FCSTD DOCUMENT  (FreeCAD 0.20R)
Label: frame_05
License: CC-BY 3.0
LicenseURL: http://creativecommons.org/licenses/by/3.0/
objects: Part::Cylinder×309, Part::MultiFuse×214, Part::Box×195, Part::Cut×178, Part::Feature×95, Part::Fillet×92, Part::Chamfer×30, Part::Mirroring×14, App::DocumentObjectGroup×14, Part::Loft×6, Part::Part2DObjectPython×2, Part::Extrusion×1
note: 1136 computed .brp shape members not serialized (recipe doc carries the construction recipe); baked Part::Feature solids carry a one-line shape summary decoded from their .brp

FEATURE [Part::Box] Box
  AttacherType = Attacher::AttachEngine3D
  Height = 20
  Length = 120
  Placement = pos=(30,0,0) rot=(0,0,1;0rad)
  Width = 10
FEATURE [Part::Box] Box001
  AttacherType = Attacher::AttachEngine3D
  Height = 17
  Length = 30
  Placement = pos=(0,0,1.5) rot=(0,0,1;0rad)
  Width = 8.5
FEATURE [Part::Cylinder] Cylinder
  Angle = 360
  AttacherType = Attacher::AttachEngine3D
  FirstAngle = 0
  Height = 0.1
  Placement = pos=(0,5,10) rot=(0,1,0;1.5708rad)
  Radius = 2.6
  SecondAngle = 0
FEATURE [Part::Box] Box007  label="Cube"
  AttacherType = Attacher::AttachEngine3D
  Height = 20
  Length = 330
  Width = 10
FEATURE [Part::Box] Box008  label="Cube001"
  AttacherType = Attacher::AttachEngine3D
  Height = 17
  Length = 430
  Placement = pos=(0,1.5,1.5) rot=(0,0,1;0rad)
  Width = 10
FEATURE [Part::Fillet] Fillet
  Base = -> Box007
  Edges = 2 edges r=3: [Edge9,Edge10]
FEATURE [Part::Fillet] Fillet001
  Base = -> Box008
  Edges = 2 edges r=2: [Edge9,Edge10]
FEATURE [Part::Cut] Cut003
  Base = -> Fillet
  Refine = true
  Tool = -> Fillet001
FEATURE [Part::Fillet] Fillet002
  Base = -> Box007
  Edges = 2 edges r=3: [Edge9,Edge10]
FEATURE [Part::Fillet] Fillet003
  Base = -> Box008
  Edges = 2 edges r=2: [Edge9,Edge10]
FEATURE [Part::Cut] Cut004
  Base = -> Fillet002
  Placement = pos=(0,-1.5,0) rot=(0,0,1;0rad)
  Refine = true
  Tool = -> Fillet003
FEATURE [Part::Mirroring] Part__Mirroring  label="Cut (Mirror #1)"
  Base = (0,0,0)
  Normal = (0,1,0)
  Placement = pos=(0,81.5,0) rot=(0,0,1;0rad)
  Source = -> Cut003
FEATURE [Part::Fillet] Fillet004  label="lower-plate_00"
  Edges = 2 edges r=0.25: [Edge74,Edge75]
  Placement = pos=(-3,100,59) rot=(0.57735,-0.57735,-0.57735;2.0944rad)
FEATURE [Part::Cylinder] Cylinder009
  Angle = 360
  AttacherType = Attacher::AttachEngine3D
  FirstAngle = 0
  Height = 11
  Placement = pos=(-2,66.5,-1) rot=(0,1,0;1.5708rad)
  Radius = 1.25
  SecondAngle = 0
FEATURE [Part::Cylinder] Cylinder010
  Angle = 360
  AttacherType = Attacher::AttachEngine3D
  FirstAngle = 0
  Height = 11
  Placement = pos=(-2,13.5,-1) rot=(0,1,0;1.5708rad)
  Radius = 1.25
  SecondAngle = 0
FEATURE [Part::Cylinder] Cylinder011
  Angle = 360
  AttacherType = Attacher::AttachEngine3D
  FirstAngle = 0
  Height = 15
  Placement = pos=(-2,23,15) rot=(0,1,0;1.5708rad)
  Radius = 1.25
  SecondAngle = 0
FEATURE [Part::Cylinder] Cylinder012
  Angle = 360
  AttacherType = Attacher::AttachEngine3D
  FirstAngle = 0
  Height = 15
  Placement = pos=(-2,57,15) rot=(0,1,0;1.5708rad)
  Radius = 1.25
  SecondAngle = 0
FEATURE [Part::MultiFuse] Fusion010
  Placement = pos=(0,0,1) rot=(0,0,1;0rad)
  Refine = true
  Shapes = -> [Cylinder009,Cylinder011,Cylinder010,Cylinder012]
FEATURE [Part::Cut] Cut005
  Refine = true
  Tool = -> Fusion010
FEATURE [Part::Cylinder] Cylinder013
  Angle = 360
  AttacherType = Attacher::AttachEngine3D
  FirstAngle = 0
  Height = 2.5
  Placement = pos=(-4.5,12.5,-1) rot=(0,1,0;1.5708rad)
  Radius = 2
  SecondAngle = 0
FEATURE [Part::Cylinder] Cylinder014
  Angle = 360
  AttacherType = Attacher::AttachEngine3D
  FirstAngle = 0
  Height = 2.5
  Placement = pos=(-4.5,67.5,-1) rot=(0,1,0;1.5708rad)
  Radius = 2
  SecondAngle = 0
FEATURE [Part::Cylinder] Cylinder015
  Angle = 360
  AttacherType = Attacher::AttachEngine3D
  FirstAngle = 0
  Height = 11
  Placement = pos=(-7,66.5,-1) rot=(0,1,0;1.5708rad)
  Radius = 1.6
  SecondAngle = 0
FEATURE [Part::Cylinder] Cylinder016
  Angle = 360
  AttacherType = Attacher::AttachEngine3D
  FirstAngle = 0
  Height = 11
  Placement = pos=(-7,13.5,-1) rot=(0,1,0;1.5708rad)
  Radius = 1.6
  SecondAngle = 0
FEATURE [Part::MultiFuse] Fusion011
  Refine = true
  Shapes = -> [Cylinder016,Cylinder015]
FEATURE [Part::MultiFuse] Fusion012
  Refine = true
  Shapes = -> [Cylinder014,Cylinder013]
FEATURE [Part::MultiFuse] Fusion013
  Refine = true
  Shapes = -> [Fillet004,Fusion012]
FEATURE [Part::Cut] Cut006  label="cab_tilt_lower001"
  Base = -> Fusion013
  Placement = pos=(0,0,1) rot=(0,0,1;0rad)
  Refine = true
  Tool = -> Fusion011
FEATURE [Part::Fillet] Fillet009
  Base = -> Cut005
  Edges = 2 edges r=3: [Edge4,Edge16]
FEATURE [Part::MultiFuse] Fusion015  label="frame-bars001"
  Refine = true
  Shapes = -> [Cut004,Part__Mirroring]
FEATURE [Part::Cut] Cut007  label="cab_tilt_upper001"
  Placement = pos=(-2,100,54) rot=(0.57735,-0.57735,-0.57735;2.0944rad)
  Refine = true
FEATURE [Part::Cylinder] Cylinder021
  Angle = 360
  AttacherType = Attacher::AttachEngine3D
  FirstAngle = 0
  Height = 10
  Placement = pos=(-8,33.5,0) rot=(0,0,1;0rad)
  Radius = 1.2
  SecondAngle = 0
FEATURE [Part::Cylinder] Cylinder022
  Angle = 360
  AttacherType = Attacher::AttachEngine3D
  FirstAngle = 0
  Height = 10
  Placement = pos=(-8,25.5,0) rot=(0,0,1;0rad)
  Radius = 1.2
  SecondAngle = 0
FEATURE [Part::MultiFuse] Fusion016
  Placement = pos=(334,78.5,-19.5) rot=(1,0,0;1.5708rad)
  Refine = true
  Shapes = -> [Cylinder021,Cylinder022]
FEATURE [Part::Cylinder] Cylinder023
  Angle = 360
  AttacherType = Attacher::AttachEngine3D
  FirstAngle = 0
  Height = 10
  Placement = pos=(-8,25.5,0) rot=(0,0,1;0rad)
  Radius = 1.2
  SecondAngle = 0
FEATURE [Part::Cylinder] Cylinder024
  Angle = 360
  AttacherType = Attacher::AttachEngine3D
  FirstAngle = 0
  Height = 10
  Placement = pos=(-8,33.5,0) rot=(0,0,1;0rad)
  Radius = 1.2
  SecondAngle = 0
FEATURE [Part::MultiFuse] Fusion017
  Placement = pos=(312,78.5,-19.5) rot=(1,0,0;1.5708rad)
  Refine = true
  Shapes = -> [Cylinder024,Cylinder023]
FEATURE [Part::MultiFuse] Fusion018
  Placement = pos=(-20,0,0) rot=(0,0,1;0rad)
  Refine = true
  Shapes = -> [Fusion016,Fusion017]
FEATURE [Part::Cylinder] Cylinder025
  Angle = 360
  AttacherType = Attacher::AttachEngine3D
  FirstAngle = 0
  Height = 10
  Placement = pos=(416,80,5) rot=(1,0,0;1.5708rad)
  Radius = 1.8
  SecondAngle = 0
FEATURE [Part::Box] Box011  label="Cube004"
  AttacherType = Attacher::AttachEngine3D
  Height = 10
  Length = 10
  Placement = pos=(400,7,3) rot=(0,0,1;0rad)
  Width = 66
FEATURE [Part::Box] Box012  label="Cube005"
  AttacherType = Attacher::AttachEngine3D
  Height = 10
  Length = 10
  Placement = pos=(400,10,-2) rot=(0,0,1;0rad)
  Width = 60
FEATURE [Part::Box] Box013  label="Cube006"
  AttacherType = Attacher::AttachEngine3D
  Height = 10
  Length = 10
  Placement = pos=(400,15,8) rot=(0,0,1;0rad)
  Width = 50
FEATURE [Part::Box] Box014  label="Cube007"
  AttacherType = Attacher::AttachEngine3D
  Height = 10.2
  Length = 10.2
  Placement = pos=(399.9,8,2.9) rot=(0,0,1;0rad)
  Width = 64
FEATURE [Part::Cylinder] Cylinder026
  Angle = 360
  AttacherType = Attacher::AttachEngine3D
  FirstAngle = 0
  Height = 10
  Placement = pos=(405,80,6) rot=(1,0,0;1.5708rad)
  Radius = 1.1
  SecondAngle = 0
FEATURE [Part::Cylinder] Cylinder027
  Angle = 360
  AttacherType = Attacher::AttachEngine3D
  FirstAngle = 0
  Height = 2.5
  Placement = pos=(405,80,6) rot=(1,0,0;1.5708rad)
  Radius = 2.5
  SecondAngle = 0
FEATURE [Part::Chamfer] Chamfer002
  Base = -> Box013
  Edges = 2 edges r=5: [Edge9,Edge11]
FEATURE [Part::Chamfer] Chamfer003
  Base = -> Box012
  Edges = 2 edges r=5: [Edge9,Edge11]
FEATURE [Part::MultiFuse] Fusion019
  Refine = true
  Shapes = -> [Box011,Chamfer003]
FEATURE [Part::Cut] Cut013
  Base = -> Fusion019
  Refine = true
  Tool = -> Chamfer002
FEATURE [Part::Cylinder] Cylinder029
  Angle = 360
  AttacherType = Attacher::AttachEngine3D
  FirstAngle = 0
  Height = 10
  Placement = pos=(405,17,6) rot=(1,0,0;1.5708rad)
  Radius = 0.8
  SecondAngle = 0
FEATURE [Part::Cylinder] Cylinder030
  Angle = 360
  AttacherType = Attacher::AttachEngine3D
  FirstAngle = 0
  Height = 10
  Placement = pos=(405,73,6) rot=(1,0,0;1.5708rad)
  Radius = 0.8
  SecondAngle = 0
FEATURE [Part::MultiFuse] Fusion020
  Placement = pos=(2,0,0) rot=(0,0,1;0rad)
  Refine = true
  Shapes = -> [Cylinder029,Cylinder030]
FEATURE [Part::Cylinder] Cylinder031
  Angle = 360
  AttacherType = Attacher::AttachEngine3D
  FirstAngle = 0
  Height = 10
  Placement = pos=(400,35,3) rot=(0,1,0;1.5708rad)
  Radius = 0.8
  SecondAngle = 0
FEATURE [Part::Cylinder] Cylinder032
  Angle = 360
  AttacherType = Attacher::AttachEngine3D
  FirstAngle = 0
  Height = 10
  Placement = pos=(400,45,3) rot=(0,1,0;1.5708rad)
  Radius = 0.8
  SecondAngle = 0
FEATURE [Part::MultiFuse] Fusion021
  Refine = true
  Shapes = -> [Cylinder032,Cylinder031]
FEATURE [Part::Cylinder] Cylinder033
  Angle = 360
  AttacherType = Attacher::AttachEngine3D
  FirstAngle = 0
  Height = 10
  Placement = pos=(-8,25.5,0) rot=(0,0,1;0rad)
  Radius = 1.2
  SecondAngle = 0
FEATURE [Part::Cylinder] Cylinder034
  Angle = 360
  AttacherType = Attacher::AttachEngine3D
  FirstAngle = 0
  Height = 10
  Placement = pos=(-8,33.5,0) rot=(0,0,1;0rad)
  Radius = 1.2
  SecondAngle = 0
FEATURE [Part::MultiFuse] Fusion022
  Placement = pos=(12,80,-19.5) rot=(1,0,0;1.5708rad)
  Refine = true
  Shapes = -> [Cylinder034,Cylinder033]
FEATURE [Part::Cylinder] Cylinder035
  Angle = 360
  AttacherType = Attacher::AttachEngine3D
  FirstAngle = 0
  Height = 10
  Placement = pos=(-8,33.5,0) rot=(0,0,1;0rad)
  Radius = 1.2
  SecondAngle = 0
FEATURE [Part::Cylinder] Cylinder036
  Angle = 360
  AttacherType = Attacher::AttachEngine3D
  FirstAngle = 0
  Height = 10
  Placement = pos=(-8,25.5,0) rot=(0,0,1;0rad)
  Radius = 1.2
  SecondAngle = 0
FEATURE [Part::MultiFuse] Fusion023
  Placement = pos=(12,10,-19.5) rot=(1,0,0;1.5708rad)
  Refine = true
  Shapes = -> [Cylinder035,Cylinder036]
FEATURE [Part::MultiFuse] Fusion024
  Refine = true
  Shapes = -> [Fusion022,Fusion023]
FEATURE [Part::Cut] Cut016  label="front-cross-member__"
  Base = -> Fillet009
  Refine = true
  Tool = -> Fusion024
FEATURE [Part::Cut] Cut017
  Base = -> Box
  Refine = true
FEATURE [Part::MultiFuse] Fusion027
  Refine = true
  Shapes = -> [Cut017,Box001]
FEATURE [Part::Cut] Cut018
  Base = -> Fusion027
  Placement = pos=(280,70,0) rot=(0,0,1;0rad)
  Refine = true
  Tool = -> Cylinder
FEATURE [Part::Cut] Cut019
  Base = -> Cut018
  Refine = true
  Tool = -> Fusion018
FEATURE [Part::Cut] Cut020
  Base = -> Cut019
  Refine = true
  Tool = -> Cylinder025
FEATURE [Part::Cut] Cut021
  Base = -> Cut020
  Refine = true
  Tool = -> Box014
FEATURE [Part::MultiFuse] Fusion028
  Placement = pos=(2,0,0) rot=(0,0,1;0rad)
  Refine = true
  Shapes = -> [Cylinder027,Cylinder026]
FEATURE [Part::Cut] Cut022
  Base = -> Cut021
  Refine = true
  Tool = -> Fusion028
FEATURE [Part::Fillet] Fillet016
  Base = -> Cut022
  Edges = 8 edges r=2.7: [Edge26,Edge28,Edge40,Edge42,Edge44,Edge46,Edge50,Edge52]
FEATURE [Part::Cut] Cut023
  Base = -> Cut021
  Refine = true
  Tool = -> Fusion028
FEATURE [Part::Fillet] Fillet017  label="rear-right-cross-member_"
  Base = -> Cut023
  Edges = 8 edges r=2.7: [Edge26,Edge28,Edge40,Edge42,Edge44,Edge46,Edge50,Edge52]
  Placement = pos=(20,1.5,0) rot=(0,0,1;0rad)
FEATURE [Part::Mirroring] Part__Mirroring001  label="rear-left-cross-member_"
  Base = (0,0,0)
  Normal = (0,1,0)
  Placement = pos=(20,78.5,0) rot=(0,0,1;0rad)
  Source = -> Fillet016
FEATURE [Part::Fillet] Fillet018
  Base = -> Cut013
  Edges = 8 edges r=5: [Edge2,Edge16,Edge29,Edge30,Edge33,Edge34,Edge35,Edge36]
FEATURE [Part::Cut] Cut024
  Base = -> Fillet018
  Refine = true
  Tool = -> Fusion021
FEATURE [Part::Cut] Cut025  label="rear-cross-member_"
  Base = -> Cut024
  Placement = pos=(20,0,0) rot=(0,0,1;0rad)
  Refine = true
  Tool = -> Fusion020
FEATURE [Part::Box] Box015  label="Cube008"
  AttacherType = Attacher::AttachEngine3D
  Height = 17
  Length = 12
  Placement = pos=(300,8,1.5) rot=(0,0,1;0rad)
  Width = 63
FEATURE [Part::Box] Box016  label="Cube009"
  AttacherType = Attacher::AttachEngine3D
  Height = 14
  Length = 1
  Placement = pos=(311,8,3) rot=(0,0,1;0rad)
  Width = 63
FEATURE [Part::Cut] Cut026
  Base = -> Box015
  Refine = true
  Tool = -> Box016
FEATURE [Part::Cylinder] Cylinder037
  Angle = 360
  AttacherType = Attacher::AttachEngine3D
  FirstAngle = 0
  Height = 10
  Placement = pos=(-8,33.5,0) rot=(0,0,1;0rad)
  Radius = 1.2
  SecondAngle = 0
FEATURE [Part::Cylinder] Cylinder038
  Angle = 360
  AttacherType = Attacher::AttachEngine3D
  FirstAngle = 0
  Height = 10
  Placement = pos=(-8,25.5,0) rot=(0,0,1;0rad)
  Radius = 1.2
  SecondAngle = 0
FEATURE [Part::MultiFuse] Fusion029
  Placement = pos=(312,18,-19.5) rot=(1,0,0;1.5708rad)
  Refine = true
  Shapes = -> [Cylinder037,Cylinder038]
FEATURE [Part::Cylinder] Cylinder039
  Angle = 360
  AttacherType = Attacher::AttachEngine3D
  FirstAngle = 0
  Height = 10
  Placement = pos=(-8,33.5,0) rot=(0,0,1;0rad)
  Radius = 1.2
  SecondAngle = 0
FEATURE [Part::Cylinder] Cylinder040
  Angle = 360
  AttacherType = Attacher::AttachEngine3D
  FirstAngle = 0
  Height = 10
  Placement = pos=(-8,25.5,0) rot=(0,0,1;0rad)
  Radius = 1.2
  SecondAngle = 0
FEATURE [Part::MultiFuse] Fusion030
  Placement = pos=(312,71,-19.5) rot=(1,0,0;1.5708rad)
  Refine = true
  Shapes = -> [Cylinder039,Cylinder040]
FEATURE [Part::MultiFuse] Fusion031
  Refine = true
  Shapes = -> [Fusion029,Fusion030]
FEATURE [Part::Cut] Cut027  label="middle-cross-member_"
  Base = -> Cut026
  Placement = pos=(20,0.5,0) rot=(0,0,1;0rad)
  Refine = true
  Tool = -> Fusion031
FEATURE [Part::Box] Box017  label="Cube010"
  AttacherType = Attacher::AttachEngine3D
  Height = 15
  Length = 30
  Placement = pos=(0,-0.25,0) rot=(0,0,1;0rad)
  Width = 11.5
FEATURE [Part::Box] Box018  label="Cube011"
  AttacherType = Attacher::AttachEngine3D
  Height = 8
  Length = 15
  Placement = pos=(16,1.75,0) rot=(0,0,1;0rad)
  Width = 7.5
FEATURE [Part::Box] Box019  label="Cube012"
  AttacherType = Attacher::AttachEngine3D
  Height = 15
  Length = 15
  Placement = pos=(0,-0.25,0) rot=(0,0,1;0rad)
  Width = 2.25
FEATURE [Part::Box] Box020  label="Cube013"
  AttacherType = Attacher::AttachEngine3D
  Height = 15
  Length = 15
  Placement = pos=(0,9,0) rot=(0,0,1;0rad)
  Width = 2.25
FEATURE [Part::MultiFuse] Fusion032
  Refine = true
  Shapes = -> [Box019,Box020]
FEATURE [Part::Cylinder] Cylinder041
  Angle = 360
  AttacherType = Attacher::AttachEngine3D
  FirstAngle = 0
  Height = 14.5
  Placement = pos=(20,12.25,4) rot=(1,0,0;1.5708rad)
  Radius = 2.1
  SecondAngle = 0
FEATURE [Part::Cylinder] Cylinder042
  Angle = 360
  AttacherType = Attacher::AttachEngine3D
  FirstAngle = 0
  Height = 15
  Placement = pos=(12,5.5,0) rot=(0,0,1;0rad)
  Radius = 1.6
  SecondAngle = 0
FEATURE [Part::Cylinder] Cylinder043
  Angle = 360
  AttacherType = Attacher::AttachEngine3D
  FirstAngle = 0
  Height = 15
  Placement = pos=(20,5.5,0) rot=(0,0,1;0rad)
  Radius = 1.6
  SecondAngle = 0
FEATURE [Part::Cylinder] Cylinder044
  Angle = 360
  AttacherType = Attacher::AttachEngine3D
  FirstAngle = 0
  Height = 11
  Placement = pos=(7,12,10.5) rot=(1,0,0;1.5708rad)
  Radius = 2.1
  SecondAngle = 0
FEATURE [Part::MultiFuse] Fusion033
  Refine = true
  Shapes = -> [Cylinder041,Cylinder044]
FEATURE [Part::Box] Box021  label="Cube014"
  AttacherType = Attacher::AttachEngine3D
  Height = 10
  Length = 10
  Placement = pos=(-7,0,6) rot=(0,0,1;0rad)
  Width = 10
FEATURE [Part::Box] Box022  label="Cube015"
  AttacherType = Attacher::AttachEngine3D
  Height = 9
  Length = 16
  Placement = pos=(2,2,8) rot=(0,0,1;0rad)
  Width = 7
FEATURE [Part::Cylinder] Cylinder045
  Angle = 360
  AttacherType = Attacher::AttachEngine3D
  FirstAngle = 0
  Height = 11
  Placement = pos=(10,11,11.5) rot=(1,0,0;1.5708rad)
  Radius = 2.1
  SecondAngle = 0
FEATURE [Part::Cylinder] Cylinder046
  Angle = 360
  AttacherType = Attacher::AttachEngine3D
  FirstAngle = 0
  Height = 17
  Placement = pos=(14,5.5,0) rot=(0,0,1;0rad)
  Radius = 1.6
  SecondAngle = 0
FEATURE [Part::Cylinder] Cylinder047
  Angle = 360
  AttacherType = Attacher::AttachEngine3D
  FirstAngle = 0
  Height = 17
  Placement = pos=(6,5.5,0) rot=(0,0,1;0rad)
  Radius = 1.6
  SecondAngle = 0
FEATURE [Part::Box] Box023  label="Cube016"
  AttacherType = Attacher::AttachEngine3D
  Height = 15
  Length = 16
  Placement = pos=(0,-0.25,0) rot=(0,0,1;0rad)
  Width = 11.5
FEATURE [Part::Box] Box024  label="Cube017"
  AttacherType = Attacher::AttachEngine3D
  Height = 8
  Length = 16
  Placement = pos=(0,1.75,0) rot=(0,0,1;0rad)
  Width = 7.5
FEATURE [Part::Cut] Cut028
  Base = -> Box023
  Placement = pos=(2,0,0) rot=(0,0,1;0rad)
  Refine = true
  Tool = -> Box024
FEATURE [Part::Cylinder] Cylinder048
  Angle = 360
  AttacherType = Attacher::AttachEngine3D
  FirstAngle = 0
  Height = 11.5
  Placement = pos=(10,11.25,4) rot=(1,0,0;1.5708rad)
  Radius = 2.1
  SecondAngle = 0
FEATURE [Part::Cylinder] Cylinder049
  Angle = 360
  AttacherType = Attacher::AttachEngine3D
  FirstAngle = 0
  Height = 15
  Placement = pos=(6,5.5,0) rot=(0,0,1;0rad)
  Radius = 1.6
  SecondAngle = 0
FEATURE [Part::Cylinder] Cylinder050
  Angle = 360
  AttacherType = Attacher::AttachEngine3D
  FirstAngle = 0
  Height = 15
  Placement = pos=(14,5.5,0) rot=(0,0,1;0rad)
  Radius = 1.6
  SecondAngle = 0
FEATURE [Part::MultiFuse] Fusion034
  Refine = true
  Shapes = -> [Cylinder048,Cylinder050,Cylinder049]
FEATURE [Part::Cut] Cut029
  Base = -> Cut028
  Refine = true
  Tool = -> Fusion034
FEATURE [Part::Box] Box025  label="Cube018"
  AttacherType = Attacher::AttachEngine3D
  Height = 9
  Length = 24
  Width = 14
FEATURE [Part::Box] Box026  label="Cube019"
  AttacherType = Attacher::AttachEngine3D
  Height = 7.5
  Length = 8
  Placement = pos=(16,2,0) rot=(0,0,1;0rad)
  Width = 7.5
FEATURE [Part::Cylinder] Cylinder051
  Angle = 360
  AttacherType = Attacher::AttachEngine3D
  FirstAngle = 0
  Height = 14
  Placement = pos=(20,13,4) rot=(1,0,0;1.5708rad)
  Radius = 2.1
  SecondAngle = 0
FEATURE [Part::Cylinder] Cylinder052
  Angle = 360
  AttacherType = Attacher::AttachEngine3D
  FirstAngle = 0
  Height = 15
  Placement = pos=(12,7.5,0) rot=(0,0,1;0rad)
  Radius = 1.6
  SecondAngle = 0
FEATURE [Part::Cylinder] Cylinder053
  Angle = 360
  AttacherType = Attacher::AttachEngine3D
  FirstAngle = 0
  Height = 15
  Placement = pos=(4,7.5,0) rot=(0,0,1;0rad)
  Radius = 1.6
  SecondAngle = 0
FEATURE [Part::Cylinder] Cylinder054
  Angle = 360
  AttacherType = Attacher::AttachEngine3D
  FirstAngle = 0
  Height = 4
  Placement = pos=(12,7.5,0) rot=(0,0,1;0rad)
  Radius = 3.2
  SecondAngle = 0
FEATURE [Part::Cylinder] Cylinder055
  Angle = 360
  AttacherType = Attacher::AttachEngine3D
  FirstAngle = 0
  Height = 4
  Placement = pos=(4,7.5,0) rot=(0,0,1;0rad)
  Radius = 3.2
  SecondAngle = 0
FEATURE [Part::MultiFuse] Fusion035
  Placement = pos=(0,1,0) rot=(0,0,1;0rad)
  Refine = true
  Shapes = -> [Cylinder051,Cylinder052,Cylinder053,Cylinder054,Cylinder055]
FEATURE [Part::Chamfer] Chamfer004
  Base = -> Box025
  Edges = 1 edges r=5: [Edge4]
FEATURE [Part::Cut] Cut030
  Base = -> Chamfer004
  Refine = true
  Tool = -> Box026
FEATURE [Part::Cylinder] Cylinder056
  Angle = 360
  AttacherType = Attacher::AttachEngine3D
  FirstAngle = 0
  Height = 11
  Placement = pos=(20,5.5,0) rot=(0,0,1;0rad)
  Radius = 3.1
  SecondAngle = 0
FEATURE [Part::Cylinder] Cylinder057
  Angle = 360
  AttacherType = Attacher::AttachEngine3D
  FirstAngle = 0
  Height = 11
  Placement = pos=(12,5.5,0) rot=(0,0,1;0rad)
  Radius = 3.1
  SecondAngle = 0
FEATURE [Part::MultiFuse] Fusion036
  Refine = true
  Shapes = -> [Cylinder056,Cylinder042,Cylinder043,Cylinder057]
FEATURE [Part::Box] Box027  label="Cube020"
  AttacherType = Attacher::AttachEngine3D
  Height = 18
  Length = 10
  Placement = pos=(25,-1,0) rot=(0,0,1;0rad)
  Width = 13
FEATURE [Part::Box] Box028  label="Cube021"
  AttacherType = Attacher::AttachEngine3D
  Height = 6
  Length = 16
  Placement = pos=(0,1.75,0) rot=(0,0,1;0rad)
  Width = 7.5
FEATURE [Part::MultiFuse] Fusion037
  Refine = true
  Shapes = -> [Box018,Box028]
FEATURE [Part::Cut] Cut033
  Base = -> Box017
  Refine = true
  Tool = -> Fusion037
FEATURE [Part::Cut] Cut034
  Base = -> Cut033
  Refine = true
  Tool = -> Fusion032
FEATURE [Part::Cut] Cut035
  Base = -> Cut034
  Refine = true
  Tool = -> Fusion036
FEATURE [Part::Cut] Cut036
  Base = -> Cut035
  Refine = true
  Tool = -> Fusion033
FEATURE [Part::MultiFuse] Fusion038
  Refine = true
  Shapes = -> [Box021,Box027]
FEATURE [Part::Cut] Cut037
  Base = -> Cut036
  Refine = true
  Tool = -> Fusion038
FEATURE [Part::Chamfer] Chamfer005
  Base = -> Cut029
  Edges = 4 edges r=5: [Edge3,Edge7,Edge17,Edge29]
FEATURE [Part::Fillet] Fillet022
  Base = -> Chamfer005
  Edges = 8 edges r=3: [Edge2,Edge7,Edge16,Edge35,Edge41,Edge42,Edge43,Edge47]
  Placement = pos=(22.5,71.75,-15) rot=(0,0,1;0rad)
FEATURE [Part::Cut] Cut038
  Placement = pos=(241.5,71.75,-16) rot=(0,0,1;0rad)
  Refine = true
FEATURE [Part::Chamfer] Chamfer009
  Base = -> Box022
  Edges = 2 edges r=1: [Edge4,Edge8]
FEATURE [Part::MultiFuse] Fusion040
  Refine = true
  Shapes = -> [Cylinder045,Cylinder046,Cylinder047]
FEATURE [Part::Cut] Cut039
  Base = -> Chamfer009
  Placement = pos=(241.5,-2.75,-16) rot=(0,0,1;0rad)
  Refine = true
  Tool = -> Fusion040
FEATURE [Part::Chamfer] Chamfer010
  Base = -> Cut029
  Edges = 4 edges r=5: [Edge3,Edge7,Edge17,Edge29]
FEATURE [Part::Fillet] Fillet025
  Base = -> Chamfer010
  Edges = 8 edges r=3: [Edge2,Edge7,Edge16,Edge35,Edge41,Edge42,Edge43,Edge47]
  Placement = pos=(22.5,-2.75,-15) rot=(0,0,1;0rad)
FEATURE [Part::Cut] Cut040
  Base = -> Cut030
  Placement = pos=(0,-5.5,-9) rot=(0,0,1;0rad)
  Refine = true
  Tool = -> Fusion035
FEATURE [Part::Box] Box029  label="Cube022"
  AttacherType = Attacher::AttachEngine3D
  Height = 10
  Length = 13
  Placement = pos=(0,-5.5,-9) rot=(0,0,1;0rad)
  Width = 4
FEATURE [Part::Cut] Cut041
  Base = -> Cut040
  Refine = true
  Tool = -> Box029
FEATURE [Part::Box] Box030  label="Cube023"
  AttacherType = Attacher::AttachEngine3D
  Height = 5
  Length = 13
  Placement = pos=(0,-2.5,-3) rot=(1,0,0;0.785398rad)
  Width = 5
FEATURE [Part::Cut] Cut043
  Base = -> Cut041
  Refine = true
  Tool = -> Box030
FEATURE [Part::Fillet] Fillet027
  Base = -> Cut043
  Edges = 1 edges r=2: [Edge14]
  Placement = pos=(290,0,0) rot=(0,0,1;0rad)
FEATURE [Part::Fillet] Fillet028
  Base = -> Fillet027
  Edges = 2 edges r=3: [Edge12,Edge13]
FEATURE [Part::Fillet] Fillet029
  Base = -> Fillet028
  Edges = 1 edges r=2.99: [Edge47]
FEATURE [Part::Chamfer] Chamfer011  label="front-left-front-ls-mount"
  Base = -> Fillet025
  Edges = 1 edges r=3.5: [Edge21]
FEATURE [Part::Chamfer] Chamfer012  label="front-right-front-ls-mount"
  Base = -> Fillet022
  Edges = 1 edges r=3.5: [Edge17]
FEATURE [Part::Chamfer] Chamfer015  label="front-left-rear-ls-mount"
  Base = -> Cut039
  Edges = 1 edges r=1.5: [Edge9]
FEATURE [Part::Chamfer] Chamfer016  label="front-right-rear-ls-mount"
  Base = -> Cut038
  Edges = 1 edges r=1.5: [Edge13]
FEATURE [Part::Fillet] Fillet030
  Base = -> Fillet027
  Edges = 2 edges r=3: [Edge12,Edge13]
FEATURE [Part::Fillet] Fillet031  label="rear-left-ls-mount_"
  Base = -> Fillet030
  Edges = 1 edges r=2.99: [Edge47]
  Placement = pos=(20,0,0) rot=(0,0,1;0rad)
FEATURE [Part::Mirroring] Part__Mirroring004  label="rear-right-ls-mount_"
  Base = (0,0,0)
  Normal = (0,1,0)
  Placement = pos=(20,80,0) rot=(0,0,1;0rad)
  Source = -> Fillet029
FEATURE [Part::Box] Box031
  AttacherType = Attacher::AttachEngine3D
  Height = 1
  Length = 16
  Placement = pos=(-2,9,18.5) rot=(0,0,1;0rad)
  Width = 62
FEATURE [Part::MultiFuse] Fusion041  label="front-cross-member_"
  Refine = true
  Shapes = -> [Cut016,Box031]
FEATURE [Part::Box] Box032
  AttacherType = Attacher::AttachEngine3D
  Height = 15
  Length = 10
  Placement = pos=(15,-1.25,0) rot=(0,0,1;0rad)
  Width = 1
FEATURE [Part::Box] Box033
  AttacherType = Attacher::AttachEngine3D
  Height = 15
  Length = 10
  Placement = pos=(15,11.25,0) rot=(0,0,1;0rad)
  Width = 1
FEATURE [Part::MultiFuse] Fusion042
  Refine = true
  Shapes = -> [Cut037,Box032,Box033]
FEATURE [Part::Cylinder] Cylinder058
  Angle = 360
  AttacherType = Attacher::AttachEngine3D
  FirstAngle = 0
  Height = 14.5
  Placement = pos=(20,12.25,4) rot=(1,0,0;1.5708rad)
  Radius = 2.1
  SecondAngle = 0
FEATURE [Part::Cut] Cut044
  Base = -> Fusion042
  Refine = true
  Tool = -> Cylinder058
FEATURE [Part::Box] Box034
  AttacherType = Attacher::AttachEngine3D
  Height = 10
  Length = 10
  Placement = pos=(7,0.5,-1.07) rot=(0,1,0;0.785398rad)
  Width = 10
FEATURE [Part::Cut] Cut045
  Base = -> Cut044
  Refine = true
  Tool = -> Box034
FEATURE [Part::Chamfer] Chamfer017
  Base = -> Cut045
  Edges = 1 edges r=4.5: [Edge7]
FEATURE [Part::Chamfer] Chamfer018
  Base = -> Chamfer017
  Edges = 4 edges r=3: [Edge36,Edge37,Edge46,Edge54]
FEATURE [Part::Chamfer] Chamfer019
  Base = -> Chamfer018
  Edges = 1 edges r=3: [Edge66]
FEATURE [Part::Fillet] Fillet032
  Base = -> Chamfer019
  Edges = 9 edges r=3: [Edge2,Edge16,Edge38,Edge62,Edge67,Edge77,Edge95,Edge114,Edge117]
FEATURE [Part::Chamfer] Chamfer020
  Base = -> Fillet032
  Edges = 1 edges r=1: [Edge22]
FEATURE [Part::Fillet] Fillet033
  Base = -> Chamfer019
  Edges = 9 edges r=3: [Edge2,Edge16,Edge38,Edge62,Edge67,Edge77,Edge95,Edge114,Edge117]
FEATURE [Part::Chamfer] Chamfer021  label="front-left-middle-ls-mount"
  Base = -> Fillet033
  Edges = 1 edges r=1: [Edge22]
  Placement = pos=(128.5,-2.75,-15) rot=(0,0,1;0rad)
FEATURE [Part::Mirroring] Part__Mirroring005  label="front-right-middle-ls-mount"
  Base = (0,0,0)
  Normal = (0,1,0)
  Placement = pos=(128.5,82.75,-15) rot=(0,0,1;0rad)
  Source = -> Chamfer020
FEATURE [Part::Box] Box035  label="Cube024"
  AttacherType = Attacher::AttachEngine3D
  Height = 25
  Length = 7
  Placement = pos=(8,16,-5) rot=(0,0,1;0rad)
  Width = 48
FEATURE [Part::Cut] Cut046
  Base = -> Fusion041
  Refine = true
  Tool = -> Box035
FEATURE [Part::Box] Box036  label="Cube025"
  AttacherType = Attacher::AttachEngine3D
  Height = 12
  Length = 15
  Placement = pos=(8,16,7.5) rot=(0,0,1;0rad)
  Width = 7
FEATURE [Part::Box] Box038  label="Cube027"
  AttacherType = Attacher::AttachEngine3D
  Height = 18
  Length = 3
  Placement = pos=(8,16,1.5) rot=(0,0,1;0rad)
  Width = 48
FEATURE [Part::Box] Box039  label="Cube028"
  AttacherType = Attacher::AttachEngine3D
  Height = 12
  Length = 12
  Placement = pos=(11,53,7.5) rot=(0,0,1;0rad)
  Width = 11
FEATURE [Part::Cylinder] Cylinder059
  Angle = 360
  AttacherType = Attacher::AttachEngine3D
  FirstAngle = 0
  Height = 15
  Placement = pos=(17,19.5,1.5) rot=(0,0,1;0rad)
  Radius = 0.9
  SecondAngle = 0
FEATURE [Part::Cylinder] Cylinder060
  Angle = 360
  AttacherType = Attacher::AttachEngine3D
  FirstAngle = 0
  Height = 15
  Placement = pos=(17,55.5,1.5) rot=(0,0,1;0rad)
  Radius = 0.9
  SecondAngle = 0
FEATURE [Part::MultiFuse] Fusion044
  Placement = pos=(0,0.5,4) rot=(0,0,1;0rad)
  Refine = true
  Shapes = -> [Cylinder059,Cylinder060]
FEATURE [Part::Cylinder] Cylinder061
  Angle = 360
  AttacherType = Attacher::AttachEngine3D
  FirstAngle = 0
  Height = 10
  Placement = pos=(-2,23,16) rot=(0,1,0;1.5708rad)
  Radius = 1.25
  SecondAngle = 0
FEATURE [Part::Cylinder] Cylinder062
  Angle = 360
  AttacherType = Attacher::AttachEngine3D
  FirstAngle = 0
  Height = 10
  Placement = pos=(-2,57,16) rot=(0,1,0;1.5708rad)
  Radius = 1.25
  SecondAngle = 0
FEATURE [Part::MultiFuse] Fusion045
  Refine = true
  Shapes = -> [Cylinder062,Cylinder061]
FEATURE [Part::Cylinder] Cylinder063
  Angle = 360
  AttacherType = Attacher::AttachEngine3D
  FirstAngle = 0
  Height = 10
  Placement = pos=(-2,23,16) rot=(0,1,0;1.5708rad)
  Radius = 1.25
  SecondAngle = 0
FEATURE [Part::Cylinder] Cylinder064
  Angle = 360
  AttacherType = Attacher::AttachEngine3D
  FirstAngle = 0
  Height = 10
  Placement = pos=(-2,57,16) rot=(0,1,0;1.5708rad)
  Radius = 1.25
  SecondAngle = 0
FEATURE [Part::MultiFuse] Fusion046
  Placement = pos=(0,0,-6) rot=(0,0,1;0rad)
  Refine = true
  Shapes = -> [Cylinder064,Cylinder063]
FEATURE [Part::MultiFuse] Fusion047
  Refine = true
  Shapes = -> [Cut046,Box036,Box038,Box039]
FEATURE [Part::Cut] Cut047
  Base = -> Fusion047
  Refine = true
  Tool = -> Fusion044
FEATURE [Part::MultiFuse] Fusion048
  Refine = true
  Shapes = -> [Fusion045,Cut047]
FEATURE [Part::Cut] Cut048
  Base = -> Fusion048
  Refine = true
  Tool = -> Fusion046
FEATURE [Part::Mirroring] Part__Mirroring006  label="Cut048 (Mirror #5)"
  Base = (0,0,0)
  Normal = (0,1,0)
  Source = -> Cut048
FEATURE [Part::Fillet] Fillet034
  Base = -> Part__Mirroring006
  Edges = 2 edges r=5: [Edge102,Edge118]
FEATURE [Part::Fillet] Fillet035
  Base = -> Fillet034
  Edges = 4 edges r=3: [Edge33,Edge54,Edge77,Edge79]
FEATURE [Part::Box] Box040
  AttacherType = Attacher::AttachEngine3D
  Height = 10
  Length = 10
  Placement = pos=(8,-18.5,-6.5) rot=(0,0,1;0rad)
  Width = 10
FEATURE [Part::Cut] Cut049
  Base = -> Fillet035
  Refine = true
  Tool = -> Box040
FEATURE [Part::Cylinder] Cylinder065
  Angle = 360
  AttacherType = Attacher::AttachEngine3D
  FirstAngle = 0
  Height = 10
  Placement = pos=(3,-59,-5) rot=(0,0,1;0rad)
  Radius = 1.25
  SecondAngle = 0
FEATURE [Part::Cylinder] Cylinder066
  Angle = 360
  AttacherType = Attacher::AttachEngine3D
  FirstAngle = 0
  Height = 10
  Placement = pos=(3,-21,-5) rot=(0,0,1;0rad)
  Radius = 1.25
  SecondAngle = 0
FEATURE [Part::MultiFuse] Fusion049
  Refine = true
  Shapes = -> [Cylinder065,Cylinder066]
FEATURE [Part::Cylinder] Cylinder067
  Angle = 360
  AttacherType = Attacher::AttachEngine3D
  FirstAngle = 0
  Height = 10
  Placement = pos=(5,-63,9.5) rot=(0,0,1;0rad)
  Radius = 1.25
  SecondAngle = 0
FEATURE [Part::Cylinder] Cylinder068
  Angle = 360
  AttacherType = Attacher::AttachEngine3D
  FirstAngle = 0
  Height = 10
  Placement = pos=(5,-17,9.5) rot=(0,0,1;0rad)
  Radius = 1.25
  SecondAngle = 0
FEATURE [Part::MultiFuse] Fusion050
  Refine = true
  Shapes = -> [Cylinder067,Cylinder068]
FEATURE [Part::Cut] Cut050
  Base = -> Cut049
  Refine = true
  Tool = -> Fusion049
FEATURE [Part::Cut] Cut051  label="front-cross-member"
  Base = -> Cut050
  Placement = pos=(2,80,0) rot=(0,0,1;0rad)
  Refine = true
  Tool = -> Fusion050
FEATURE [Part::Cylinder] Cylinder069
  Angle = 180
  AttacherType = Attacher::AttachEngine3D
  FirstAngle = 0
  Height = 48
  Placement = pos=(98,168,-23) rot=(1,0,0;1.5708rad)
  Radius = 52
  SecondAngle = 0
FEATURE [Part::Cylinder] Cylinder070
  Angle = 180
  AttacherType = Attacher::AttachEngine3D
  FirstAngle = 0
  Height = 48
  Placement = pos=(98,168,-27) rot=(1,0,0;1.5708rad)
  Radius = 47
  SecondAngle = 0
FEATURE [Part::Cut] Cut053
  Base = -> Cylinder069
  Refine = true
  Tool = -> Cylinder070
FEATURE [Part::Cylinder] Cylinder071
  Angle = 180
  AttacherType = Attacher::AttachEngine3D
  FirstAngle = 0
  Height = 48
  Placement = pos=(98,167,-23) rot=(1,0,0;1.5708rad)
  Radius = 50
  SecondAngle = 0
FEATURE [Part::Cut] Cut052
  Base = -> Cut053
  Placement = pos=(93,-35.5,3) rot=(0,0,1;0rad)
  Refine = true
  Tool = -> Cylinder071
FEATURE [Part::Cylinder] Cylinder072
  Angle = 180
  AttacherType = Attacher::AttachEngine3D
  FirstAngle = 0
  Height = 2
  Placement = pos=(191,123,-20) rot=(1,0,0;1.5708rad)
  Radius = 52.5
  SecondAngle = 0
FEATURE [Part::Cylinder] Cylinder073
  Angle = 180
  AttacherType = Attacher::AttachEngine3D
  FirstAngle = 0
  Height = 2
  Placement = pos=(191,110,-20) rot=(1,0,0;1.5708rad)
  Radius = 52.5
  SecondAngle = 0
FEATURE [Part::Cylinder] Cylinder074
  Angle = 180
  AttacherType = Attacher::AttachEngine3D
  FirstAngle = 0
  Height = 2
  Placement = pos=(191,97,-20) rot=(1,0,0;1.5708rad)
  Radius = 52.5
  SecondAngle = 0
FEATURE [Part::MultiFuse] Fusion051
  Placement = pos=(0,-1,0) rot=(0,0,1;0rad)
  Refine = true
  Shapes = -> [Cylinder074,Cylinder072,Cylinder073]
FEATURE [Part::Cylinder] Cylinder075
  Angle = 180
  AttacherType = Attacher::AttachEngine3D
  FirstAngle = 0
  Height = 48
  Placement = pos=(191,132,-20) rot=(1,0,0;1.5708rad)
  Radius = 50
  SecondAngle = 0
FEATURE [Part::Cut] Cut054
  Base = -> Fusion051
  Refine = true
  Tool = -> Cylinder075
FEATURE [Part::Fillet] Fillet036
  Base = -> Cut054
  Edges = 6 edges r=0.6: [Edge1,Edge3,Edge13,Edge15,Edge25,Edge27]
FEATURE [Part::MultiFuse] Fusion052
  Placement = pos=(6,0,0) rot=(0,0,1;0rad)
  Refine = true
  Shapes = -> [Cut052,Fillet036]
FEATURE [Part::Cylinder] Cylinder076
  Angle = 180
  AttacherType = Attacher::AttachEngine3D
  FirstAngle = 0
  Height = 48
  Placement = pos=(98,168,-23) rot=(1,0,0;1.5708rad)
  Radius = 52
  SecondAngle = 0
FEATURE [Part::Cylinder] Cylinder077
  Angle = 180
  AttacherType = Attacher::AttachEngine3D
  FirstAngle = 0
  Height = 48
  Placement = pos=(98,168,-27) rot=(1,0,0;1.5708rad)
  Radius = 47
  SecondAngle = 0
FEATURE [Part::Cut] Cut056
  Base = -> Cylinder076
  Refine = true
  Tool = -> Cylinder077
FEATURE [Part::Cylinder] Cylinder078
  Angle = 180
  AttacherType = Attacher::AttachEngine3D
  FirstAngle = 0
  Height = 48
  Placement = pos=(98,167,-23) rot=(1,0,0;1.5708rad)
  Radius = 50
  SecondAngle = 0
FEATURE [Part::Cut] Cut055
  Base = -> Cut056
  Placement = pos=(93,-35.5,3) rot=(0,0,1;0rad)
  Refine = true
  Tool = -> Cylinder078
FEATURE [Part::Cylinder] Cylinder079
  Angle = 180
  AttacherType = Attacher::AttachEngine3D
  FirstAngle = 0
  Height = 2
  Placement = pos=(191,97,-20) rot=(1,0,0;1.5708rad)
  Radius = 52.5
  SecondAngle = 0
FEATURE [Part::Cylinder] Cylinder080
  Angle = 180
  AttacherType = Attacher::AttachEngine3D
  FirstAngle = 0
  Height = 2
  Placement = pos=(191,123,-20) rot=(1,0,0;1.5708rad)
  Radius = 52.5
  SecondAngle = 0
FEATURE [Part::Cylinder] Cylinder081
  Angle = 180
  AttacherType = Attacher::AttachEngine3D
  FirstAngle = 0
  Height = 2
  Placement = pos=(191,110,-20) rot=(1,0,0;1.5708rad)
  Radius = 52.5
  SecondAngle = 0
FEATURE [Part::MultiFuse] Fusion054
  Placement = pos=(0,-1,0) rot=(0,0,1;0rad)
  Refine = true
  Shapes = -> [Cylinder079,Cylinder080,Cylinder081]
FEATURE [Part::Cylinder] Cylinder082
  Angle = 180
  AttacherType = Attacher::AttachEngine3D
  FirstAngle = 0
  Height = 48
  Placement = pos=(191,132,-20) rot=(1,0,0;1.5708rad)
  Radius = 50
  SecondAngle = 0
FEATURE [Part::Cut] Cut057
  Base = -> Fusion054
  Refine = true
  Tool = -> Cylinder082
FEATURE [Part::Fillet] Fillet037
  Base = -> Cut057
  Edges = 6 edges r=0.6: [Edge1,Edge3,Edge13,Edge15,Edge25,Edge27]
FEATURE [Part::MultiFuse] Fusion053
  Placement = pos=(189,0,0) rot=(0,0,1;0rad)
  Refine = true
  Shapes = -> [Cut055,Fillet037]
FEATURE [Part::Box] Box043  label="battery-pack"
  AttacherType = Attacher::AttachEngine3D
  Height = 30
  Length = 60
  Placement = pos=(259,83.5,-24) rot=(0,0,1;0rad)
  Width = 45
FEATURE [Part::Fillet] Fillet039
  Base = -> Fusion052
  Edges = 2 edges r=2: [Edge2,Edge11]
FEATURE [Part::Fillet] Fillet040
  Base = -> Fusion053
  Edges = 2 edges r=2: [Edge2,Edge11]
FEATURE [Part::Box] Box044  label="Cube032"
  AttacherType = Attacher::AttachEngine3D
  Height = 15
  Length = 10
  Placement = pos=(153.3,119,13.9) rot=(0,1,0;1.13446rad)
  Width = 4
FEATURE [Part::Box] Box045  label="Cube033"
  AttacherType = Attacher::AttachEngine3D
  Height = 25
  Length = 10
  Placement = pos=(146,119,-10) rot=(0,1,0;0.296706rad)
  Width = 4
FEATURE [Part::Cylinder] Cylinder084
  Angle = 360
  AttacherType = Attacher::AttachEngine3D
  FirstAngle = 0
  Height = 4
  Placement = pos=(154,123,13) rot=(1,0,0;1.5708rad)
  Radius = 2.5
  SecondAngle = 0
FEATURE [Part::MultiFuse] Fusion055
  Refine = true
  Shapes = -> [Box044,Box045,Cylinder084]
FEATURE [Part::Cylinder] Cylinder085
  Angle = 360
  AttacherType = Attacher::AttachEngine3D
  FirstAngle = 0
  Height = 4
  Placement = pos=(154,123,13) rot=(1,0,0;1.5708rad)
  Radius = 1.25
  SecondAngle = 0
FEATURE [Part::Cut] Cut058
  Base = -> Fusion055
  Refine = true
  Tool = -> Cylinder085
FEATURE [Part::Box] Box048  label="Cube036"
  AttacherType = Attacher::AttachEngine3D
  Height = 15
  Length = 10
  Placement = pos=(153.3,119,13.9) rot=(0,1,0;1.13446rad)
  Width = 4
FEATURE [Part::Box] Box049  label="Cube037"
  AttacherType = Attacher::AttachEngine3D
  Height = 25
  Length = 10
  Placement = pos=(146,119,-10) rot=(0,1,0;0.296706rad)
  Width = 4
FEATURE [Part::Cylinder] Cylinder088
  Angle = 360
  AttacherType = Attacher::AttachEngine3D
  FirstAngle = 0
  Height = 4
  Placement = pos=(154,123,13) rot=(1,0,0;1.5708rad)
  Radius = 1.25
  SecondAngle = 0
FEATURE [Part::Cylinder] Cylinder089
  Angle = 360
  AttacherType = Attacher::AttachEngine3D
  FirstAngle = 0
  Height = 4
  Placement = pos=(154,123,13) rot=(1,0,0;1.5708rad)
  Radius = 2.5
  SecondAngle = 0
FEATURE [Part::MultiFuse] Fusion057
  Refine = true
  Shapes = -> [Box048,Box049,Cylinder089]
FEATURE [Part::Cut] Cut060
  Base = -> Fusion057
  Placement = pos=(0,-21,0) rot=(0,0,1;0rad)
  Refine = true
  Tool = -> Cylinder088
FEATURE [Part::MultiFuse] Fusion059
  Refine = true
  Shapes = -> [Cut058,Cut060]
FEATURE [Part::Cylinder] Cylinder090
  Angle = 180
  AttacherType = Attacher::AttachEngine3D
  FirstAngle = 0
  Height = 48
  Placement = pos=(197,132,-20) rot=(1,0,0;1.5708rad)
  Radius = 50
  SecondAngle = 0
FEATURE [Part::Cut] Cut062
  Base = -> Fusion059
  Refine = true
  Tool = -> Cylinder090
FEATURE [Part::Box] Box051  label="Cube039"
  AttacherType = Attacher::AttachEngine3D
  Height = 52
  Length = 40
  Placement = pos=(141,81.5,-21) rot=(0,0,1;0rad)
  Width = 14
FEATURE [Part::Box] Box052  label="Cube040"
  AttacherType = Attacher::AttachEngine3D
  Height = 15
  Length = 10
  Placement = pos=(153.3,119,13.9) rot=(0,1,0;1.13446rad)
  Width = 4
FEATURE [Part::Box] Box053  label="Cube041"
  AttacherType = Attacher::AttachEngine3D
  Height = 25
  Length = 10
  Placement = pos=(146,119,-10) rot=(0,1,0;0.296706rad)
  Width = 4
FEATURE [Part::Cylinder] Cylinder091
  Angle = 360
  AttacherType = Attacher::AttachEngine3D
  FirstAngle = 0
  Height = 4
  Placement = pos=(154,123,13) rot=(1,0,0;1.5708rad)
  Radius = 2.5
  SecondAngle = 0
FEATURE [Part::MultiFuse] Fusion060
  Refine = true
  Shapes = -> [Box052,Box053,Cylinder091]
FEATURE [Part::Cylinder] Cylinder092
  Angle = 360
  AttacherType = Attacher::AttachEngine3D
  FirstAngle = 0
  Height = 4
  Placement = pos=(154,123,13) rot=(1,0,0;1.5708rad)
  Radius = 1.25
  SecondAngle = 0
FEATURE [Part::Cut] Cut064
  Base = -> Fusion060
  Refine = true
  Tool = -> Cylinder092
FEATURE [Part::Box] Box054  label="Cube042"
  AttacherType = Attacher::AttachEngine3D
  Height = 15
  Length = 10
  Placement = pos=(153.3,119,13.9) rot=(0,1,0;1.13446rad)
  Width = 4
FEATURE [Part::Box] Box055  label="Cube043"
  AttacherType = Attacher::AttachEngine3D
  Height = 25
  Length = 10
  Placement = pos=(146,119,-10) rot=(0,1,0;0.296706rad)
  Width = 4
FEATURE [Part::Cylinder] Cylinder093
  Angle = 360
  AttacherType = Attacher::AttachEngine3D
  FirstAngle = 0
  Height = 4
  Placement = pos=(154,123,13) rot=(1,0,0;1.5708rad)
  Radius = 1.25
  SecondAngle = 0
FEATURE [Part::Cylinder] Cylinder094
  Angle = 360
  AttacherType = Attacher::AttachEngine3D
  FirstAngle = 0
  Height = 4
  Placement = pos=(154,123,13) rot=(1,0,0;1.5708rad)
  Radius = 2.5
  SecondAngle = 0
FEATURE [Part::MultiFuse] Fusion061
  Refine = true
  Shapes = -> [Box054,Box055,Cylinder094]
FEATURE [Part::Cut] Cut065
  Base = -> Fusion061
  Placement = pos=(0,-26,0) rot=(0,0,1;0rad)
  Refine = true
  Tool = -> Cylinder093
FEATURE [Part::MultiFuse] Fusion062
  Refine = true
  Shapes = -> [Cut064,Cut065]
FEATURE [Part::Cylinder] Cylinder095
  Angle = 180
  AttacherType = Attacher::AttachEngine3D
  FirstAngle = 0
  Height = 48
  Placement = pos=(197,132,-20) rot=(1,0,0;1.5708rad)
  Radius = 50
  SecondAngle = 0
FEATURE [Part::Cut] Cut063
  Base = -> Fusion062
  Refine = true
  Tool = -> Cylinder095
FEATURE [Part::Mirroring] Part__Mirroring007  label="Cut063 (Mirror #6)"
  Base = (0,0,0)
  Normal = (1,0,0)
  Placement = pos=(394,0,0) rot=(0,0,1;0rad)
  Source = -> Cut063
FEATURE [Part::Cut] Cut066
  Base = -> Fillet039
  Refine = true
  Tool = -> Box051
FEATURE [Part::Cylinder] Cylinder103
  Angle = 360
  AttacherType = Attacher::AttachEngine3D
  FirstAngle = 0
  Height = 4
  Placement = pos=(154,123,13) rot=(1,0,0;1.5708rad)
  Radius = 1.25
  SecondAngle = 0
FEATURE [Part::Cylinder] Cylinder104
  Angle = 360
  AttacherType = Attacher::AttachEngine3D
  FirstAngle = 0
  Height = 4
  Placement = pos=(154,123,13) rot=(1,0,0;1.5708rad)
  Radius = 2.5
  SecondAngle = 0
FEATURE [Part::Cylinder] Cylinder105
  Angle = 180
  AttacherType = Attacher::AttachEngine3D
  FirstAngle = 0
  Height = 48
  Placement = pos=(197,132,-20) rot=(1,0,0;1.5708rad)
  Radius = 50
  SecondAngle = 0
FEATURE [Part::Box] Box056  label="Cube044"
  AttacherType = Attacher::AttachEngine3D
  Height = 25
  Length = 10
  Placement = pos=(146,119,-10) rot=(0,1,0;0.296706rad)
  Width = 4
FEATURE [Part::Box] Box057  label="Cube045"
  AttacherType = Attacher::AttachEngine3D
  Height = 25
  Length = 10
  Placement = pos=(146,119,-10) rot=(0,1,0;0.296706rad)
  Width = 4
FEATURE [Part::Box] Box058  label="Cube046"
  AttacherType = Attacher::AttachEngine3D
  Height = 15
  Length = 10
  Placement = pos=(153.3,119,13.9) rot=(0,1,0;1.13446rad)
  Width = 4
FEATURE [Part::MultiFuse] Fusion066
  Refine = true
  Shapes = -> [Box058,Box057,Cylinder104]
FEATURE [Part::Cylinder] Cylinder106
  Angle = 360
  AttacherType = Attacher::AttachEngine3D
  FirstAngle = 0
  Height = 4
  Placement = pos=(154,123,13) rot=(1,0,0;1.5708rad)
  Radius = 1.25
  SecondAngle = 0
FEATURE [Part::Cut] Cut072
  Base = -> Fusion066
  Placement = pos=(0,-26,0) rot=(0,0,1;0rad)
  Refine = true
  Tool = -> Cylinder106
FEATURE [Part::Box] Box059  label="Cube047"
  AttacherType = Attacher::AttachEngine3D
  Height = 15
  Length = 10
  Placement = pos=(153.3,119,13.9) rot=(0,1,0;1.13446rad)
  Width = 4
FEATURE [Part::Cylinder] Cylinder107
  Angle = 360
  AttacherType = Attacher::AttachEngine3D
  FirstAngle = 0
  Height = 4
  Placement = pos=(154,123,13) rot=(1,0,0;1.5708rad)
  Radius = 2.5
  SecondAngle = 0
FEATURE [Part::MultiFuse] Fusion067
  Refine = true
  Shapes = -> [Box059,Box056,Cylinder107]
FEATURE [Part::Cut] Cut071
  Base = -> Fusion067
  Refine = true
  Tool = -> Cylinder103
FEATURE [Part::MultiFuse] Fusion068
  Refine = true
  Shapes = -> [Cut071,Cut072]
FEATURE [Part::Cut] Cut070
  Base = -> Fusion068
  Placement = pos=(183,0,0) rot=(0,0,1;0rad)
  Refine = true
  Tool = -> Cylinder105
FEATURE [Part::Box] Box060  label="Cube048"
  AttacherType = Attacher::AttachEngine3D
  Height = 25
  Length = 10
  Placement = pos=(146,119,-10) rot=(0,1,0;0.296706rad)
  Width = 4
FEATURE [Part::Cylinder] Cylinder108
  Angle = 360
  AttacherType = Attacher::AttachEngine3D
  FirstAngle = 0
  Height = 4
  Placement = pos=(154,123,13) rot=(1,0,0;1.5708rad)
  Radius = 1.25
  SecondAngle = 0
FEATURE [Part::Cylinder] Cylinder109
  Angle = 360
  AttacherType = Attacher::AttachEngine3D
  FirstAngle = 0
  Height = 4
  Placement = pos=(154,123,13) rot=(1,0,0;1.5708rad)
  Radius = 2.5
  SecondAngle = 0
FEATURE [Part::Cylinder] Cylinder110
  Angle = 360
  AttacherType = Attacher::AttachEngine3D
  FirstAngle = 0
  Height = 4
  Placement = pos=(154,123,13) rot=(1,0,0;1.5708rad)
  Radius = 2.5
  SecondAngle = 0
FEATURE [Part::Cylinder] Cylinder111
  Angle = 180
  AttacherType = Attacher::AttachEngine3D
  FirstAngle = 0
  Height = 48
  Placement = pos=(197,132,-20) rot=(1,0,0;1.5708rad)
  Radius = 50
  SecondAngle = 0
FEATURE [Part::Box] Box061  label="Cube049"
  AttacherType = Attacher::AttachEngine3D
  Height = 25
  Length = 10
  Placement = pos=(146,119,-10) rot=(0,1,0;0.296706rad)
  Width = 4
FEATURE [Part::Box] Box062  label="Cube050"
  AttacherType = Attacher::AttachEngine3D
  Height = 15
  Length = 10
  Placement = pos=(153.3,119,13.9) rot=(0,1,0;1.13446rad)
  Width = 4
FEATURE [Part::MultiFuse] Fusion069
  Refine = true
  Shapes = -> [Box062,Box061,Cylinder109]
FEATURE [Part::Cylinder] Cylinder112
  Angle = 360
  AttacherType = Attacher::AttachEngine3D
  FirstAngle = 0
  Height = 4
  Placement = pos=(154,123,13) rot=(1,0,0;1.5708rad)
  Radius = 1.25
  SecondAngle = 0
FEATURE [Part::Cut] Cut074
  Base = -> Fusion069
  Placement = pos=(0,-26,0) rot=(0,0,1;0rad)
  Refine = true
  Tool = -> Cylinder112
FEATURE [Part::Box] Box063  label="Cube051"
  AttacherType = Attacher::AttachEngine3D
  Height = 15
  Length = 10
  Placement = pos=(153.3,119,13.9) rot=(0,1,0;1.13446rad)
  Width = 4
FEATURE [Part::MultiFuse] Fusion070
  Refine = true
  Shapes = -> [Box063,Box060,Cylinder110]
FEATURE [Part::Cut] Cut075
  Base = -> Fusion070
  Refine = true
  Tool = -> Cylinder108
FEATURE [Part::MultiFuse] Fusion071
  Refine = true
  Shapes = -> [Cut075,Cut074]
FEATURE [Part::Cut] Cut073
  Base = -> Fusion071
  Placement = pos=(183,0,0) rot=(0,0,1;0rad)
  Refine = true
  Tool = -> Cylinder111
FEATURE [Part::Mirroring] Part__Mirroring008  label="Cut073 (Mirror #7)"
  Base = (0,0,0)
  Normal = (1,0,0)
  Placement = pos=(760,0,0) rot=(0,0,1;0rad)
  Source = -> Cut073
FEATURE [Part::MultiFuse] Fusion072  label="rear-right-wing"
  Placement = pos=(1,0,-4) rot=(0,0,1;0rad)
  Refine = true
  Shapes = -> [Fillet040,Cut070,Part__Mirroring008]
FEATURE [Part::MultiFuse] Fusion073  label="front-right-wing_with_battery_hole_"
  Placement = pos=(0,0,-4) rot=(0,0,1;0rad)
  Refine = true
  Shapes = -> [Cut062,Cut066,Part__Mirroring007]
FEATURE [Part::Cylinder] Cylinder113
  Angle = 180
  AttacherType = Attacher::AttachEngine3D
  FirstAngle = 0
  Height = 48
  Placement = pos=(197,132,-20) rot=(1,0,0;1.5708rad)
  Radius = 50
  SecondAngle = 0
FEATURE [Part::Cylinder] Cylinder114
  Angle = 360
  AttacherType = Attacher::AttachEngine3D
  FirstAngle = 0
  Height = 4
  Placement = pos=(154,123,13) rot=(1,0,0;1.5708rad)
  Radius = 1.25
  SecondAngle = 0
FEATURE [Part::Cylinder] Cylinder115
  Angle = 360
  AttacherType = Attacher::AttachEngine3D
  FirstAngle = 0
  Height = 4
  Placement = pos=(154,123,13) rot=(1,0,0;1.5708rad)
  Radius = 2.5
  SecondAngle = 0
FEATURE [Part::Box] Box064  label="Cube052"
  AttacherType = Attacher::AttachEngine3D
  Height = 25
  Length = 10
  Placement = pos=(146,119,-10) rot=(0,1,0;0.296706rad)
  Width = 4
FEATURE [Part::Box] Box065  label="Cube053"
  AttacherType = Attacher::AttachEngine3D
  Height = 15
  Length = 10
  Placement = pos=(153.3,119,13.9) rot=(0,1,0;1.13446rad)
  Width = 4
FEATURE [Part::MultiFuse] Fusion074
  Refine = true
  Shapes = -> [Box065,Box064,Cylinder115]
FEATURE [Part::Cut] Cut076
  Base = -> Fusion074
  Placement = pos=(0,-26,0) rot=(0,0,1;0rad)
  Refine = true
  Tool = -> Cylinder114
FEATURE [Part::Cylinder] Cylinder116
  Angle = 360
  AttacherType = Attacher::AttachEngine3D
  FirstAngle = 0
  Height = 4
  Placement = pos=(154,123,13) rot=(1,0,0;1.5708rad)
  Radius = 1.25
  SecondAngle = 0
FEATURE [Part::Cylinder] Cylinder117
  Angle = 360
  AttacherType = Attacher::AttachEngine3D
  FirstAngle = 0
  Height = 4
  Placement = pos=(154,123,13) rot=(1,0,0;1.5708rad)
  Radius = 2.5
  SecondAngle = 0
FEATURE [Part::Box] Box066  label="Cube054"
  AttacherType = Attacher::AttachEngine3D
  Height = 25
  Length = 10
  Placement = pos=(146,119,-10) rot=(0,1,0;0.296706rad)
  Width = 4
FEATURE [Part::Box] Box067  label="Cube055"
  AttacherType = Attacher::AttachEngine3D
  Height = 15
  Length = 10
  Placement = pos=(153.3,119,13.9) rot=(0,1,0;1.13446rad)
  Width = 4
FEATURE [Part::MultiFuse] Fusion075
  Refine = true
  Shapes = -> [Box067,Box066,Cylinder117]
FEATURE [Part::Cut] Cut077
  Base = -> Fusion075
  Refine = true
  Tool = -> Cylinder116
FEATURE [Part::MultiFuse] Fusion076
  Refine = true
  Shapes = -> [Cut077,Cut076]
FEATURE [Part::Cut] Cut078
  Base = -> Fusion076
  Placement = pos=(183,0,0) rot=(0,0,1;0rad)
  Refine = true
  Tool = -> Cylinder113
FEATURE [Part::Mirroring] Part__Mirroring009  label="Cut073 (Mirror #7)001"
  Base = (0,0,0)
  Normal = (1,0,0)
  Placement = pos=(760,0,0) rot=(0,0,1;0rad)
  Source = -> Cut078
FEATURE [Part::Cylinder] Cylinder118
  Angle = 180
  AttacherType = Attacher::AttachEngine3D
  FirstAngle = 0
  Height = 48
  Placement = pos=(197,132,-20) rot=(1,0,0;1.5708rad)
  Radius = 50
  SecondAngle = 0
FEATURE [Part::Cylinder] Cylinder119
  Angle = 360
  AttacherType = Attacher::AttachEngine3D
  FirstAngle = 0
  Height = 4
  Placement = pos=(154,123,13) rot=(1,0,0;1.5708rad)
  Radius = 1.25
  SecondAngle = 0
FEATURE [Part::Cylinder] Cylinder120
  Angle = 360
  AttacherType = Attacher::AttachEngine3D
  FirstAngle = 0
  Height = 4
  Placement = pos=(154,123,13) rot=(1,0,0;1.5708rad)
  Radius = 2.5
  SecondAngle = 0
FEATURE [Part::Box] Box068  label="Cube056"
  AttacherType = Attacher::AttachEngine3D
  Height = 25
  Length = 10
  Placement = pos=(146,119,-10) rot=(0,1,0;0.296706rad)
  Width = 4
FEATURE [Part::Box] Box069  label="Cube057"
  AttacherType = Attacher::AttachEngine3D
  Height = 15
  Length = 10
  Placement = pos=(153.3,119,13.9) rot=(0,1,0;1.13446rad)
  Width = 4
FEATURE [Part::MultiFuse] Fusion077
  Refine = true
  Shapes = -> [Box069,Box068,Cylinder120]
FEATURE [Part::Cut] Cut079
  Base = -> Fusion077
  Placement = pos=(0,-26,0) rot=(0,0,1;0rad)
  Refine = true
  Tool = -> Cylinder119
FEATURE [Part::Cylinder] Cylinder121
  Angle = 360
  AttacherType = Attacher::AttachEngine3D
  FirstAngle = 0
  Height = 4
  Placement = pos=(154,123,13) rot=(1,0,0;1.5708rad)
  Radius = 1.25
  SecondAngle = 0
FEATURE [Part::Cylinder] Cylinder122
  Angle = 360
  AttacherType = Attacher::AttachEngine3D
  FirstAngle = 0
  Height = 4
  Placement = pos=(154,123,13) rot=(1,0,0;1.5708rad)
  Radius = 2.5
  SecondAngle = 0
FEATURE [Part::Box] Box070  label="Cube058"
  AttacherType = Attacher::AttachEngine3D
  Height = 25
  Length = 10
  Placement = pos=(146,119,-10) rot=(0,1,0;0.296706rad)
  Width = 4
FEATURE [Part::Box] Box071  label="Cube059"
  AttacherType = Attacher::AttachEngine3D
  Height = 15
  Length = 10
  Placement = pos=(153.3,119,13.9) rot=(0,1,0;1.13446rad)
  Width = 4
FEATURE [Part::MultiFuse] Fusion078
  Refine = true
  Shapes = -> [Box071,Box070,Cylinder122]
FEATURE [Part::Cut] Cut080
  Base = -> Fusion078
  Refine = true
  Tool = -> Cylinder121
FEATURE [Part::MultiFuse] Fusion079
  Refine = true
  Shapes = -> [Cut080,Cut079]
FEATURE [Part::Cut] Cut081
  Base = -> Fusion079
  Placement = pos=(183,0,0) rot=(0,0,1;0rad)
  Refine = true
  Tool = -> Cylinder118
FEATURE [Part::Cylinder] Cylinder123
  Angle = 180
  AttacherType = Attacher::AttachEngine3D
  FirstAngle = 0
  Height = 48
  Placement = pos=(191,132,-20) rot=(1,0,0;1.5708rad)
  Radius = 50
  SecondAngle = 0
FEATURE [Part::Cylinder] Cylinder124
  Angle = 180
  AttacherType = Attacher::AttachEngine3D
  FirstAngle = 0
  Height = 2
  Placement = pos=(191,110,-20) rot=(1,0,0;1.5708rad)
  Radius = 52.5
  SecondAngle = 0
FEATURE [Part::Cylinder] Cylinder125
  Angle = 180
  AttacherType = Attacher::AttachEngine3D
  FirstAngle = 0
  Height = 2
  Placement = pos=(191,123,-20) rot=(1,0,0;1.5708rad)
  Radius = 52.5
  SecondAngle = 0
FEATURE [Part::Cylinder] Cylinder126
  Angle = 180
  AttacherType = Attacher::AttachEngine3D
  FirstAngle = 0
  Height = 2
  Placement = pos=(191,97,-20) rot=(1,0,0;1.5708rad)
  Radius = 52.5
  SecondAngle = 0
FEATURE [Part::MultiFuse] Fusion080
  Placement = pos=(0,-1,0) rot=(0,0,1;0rad)
  Refine = true
  Shapes = -> [Cylinder126,Cylinder125,Cylinder124]
FEATURE [Part::Cut] Cut082
  Base = -> Fusion080
  Refine = true
  Tool = -> Cylinder123
FEATURE [Part::Fillet] Fillet041
  Base = -> Cut082
  Edges = 6 edges r=0.6: [Edge1,Edge3,Edge13,Edge15,Edge25,Edge27]
FEATURE [Part::Cylinder] Cylinder127
  Angle = 180
  AttacherType = Attacher::AttachEngine3D
  FirstAngle = 0
  Height = 48
  Placement = pos=(98,167,-23) rot=(1,0,0;1.5708rad)
  Radius = 50
  SecondAngle = 0
FEATURE [Part::Cylinder] Cylinder128
  Angle = 180
  AttacherType = Attacher::AttachEngine3D
  FirstAngle = 0
  Height = 48
  Placement = pos=(98,168,-27) rot=(1,0,0;1.5708rad)
  Radius = 47
  SecondAngle = 0
FEATURE [Part::Cylinder] Cylinder129
  Angle = 180
  AttacherType = Attacher::AttachEngine3D
  FirstAngle = 0
  Height = 48
  Placement = pos=(98,168,-23) rot=(1,0,0;1.5708rad)
  Radius = 52
  SecondAngle = 0
FEATURE [Part::Cut] Cut083
  Base = -> Cylinder129
  Refine = true
  Tool = -> Cylinder128
FEATURE [Part::Cut] Cut084
  Base = -> Cut083
  Placement = pos=(93,-35.5,3) rot=(0,0,1;0rad)
  Refine = true
  Tool = -> Cylinder127
FEATURE [Part::MultiFuse] Fusion081
  Placement = pos=(189,0,0) rot=(0,0,1;0rad)
  Refine = true
  Shapes = -> [Cut084,Fillet041]
FEATURE [Part::Fillet] Fillet042
  Base = -> Fusion081
  Edges = 2 edges r=2: [Edge2,Edge11]
FEATURE [Part::MultiFuse] Fusion082  label="rear-right-wing001"
  Refine = true
  Shapes = -> [Fillet042,Cut081,Part__Mirroring009]
FEATURE [Part::Mirroring] Part__Mirroring010  label="rear-left-wing"
  Base = (0,0,0)
  Normal = (0,1,0)
  Placement = pos=(1,80,-4) rot=(0,0,1;0rad)
  Source = -> Fusion082
FEATURE [Part::Feature] Part__Mirroring011  label="rear-left-wing001"
  Placement = pos=(-183,80,0) rot=(0,0,1;0rad)
  shape: bbox 113.7 x 48 x 56.83 mm, 62 faces (baked)
FEATURE [Part::Box] Box072  label="Cube060"
  AttacherType = Attacher::AttachEngine3D
  Height = 15
  Length = 10
  Placement = pos=(141,-7.5,-20) rot=(0,0,1;0rad)
  Width = 3
FEATURE [Part::Cut] Cut085  label="front-left-wing"
  Base = -> Part__Mirroring011
  Placement = pos=(0,0,-4) rot=(0,0,1;0rad)
  Refine = true
  Tool = -> Box072
FEATURE [Part::Cylinder] Cylinder130
  Angle = 360
  AttacherType = Attacher::AttachEngine3D
  FirstAngle = 0
  Height = 84
  Placement = pos=(423,82,12.5) rot=(1,0,0;1.5708rad)
  Radius = 1.25
  SecondAngle = 0
FEATURE [Part::Cylinder] Cylinder131
  Angle = 360
  AttacherType = Attacher::AttachEngine3D
  FirstAngle = 0
  Height = 84
  Placement = pos=(337,82,12.5) rot=(1,0,0;1.5708rad)
  Radius = 1.25
  SecondAngle = 0
FEATURE [Part::Cylinder] Cylinder132
  Angle = 360
  AttacherType = Attacher::AttachEngine3D
  FirstAngle = 0
  Height = 84
  Placement = pos=(423,82,12.5) rot=(1,0,0;1.5708rad)
  Radius = 1.25
  SecondAngle = 0
FEATURE [Part::Cylinder] Cylinder133
  Angle = 360
  AttacherType = Attacher::AttachEngine3D
  FirstAngle = 0
  Height = 84
  Placement = pos=(337,82,12.5) rot=(1,0,0;1.5708rad)
  Radius = 1.25
  SecondAngle = 0
FEATURE [Part::MultiFuse] Fusion083
  Placement = pos=(1,0,-4) rot=(0,0,1;0rad)
  Refine = true
  Shapes = -> [Cylinder130,Cylinder131]
FEATURE [Part::MultiFuse] Fusion084
  Placement = pos=(1,0,-4) rot=(0,0,1;0rad)
  Refine = true
  Shapes = -> [Cylinder132,Cylinder133]
FEATURE [Part::Cut] Cut086
  Base = -> Fillet017
  Refine = true
  Tool = -> Fusion083
FEATURE [Part::Cut] Cut087
  Base = -> Part__Mirroring001
  Refine = true
  Tool = -> Fusion084
FEATURE [Part::Cylinder] Cylinder134
  Angle = 360
  AttacherType = Attacher::AttachEngine3D
  FirstAngle = 0
  Height = 3
  Placement = pos=(424,10,8.5) rot=(1,0,0;1.5708rad)
  Radius = 1.25
  SecondAngle = 0
FEATURE [Part::Cylinder] Cylinder135
  Angle = 360
  AttacherType = Attacher::AttachEngine3D
  FirstAngle = 0
  Height = 3
  Placement = pos=(424,73,8.5) rot=(1,0,0;1.5708rad)
  Radius = 1.25
  SecondAngle = 0
FEATURE [Part::MultiFuse] Fusion085
  Refine = true
  Shapes = -> [Cylinder134,Cylinder135]
FEATURE [Part::Cut] Cut088  label="rear-cross-member"
  Base = -> Cut025
  Refine = true
  Tool = -> Fusion085
FEATURE [Part::Cylinder] Cylinder136
  Angle = 360
  AttacherType = Attacher::AttachEngine3D
  FirstAngle = 0
  Height = 5
  Placement = pos=(314,3,1.5) rot=(0,0,1;0rad)
  Radius = 1.5
  SecondAngle = 0
FEATURE [Part::Cylinder] Cylinder137
  Angle = 360
  AttacherType = Attacher::AttachEngine3D
  FirstAngle = 0
  Height = 5
  Placement = pos=(322,3,1.5) rot=(0,0,1;0rad)
  Radius = 1.5
  SecondAngle = 0
FEATURE [Part::Cylinder] Cylinder138
  Angle = 360
  AttacherType = Attacher::AttachEngine3D
  FirstAngle = 0
  Height = 5
  Placement = pos=(314,3,1.5) rot=(0,0,1;0rad)
  Radius = 1.5
  SecondAngle = 0
FEATURE [Part::Cylinder] Cylinder139
  Angle = 360
  AttacherType = Attacher::AttachEngine3D
  FirstAngle = 0
  Height = 5
  Placement = pos=(322,3,1.5) rot=(0,0,1;0rad)
  Radius = 1.5
  SecondAngle = 0
FEATURE [Part::MultiFuse] Fusion086
  Refine = true
  Shapes = -> [Cylinder136,Cylinder137]
FEATURE [Part::MultiFuse] Fusion087
  Placement = pos=(0,74,0) rot=(0,0,1;0rad)
  Refine = true
  Shapes = -> [Cylinder138,Cylinder139]
FEATURE [Part::Cut] Cut089  label="rear-right-cross-member"
  Base = -> Cut086
  Refine = true
  Tool = -> Fusion087
FEATURE [Part::Cut] Cut090  label="rear-left-cross-member"
  Base = -> Cut087
  Refine = true
  Tool = -> Fusion086
FEATURE [Part::Cylinder] Cylinder140
  Angle = 360
  AttacherType = Attacher::AttachEngine3D
  FirstAngle = 0
  Height = 84
  Placement = pos=(337,82,12.5) rot=(1,0,0;1.5708rad)
  Radius = 1.25
  SecondAngle = 0
FEATURE [Part::Cylinder] Cylinder141
  Angle = 360
  AttacherType = Attacher::AttachEngine3D
  FirstAngle = 0
  Height = 84
  Placement = pos=(423,82,12.5) rot=(1,0,0;1.5708rad)
  Radius = 1.25
  SecondAngle = 0
FEATURE [Part::MultiFuse] Fusion088
  Placement = pos=(-183,51,-4) rot=(0,0,1;0rad)
  Refine = true
  Shapes = -> [Cylinder141,Cylinder140]
FEATURE [Part::Box] Box073  label="Cube061"
  AttacherType = Attacher::AttachEngine3D
  Height = 4
  Length = 16
  Placement = pos=(0,72.5,-4) rot=(0,0,1;0rad)
  Width = 12
FEATURE [Part::Box] Box074  label="Cube062"
  AttacherType = Attacher::AttachEngine3D
  Height = 20
  Length = 16
  Placement = pos=(0,81.5,0) rot=(0,0,1;0rad)
  Width = 3
FEATURE [Part::Box] Box075  label="Cube063"
  AttacherType = Attacher::AttachEngine3D
  Height = 4
  Length = 16
  Placement = pos=(0,72.5,20) rot=(0,0,1;0rad)
  Width = 12
FEATURE [Part::MultiFuse] Fusion089
  Placement = pos=(232,0,0) rot=(0,0,1;0rad)
  Refine = true
  Shapes = -> [Box073,Box075,Box074]
FEATURE [Part::Box] Box076  label="Cube064"
  AttacherType = Attacher::AttachEngine3D
  Height = 4
  Length = 16
  Placement = pos=(0,72.5,20) rot=(0,0,1;0rad)
  Width = 12
FEATURE [Part::Box] Box077  label="Cube065"
  AttacherType = Attacher::AttachEngine3D
  Height = 20
  Length = 16
  Placement = pos=(0,81.5,0) rot=(0,0,1;0rad)
  Width = 3
FEATURE [Part::Box] Box078  label="Cube066"
  AttacherType = Attacher::AttachEngine3D
  Height = 4
  Length = 16
  Placement = pos=(0,72.5,-4) rot=(0,0,1;0rad)
  Width = 12
FEATURE [Part::MultiFuse] Fusion090
  Placement = pos=(146,0,0) rot=(0,0,1;0rad)
  Refine = true
  Shapes = -> [Box078,Box076,Box077]
FEATURE [Part::Box] Box079  label="Cube067"
  AttacherType = Attacher::AttachEngine3D
  Height = 20
  Length = 70
  Placement = pos=(162,81.5,0) rot=(0,0,1;0rad)
  Width = 3
FEATURE [Part::MultiFuse] Fusion091
  Refine = true
  Shapes = -> [Fusion089,Fusion090,Box079]
FEATURE [Part::Cylinder] Cylinder143
  Angle = 360
  AttacherType = Attacher::AttachEngine3D
  FirstAngle = 0
  Height = 84
  Placement = pos=(154,133,16) rot=(1,0,0;1.5708rad)
  Radius = 1.25
  SecondAngle = 0
FEATURE [Part::MultiFuse] Fusion092
  Refine = true
  Shapes = -> [Cylinder143,Fusion088]
FEATURE [Part::Cut] Cut091  label="front-fender-holes"
  Base = -> Fusion091
  Refine = true
  Tool = -> Fusion092
FEATURE [Part::Box] Box080  label="Cube068"
  AttacherType = Attacher::AttachEngine3D
  Height = 17
  Length = 8
  Placement = pos=(230,16,1.5) rot=(0,0,1;0rad)
  Width = 8.5
FEATURE [Part::Fillet] Fillet043
  Base = -> Box080
  Edges = 2 edges r=3: [Edge9,Edge10]
  Placement = pos=(-80,0,0) rot=(0,0,1;0rad)
FEATURE [Part::Cylinder] Cylinder144
  Angle = 360
  AttacherType = Attacher::AttachEngine3D
  FirstAngle = 0
  Height = 84
  Placement = pos=(154,133,16) rot=(1,0,0;1.5708rad)
  Radius = 1.25
  SecondAngle = 0
FEATURE [Part::Cylinder] Cylinder145
  Angle = 360
  AttacherType = Attacher::AttachEngine3D
  FirstAngle = 0
  Height = 84
  Placement = pos=(337,82,12.5) rot=(1,0,0;1.5708rad)
  Radius = 1.25
  SecondAngle = 0
FEATURE [Part::Cylinder] Cylinder146
  Angle = 360
  AttacherType = Attacher::AttachEngine3D
  FirstAngle = 0
  Height = 84
  Placement = pos=(423,82,12.5) rot=(1,0,0;1.5708rad)
  Radius = 1.25
  SecondAngle = 0
FEATURE [Part::MultiFuse] Fusion094
  Placement = pos=(-183,51,-4) rot=(0,0,1;0rad)
  Refine = true
  Shapes = -> [Cylinder146,Cylinder145]
FEATURE [Part::MultiFuse] Fusion093
  Placement = pos=(0,-36,0) rot=(0,0,1;0rad)
  Refine = true
  Shapes = -> [Cylinder144,Fusion094]
FEATURE [Part::Cut] Cut092  label="front-fender-mount"
  Base = -> Fillet043
  Placement = pos=(0,-16,0) rot=(0,0,1;0rad)
  Refine = true
  Tool = -> Fusion093
FEATURE [Part::Box] Box081  label="Cube069"
  AttacherType = Attacher::AttachEngine3D
  Height = 10
  Length = 24
  Placement = pos=(310,-1.5,0) rot=(0,0,1;0rad)
  Width = 10
FEATURE [Part::Fillet] Fillet044
  Base = -> Box081
  Edges = 1 edges r=3: [Edge9]
FEATURE [Part::Box] Box082  label="Cube070"
  AttacherType = Attacher::AttachEngine3D
  Height = 10
  Length = 24
  Placement = pos=(310,-1.5,-2.5) rot=(0,0,1;0rad)
  Width = 3
FEATURE [Part::Box] Box083  label="Cube071"
  AttacherType = Attacher::AttachEngine3D
  Height = 1
  Length = 8
  Placement = pos=(326,-1.5,-2.5) rot=(0,0,1;0rad)
  Width = 3
FEATURE [Part::Cut] Cut093
  Base = -> Box082
  Refine = true
  Tool = -> Box083
FEATURE [Part::Cut] Cut094
  Base = -> Cut093
  Refine = true
  Tool = -> Fillet044
FEATURE [Part::Cylinder] Cylinder147
  Angle = 360
  AttacherType = Attacher::AttachEngine3D
  FirstAngle = 0
  Height = 10
  Placement = pos=(322,3,-5) rot=(0,0,1;0rad)
  Radius = 1.6
  SecondAngle = 0
FEATURE [Part::Cylinder] Cylinder148
  Angle = 360
  AttacherType = Attacher::AttachEngine3D
  FirstAngle = 0
  Height = 10
  Placement = pos=(314,3,-5) rot=(0,0,1;0rad)
  Radius = 1.6
  SecondAngle = 0
FEATURE [Part::MultiFuse] Fusion095
  Refine = true
  Shapes = -> [Cylinder148,Cylinder147]
FEATURE [Part::Cut] Cut095
  Base = -> Cut094
  Refine = true
  Tool = -> Fusion095
FEATURE [Part::Box] Box084  label="Cube072"
  AttacherType = Attacher::AttachEngine3D
  Height = 10
  Length = 24
  Placement = pos=(310,-1.5,2) rot=(0,0,1;0rad)
  Width = 3
FEATURE [Part::Cut] Cut096
  Base = -> Cut095
  Refine = true
  Tool = -> Box084
FEATURE [Part::Mirroring] Part__Mirroring012  label="Cut096 (Mirror #10)"
  Base = (0,0,0)
  Normal = (0,1,0)
  Placement = pos=(0,80,0) rot=(0,0,1;0rad)
  Source = -> Cut096
FEATURE [Part::Box] Box085  label="Cube073"
  AttacherType = Attacher::AttachEngine3D
  Height = 10
  Length = 24
  Placement = pos=(310,-1.5,2) rot=(0,0,1;0rad)
  Width = 3
FEATURE [Part::Box] Box086  label="Cube074"
  AttacherType = Attacher::AttachEngine3D
  Height = 10
  Length = 24
  Placement = pos=(310,-1.5,0) rot=(0,0,1;0rad)
  Width = 10
FEATURE [Part::Fillet] Fillet045
  Base = -> Box086
  Edges = 1 edges r=3: [Edge9]
FEATURE [Part::Box] Box087  label="Cube075"
  AttacherType = Attacher::AttachEngine3D
  Height = 10
  Length = 24
  Placement = pos=(310,-1.5,-2.5) rot=(0,0,1;0rad)
  Width = 3
FEATURE [Part::Box] Box088  label="Cube076"
  AttacherType = Attacher::AttachEngine3D
  Height = 1
  Length = 8
  Placement = pos=(326,-1.5,-2.5) rot=(0,0,1;0rad)
  Width = 3
FEATURE [Part::Cut] Cut099
  Base = -> Box087
  Refine = true
  Tool = -> Box088
FEATURE [Part::Cut] Cut098
  Base = -> Cut099
  Refine = true
  Tool = -> Fillet045
FEATURE [Part::Cylinder] Cylinder149
  Angle = 360
  AttacherType = Attacher::AttachEngine3D
  FirstAngle = 0
  Height = 10
  Placement = pos=(322,3,-5) rot=(0,0,1;0rad)
  Radius = 1.6
  SecondAngle = 0
FEATURE [Part::Cylinder] Cylinder150
  Angle = 360
  AttacherType = Attacher::AttachEngine3D
  FirstAngle = 0
  Height = 10
  Placement = pos=(314,3,-5) rot=(0,0,1;0rad)
  Radius = 1.6
  SecondAngle = 0
FEATURE [Part::MultiFuse] Fusion096
  Refine = true
  Shapes = -> [Cylinder150,Cylinder149]
FEATURE [Part::Cut] Cut100
  Base = -> Cut098
  Refine = true
  Tool = -> Fusion096
FEATURE [Part::Cut] Cut097
  Base = -> Cut100
  Refine = true
  Tool = -> Box085
FEATURE [Part::Box] Box089
  AttacherType = Attacher::AttachEngine3D
  Height = 2.5
  Length = 67
  Placement = pos=(293,-5,20) rot=(0,0,1;0rad)
  Width = 90
FEATURE [Part::Box] Box090
  AttacherType = Attacher::AttachEngine3D
  Height = 1.5
  Length = 30
  Placement = pos=(302,9.5,18.5) rot=(0,0,1;0rad)
  Width = 61
FEATURE [Part::Cylinder] Cylinder151
  Angle = 360
  AttacherType = Attacher::AttachEngine3D
  FirstAngle = 0
  Height = 10
  Placement = pos=(310.5,21,13) rot=(0,0,1;0rad)
  Radius = 1.75
  SecondAngle = 0
FEATURE [Part::Cylinder] Cylinder153
  Angle = 360
  AttacherType = Attacher::AttachEngine3D
  FirstAngle = 0
  Height = 10
  Placement = pos=(300,4,13) rot=(0,0,1;0rad)
  Radius = 1.6
  SecondAngle = 0
FEATURE [Part::Cylinder] Cylinder154
  Angle = 360
  AttacherType = Attacher::AttachEngine3D
  FirstAngle = 0
  Height = 10
  Placement = pos=(300,76,13) rot=(0,0,1;0rad)
  Radius = 1.6
  SecondAngle = 0
FEATURE [Part::MultiFuse] Fusion
  Placement = pos=(-1.5,0,0) rot=(0,0,1;0rad)
  Refine = true
  Shapes = -> [Cylinder153,Cylinder154]
FEATURE [Part::Cylinder] Cylinder159
  Angle = 360
  AttacherType = Attacher::AttachEngine3D
  FirstAngle = 0
  Height = 20
  Placement = pos=(317,56,10) rot=(0,1,0;1.5708rad)
  Radius = 1.6
  SecondAngle = 0
FEATURE [Part::Cylinder] Cylinder160
  Angle = 360
  AttacherType = Attacher::AttachEngine3D
  FirstAngle = 0
  Height = 20
  Placement = pos=(317,24,10) rot=(0,1,0;1.5708rad)
  Radius = 1.6
  SecondAngle = 0
FEATURE [Part::MultiFuse] Fusion105
  Refine = true
  Shapes = -> [Cylinder159,Cylinder160]
FEATURE [Part::Cylinder] Cylinder163
  Angle = 360
  AttacherType = Attacher::AttachEngine3D
  FirstAngle = 0
  Height = 1.5
  Placement = pos=(300,4,13) rot=(0,0,1;0rad)
  Radius = 3.1
  SecondAngle = 0
FEATURE [Part::Cylinder] Cylinder164
  Angle = 360
  AttacherType = Attacher::AttachEngine3D
  FirstAngle = 0
  Height = 1.5
  Placement = pos=(300,76,13) rot=(0,0,1;0rad)
  Radius = 3.1
  SecondAngle = 0
FEATURE [Part::MultiFuse] Fusion107
  Placement = pos=(-1.5,0,8.5) rot=(0,0,1;0rad)
  Refine = true
  Shapes = -> [Cylinder163,Cylinder164]
FEATURE [Part::Cut] Cut105
  Base = -> Cut027
  Refine = true
  Tool = -> Fusion105
FEATURE [Part::Cylinder] Cylinder165
  Angle = 360
  AttacherType = Attacher::AttachEngine3D
  FirstAngle = 0
  Height = 10
  Placement = pos=(325,13,13) rot=(0,0,1;0rad)
  Radius = 1.6
  SecondAngle = 0
FEATURE [Part::Cylinder] Cylinder166
  Angle = 360
  AttacherType = Attacher::AttachEngine3D
  FirstAngle = 0
  Height = 10
  Placement = pos=(325,13,13) rot=(0,0,1;0rad)
  Radius = 1.6
  SecondAngle = 0
FEATURE [Part::Cylinder] Cylinder167
  Angle = 360
  AttacherType = Attacher::AttachEngine3D
  FirstAngle = 0
  Height = 1.5
  Placement = pos=(325,13,21.5) rot=(0,0,1;0rad)
  Radius = 3.1
  SecondAngle = 0
FEATURE [Part::Cylinder] Cylinder168
  Angle = 360
  AttacherType = Attacher::AttachEngine3D
  FirstAngle = 0
  Height = 1.5
  Placement = pos=(325,13,21.5) rot=(0,0,1;0rad)
  Radius = 3.1
  SecondAngle = 0
FEATURE [Part::MultiFuse] Fusion109
  Refine = true
  Shapes = -> [Cylinder165,Cylinder167]
FEATURE [Part::MultiFuse] Fusion110
  Placement = pos=(0,54,0) rot=(0,0,1;0rad)
  Refine = true
  Shapes = -> [Cylinder166,Cylinder168]
FEATURE [Part::MultiFuse] Fusion111
  Placement = pos=(2.5,0,0) rot=(0,0,1;0rad)
  Refine = true
  Shapes = -> [Fusion109,Fusion110]
FEATURE [Part::Cylinder] Cylinder169
  Angle = 360
  AttacherType = Attacher::AttachEngine3D
  FirstAngle = 0
  Height = 10
  Placement = pos=(327.5,13,9) rot=(0,0,1;0rad)
  Radius = 1.25
  SecondAngle = 0
FEATURE [Part::Cylinder] Cylinder170
  Angle = 360
  AttacherType = Attacher::AttachEngine3D
  FirstAngle = 0
  Height = 10
  Placement = pos=(327.5,67,9) rot=(0,0,1;0rad)
  Radius = 1.25
  SecondAngle = 0
FEATURE [Part::MultiFuse] Fusion112
  Refine = true
  Shapes = -> [Cylinder169,Cylinder170]
FEATURE [Part::Cut] Cut107  label="middle-cross-member"
  Base = -> Cut105
  Refine = true
  Tool = -> Fusion112
FEATURE [Part::Cylinder] Cylinder152
  Angle = 360
  AttacherType = Attacher::AttachEngine3D
  FirstAngle = 0
  Height = 10
  Placement = pos=(310.5,59,13) rot=(0,0,1;0rad)
  Radius = 1.75
  SecondAngle = 0
FEATURE [Part::Cylinder] Cylinder171
  Angle = 360
  AttacherType = Attacher::AttachEngine3D
  FirstAngle = 0
  Height = 2
  Placement = pos=(310.5,21,17) rot=(0,0,1;0rad)
  Radius = 4
  SecondAngle = 0
FEATURE [Part::Cylinder] Cylinder172
  Angle = 360
  AttacherType = Attacher::AttachEngine3D
  FirstAngle = 0
  Height = 2
  Placement = pos=(310.5,59,17) rot=(0,0,1;0rad)
  Radius = 4
  SecondAngle = 0
FEATURE [Part::MultiFuse] Fusion114
  Refine = true
  Shapes = -> [Cylinder152,Cylinder151]
FEATURE [Part::MultiFuse] Fusion115
  Refine = true
  Shapes = -> [Box090,Cylinder172,Cylinder171]
FEATURE [Part::Box] Box091  label="Cube077"
  AttacherType = Attacher::AttachEngine3D
  Height = 10
  Length = 12
  Placement = pos=(292,14,17.5) rot=(0,0,1;0rad)
  Width = 12
FEATURE [Part::Box] Box092  label="Cube078"
  AttacherType = Attacher::AttachEngine3D
  Height = 2.5
  Length = 23
  Placement = pos=(293,81.5,20) rot=(0,0,1;0.20944rad)
  Width = 12
FEATURE [Part::Box] Box093  label="Cube079"
  AttacherType = Attacher::AttachEngine3D
  Height = 2.5
  Length = 24
  Placement = pos=(293,78,20) rot=(0,0,1;0rad)
  Width = 3.5
FEATURE [Part::Box] Box094  label="Cube080"
  AttacherType = Attacher::AttachEngine3D
  Height = 2.5
  Length = 25
  Placement = pos=(293,81.5,20) rot=(0,0,-1;0.20944rad)
  Width = 12
FEATURE [Part::Cut] Cut
  Base = -> Box093
  Placement = pos=(0,-83,0) rot=(0,0,1;0rad)
  Refine = true
  Tool = -> Box094
FEATURE [Part::MultiFuse] Fusion116
  Refine = true
  Shapes = -> [Box092,Cut]
FEATURE [Part::Cut] Cut108
  Base = -> Box089
  Refine = true
  Tool = -> Fusion116
FEATURE [Part::Fillet] Fillet046
  Base = -> Cut108
  Edges = 4 edges r=3: [Edge1,Edge3,Edge6,Edge13]
FEATURE [Part::Fillet] Fillet047
  Base = -> Fillet046
  Edges = 2 edges r=8: [Edge29,Edge30]
FEATURE [Part::MultiFuse] Fusion117
  Refine = true
  Shapes = -> [Fusion115,Fillet047]
FEATURE [Part::Cut] Cut109
  Base = -> Fusion117
  Refine = true
  Tool = -> Fusion114
FEATURE [Part::MultiFuse] Fusion118
  Refine = true
  Shapes = -> [Fusion107,Fusion]
FEATURE [Part::MultiFuse] Fusion119
  Refine = true
  Shapes = -> [Fusion118,Fusion111]
FEATURE [Part::Cut] Cut110
  Base = -> Cut109
  Refine = true
  Tool = -> Fusion119
FEATURE [Part::Cut] Cut111
  Base = -> Cut110
  Refine = true
  Tool = -> Box091
FEATURE [Part::Fillet] Fillet048  label="fifth-wheel-mount"
  Base = -> Cut111
  Edges = 4 edges r=3: [Edge42,Edge43,Edge45,Edge46]
FEATURE [Part::MultiFuse] Fusion120  label="rear-left-ls-mount"
  Placement = pos=(0,-0.5,0) rot=(0,0,1;0rad)
  Refine = true
  Shapes = -> [Fillet031,Cut097]
FEATURE [Part::MultiFuse] Fusion121  label="rear-right-ls-mount"
  Placement = pos=(0,0.5,0) rot=(0,0,1;0rad)
  Refine = true
  Shapes = -> [Part__Mirroring004,Part__Mirroring012]
FEATURE [Part::Box] Box095  label="Cube081"
  AttacherType = Attacher::AttachEngine3D
  Height = 22
  Length = 55
  Placement = pos=(250,-44,-4) rot=(0,0,1;0rad)
  Width = 40
FEATURE [Part::Cylinder] Cylinder173
  Angle = 360
  AttacherType = Attacher::AttachEngine3D
  FirstAngle = 0
  Height = 42
  Placement = pos=(321,-4,9) rot=(1,0,0;1.5708rad)
  Radius = 10
  SecondAngle = 0
FEATURE [Part::Box] Box096  label="Cube082"
  AttacherType = Attacher::AttachEngine3D
  Height = 20
  Length = 52
  Placement = pos=(251.5,-44,-2) rot=(0,0,1;0rad)
  Width = 36
FEATURE [Part::Cut] Cut112
  Base = -> Box095
  Refine = true
  Tool = -> Box096
FEATURE [Part::Box] Box097  label="Cube083"
  AttacherType = Attacher::AttachEngine3D
  Height = 13
  Length = 40
  Placement = pos=(257.5,-4,3) rot=(0,0,1;0rad)
  Width = 2.5
FEATURE [Part::MultiFuse] Fusion122
  Refine = true
  Shapes = -> [Cut112,Box097]
FEATURE [Part::Cylinder] Cylinder174
  Angle = 360
  AttacherType = Attacher::AttachEngine3D
  FirstAngle = 0
  Height = 42
  Placement = pos=(317,-4,-13) rot=(1,0,0;1.5708rad)
  Radius = 10
  SecondAngle = 0
FEATURE [Part::Box] Box098  label="Cube084"
  AttacherType = Attacher::AttachEngine3D
  Height = 22
  Length = 58
  Placement = pos=(248.5,-45.5,-2.5) rot=(0,0,1;0rad)
  Width = 41.5
FEATURE [Part::Box] Box099  label="Cube085"
  AttacherType = Attacher::AttachEngine3D
  Height = 22.5
  Length = 56
  Placement = pos=(249.5,-44.5,-4) rot=(0,0,1;0rad)
  Width = 40.5
FEATURE [Part::Cut] Cut113
  Base = -> Box098
  Refine = true
  Tool = -> Box099
FEATURE [Part::Box] Box100  label="Cube086"
  AttacherType = Attacher::AttachEngine3D
  Height = 22.5
  Length = 1
  Placement = pos=(248.5,-43.5,-2.5) rot=(1,0,0;0.436332rad)
  Width = 46.5
FEATURE [Part::Box] Box101  label="Cube087"
  AttacherType = Attacher::AttachEngine3D
  Height = 19.5
  Length = 1
  Placement = pos=(248.5,-43.5,-2.5) rot=(0,0,1;0rad)
  Width = 46.5
FEATURE [Part::Cut] Cut114
  Base = -> Box101
  Refine = true
  Tool = -> Box100
FEATURE [Part::Box] Box102  label="Cube088"
  AttacherType = Attacher::AttachEngine3D
  Height = 19.5
  Length = 1
  Placement = pos=(248.5,-43.5,-2.5) rot=(0,0,1;0rad)
  Width = 46.5
FEATURE [Part::Box] Box103  label="Cube089"
  AttacherType = Attacher::AttachEngine3D
  Height = 22.5
  Length = 1
  Placement = pos=(248.5,-43.5,-2.5) rot=(1,0,0;0.436332rad)
  Width = 46.5
FEATURE [Part::Cut] Cut115
  Base = -> Box102
  Placement = pos=(57,0,0) rot=(0,0,1;0rad)
  Refine = true
  Tool = -> Box103
FEATURE [Part::MultiFuse] Fusion123
  Refine = true
  Shapes = -> [Cut115,Cut114]
FEATURE [Part::Chamfer] Chamfer
  Base = -> Fusion122
  Edges = 1 edges r=2.49: [Edge6]
FEATURE [Part::Fillet] Fillet049
  Base = -> Chamfer
  Edges = 1 edges r=1.99: [Edge21]
FEATURE [Part::Cut] Cut116
  Base = -> Cut113
  Refine = true
  Tool = -> Fusion123
FEATURE [Part::Cylinder] Cylinder175
  Angle = 360
  AttacherType = Attacher::AttachEngine3D
  FirstAngle = 0
  Height = 65
  Placement = pos=(245,-6,16) rot=(0,1,0;1.5708rad)
  Radius = 0.55
  SecondAngle = 0
FEATURE [Part::Box] Box104  label="Cube090"
  AttacherType = Attacher::AttachEngine3D
  Height = 5
  Length = 55
  Placement = pos=(250,-44,-4) rot=(0,0,1;0rad)
  Width = 1.5
FEATURE [Part::MultiFuse] Fusion124
  Refine = true
  Shapes = -> [Box104,Fillet049]
FEATURE [Part::Cylinder] Cylinder176
  Angle = 360
  AttacherType = Attacher::AttachEngine3D
  FirstAngle = 0
  Height = 65
  Placement = pos=(245,-6,16) rot=(0,1,0;1.5708rad)
  Radius = 0.55
  SecondAngle = 0
FEATURE [Part::Cut] Cut117
  Base = -> Fusion124
  Refine = true
  Tool = -> Cylinder176
FEATURE [Part::Cylinder] Cylinder177
  Angle = 360
  AttacherType = Attacher::AttachEngine3D
  FirstAngle = 0
  Height = 1
  Placement = pos=(305.5,-6,16) rot=(0,1,0;1.5708rad)
  Radius = 2
  SecondAngle = 0
FEATURE [Part::Cylinder] Cylinder178
  Angle = 360
  AttacherType = Attacher::AttachEngine3D
  FirstAngle = 0
  Height = 1
  Placement = pos=(248.5,-6,16) rot=(0,1,0;1.5708rad)
  Radius = 2
  SecondAngle = 0
FEATURE [Part::MultiFuse] Fusion125
  Refine = true
  Shapes = -> [Cylinder177,Cylinder178,Cut116]
FEATURE [Part::Cut] Cut118
  Base = -> Fusion125
  Refine = true
  Tool = -> Cylinder175
FEATURE [Part::Cylinder] Cylinder179
  Angle = 360
  AttacherType = Attacher::AttachEngine3D
  FirstAngle = 0
  Height = 22
  Placement = pos=(277.5,-45,-2.5) rot=(0,0,1;0rad)
  Radius = 1
  SecondAngle = 0
FEATURE [Part::Cylinder] Cylinder180
  Angle = 360
  AttacherType = Attacher::AttachEngine3D
  FirstAngle = 0
  Height = 58
  Placement = pos=(248.5,-45.5,2) rot=(0,1,0;1.5708rad)
  Radius = 1
  SecondAngle = 0
FEATURE [Part::Cylinder] Cylinder181
  Angle = 360
  AttacherType = Attacher::AttachEngine3D
  FirstAngle = 0
  Height = 58
  Placement = pos=(248.5,-45.5,15) rot=(0,1,0;1.5708rad)
  Radius = 1
  SecondAngle = 0
FEATURE [Part::Cylinder] Cylinder182
  Angle = 360
  AttacherType = Attacher::AttachEngine3D
  FirstAngle = 0
  Height = 22
  Placement = pos=(303.5,-45,-2.5) rot=(0,0,1;0rad)
  Radius = 1
  SecondAngle = 0
FEATURE [Part::Cylinder] Cylinder183
  Angle = 360
  AttacherType = Attacher::AttachEngine3D
  FirstAngle = 0
  Height = 22
  Placement = pos=(251.5,-45,-2.5) rot=(0,0,1;0rad)
  Radius = 1
  SecondAngle = 0
FEATURE [Part::Cylinder] Cylinder184
  Angle = 360
  AttacherType = Attacher::AttachEngine3D
  FirstAngle = 0
  Height = 41.5
  Placement = pos=(251.5,-4,19) rot=(1,0,0;1.5708rad)
  Radius = 1
  SecondAngle = 0
FEATURE [Part::MultiFuse] Fusion126
  Placement = pos=(0,0.25,0) rot=(0,0,1;0rad)
  Refine = true
  Shapes = -> [Cylinder183,Cylinder182,Cylinder179,Cylinder180,Cylinder181]
FEATURE [Part::MultiFuse] Fusion127
  Refine = true
  Shapes = -> [Fusion126,Cut118]
FEATURE [Part::Cylinder] Cylinder186
  Angle = 360
  AttacherType = Attacher::AttachEngine3D
  FirstAngle = 0
  Height = 36.5
  Placement = pos=(306.25,-9,15) rot=(1,0,0;1.5708rad)
  Radius = 1
  SecondAngle = 0
FEATURE [Part::Cylinder] Cylinder187
  Angle = 360
  AttacherType = Attacher::AttachEngine3D
  FirstAngle = 0
  Height = 36.5
  Placement = pos=(248.75,-9,15) rot=(1,0,0;1.5708rad)
  Radius = 1
  SecondAngle = 0
FEATURE [Part::Cylinder] Cylinder188
  Angle = 360
  AttacherType = Attacher::AttachEngine3D
  FirstAngle = 0
  Height = 8.5
  Placement = pos=(306.25,-37,2) rot=(1,0,0;1.5708rad)
  Radius = 1
  SecondAngle = 0
FEATURE [Part::Cylinder] Cylinder189
  Angle = 360
  AttacherType = Attacher::AttachEngine3D
  FirstAngle = 0
  Height = 8.5
  Placement = pos=(248.75,-37,2) rot=(1,0,0;1.5708rad)
  Radius = 1
  SecondAngle = 0
FEATURE [Part::MultiFuse] Fusion128
  Refine = true
  Shapes = -> [Cylinder186,Cylinder188,Cylinder187,Cylinder189]
FEATURE [Part::MultiFuse] Fusion129
  Refine = true
  Shapes = -> [Fusion127,Fusion128]
FEATURE [Part::Cylinder] Cylinder190
  Angle = 360
  AttacherType = Attacher::AttachEngine3D
  FirstAngle = 0
  Height = 41.5
  Placement = pos=(277.5,-4,19) rot=(1,0,0;1.5708rad)
  Radius = 1
  SecondAngle = 0
FEATURE [Part::Cylinder] Cylinder191
  Angle = 360
  AttacherType = Attacher::AttachEngine3D
  FirstAngle = 0
  Height = 41.5
  Placement = pos=(303.5,-4,19) rot=(1,0,0;1.5708rad)
  Radius = 1
  SecondAngle = 0
FEATURE [Part::Cylinder] Cylinder192
  Angle = 360
  AttacherType = Attacher::AttachEngine3D
  FirstAngle = 0
  Height = 58
  Placement = pos=(248.5,-39,19) rot=(0,1,0;1.5708rad)
  Radius = 1
  SecondAngle = 0
FEATURE [Part::Cylinder] Cylinder193
  Angle = 360
  AttacherType = Attacher::AttachEngine3D
  FirstAngle = 0
  Height = 58
  Placement = pos=(248.5,-10,19) rot=(0,1,0;1.5708rad)
  Radius = 1
  SecondAngle = 0
FEATURE [Part::Cylinder] Cylinder194
  Angle = 360
  AttacherType = Attacher::AttachEngine3D
  FirstAngle = 0
  Height = 4.5
  Placement = pos=(249,-10,15) rot=(0,0,1;0rad)
  Radius = 1
  SecondAngle = 0
FEATURE [Part::Cylinder] Cylinder195
  Angle = 360
  AttacherType = Attacher::AttachEngine3D
  FirstAngle = 0
  Height = 19.5
  Placement = pos=(249,-39,0) rot=(0,0,1;0rad)
  Radius = 1
  SecondAngle = 0
FEATURE [Part::Cylinder] Cylinder196
  Angle = 360
  AttacherType = Attacher::AttachEngine3D
  FirstAngle = 0
  Height = 4.5
  Placement = pos=(306,-10,15) rot=(0,0,1;0rad)
  Radius = 1
  SecondAngle = 0
FEATURE [Part::Cylinder] Cylinder197
  Angle = 360
  AttacherType = Attacher::AttachEngine3D
  FirstAngle = 0
  Height = 19.5
  Placement = pos=(306,-39,0) rot=(0,0,1;0rad)
  Radius = 1
  SecondAngle = 0
FEATURE [Part::MultiFuse] Fusion130
  Refine = true
  Shapes = -> [Fusion129,Cylinder194,Cylinder195,Cylinder196,Cylinder197]
FEATURE [Part::MultiFuse] Fusion131
  Refine = true
  Shapes = -> [Cylinder184,Cylinder190,Cylinder191,Cylinder192,Cylinder193]
FEATURE [Part::Box] Box105  label="Cube091"
  AttacherType = Attacher::AttachEngine3D
  Height = 22
  Length = 58
  Placement = pos=(248.5,-45.5,-2.5) rot=(0,0,1;0rad)
  Width = 41.5
FEATURE [Part::Cut] Cut119  label="battery-box-cover-texture"
  Base = -> Fusion131
  Refine = true
  Tool = -> Box105
FEATURE [Part::Cylinder] Cylinder198
  Angle = 360
  AttacherType = Attacher::AttachEngine3D
  FirstAngle = 0
  Height = 40
  Placement = pos=(261,1,10) rot=(1,0,0;1.5708rad)
  Radius = 1.6
  SecondAngle = 0
FEATURE [Part::Cylinder] Cylinder199
  Angle = 360
  AttacherType = Attacher::AttachEngine3D
  FirstAngle = 0
  Height = 40
  Placement = pos=(294,1,10) rot=(1,0,0;1.5708rad)
  Radius = 1.6
  SecondAngle = 0
FEATURE [Part::MultiFuse] Fusion132
  Refine = true
  Shapes = -> [Cylinder198,Cylinder199]
FEATURE [Part::Cut] Cut120
  Base = -> Cut117
  Refine = true
  Tool = -> Fusion132
FEATURE [Part::Fillet] Fillet050  label="battery-box"
  Base = -> Cut120
  Edges = 2 edges r=4: [Edge31,Edge33]
FEATURE [Part::Box] Box106  label="Cube092"
  AttacherType = Attacher::AttachEngine3D
  Height = 22.5
  Length = 56
  Placement = pos=(249.5,-44.5,-4) rot=(0,0,1;0rad)
  Width = 40.5
FEATURE [Part::Cut] Cut121  label="battery-box-cover"
  Base = -> Fusion130
  Refine = true
  Tool = -> Box106
FEATURE [Part::Cylinder] Cylinder204
  Angle = 360
  AttacherType = Attacher::AttachEngine3D
  FirstAngle = 0
  Height = 46
  Placement = pos=(342,63,10) rot=(1,0,0;1.5708rad)
  Radius = 10
  SecondAngle = 0
FEATURE [Part::Box] Box107  label="Cube093"
  AttacherType = Attacher::AttachEngine3D
  Height = 12
  Length = 10
  Placement = pos=(331,21,4) rot=(0,0,1;0rad)
  Width = 38
FEATURE [Part::Fillet] Fillet051
  Base = -> Cylinder204
  Edges = 2 edges r=4: [Edge1,Edge3]
FEATURE [Part::MultiFuse] Fusion136
  Refine = true
  Shapes = -> [Box107,Fillet051]
FEATURE [Part::Cylinder] Cylinder205
  Angle = 360
  AttacherType = Attacher::AttachEngine3D
  FirstAngle = 0
  Height = 46
  Placement = pos=(304,56,10) rot=(0,1,0;1.5708rad)
  Radius = 1.25
  SecondAngle = 0
FEATURE [Part::Cylinder] Cylinder206
  Angle = 360
  AttacherType = Attacher::AttachEngine3D
  FirstAngle = 0
  Height = 46
  Placement = pos=(304,24,10) rot=(0,1,0;1.5708rad)
  Radius = 1.25
  SecondAngle = 0
FEATURE [Part::Cylinder] Cylinder207
  Angle = 360
  AttacherType = Attacher::AttachEngine3D
  FirstAngle = 0
  Height = 40
  Placement = pos=(342,60,10) rot=(1,0,0;1.5708rad)
  Radius = 8
  SecondAngle = 0
FEATURE [Part::Cut] Cut122
  Base = -> Fusion136
  Refine = true
  Tool = -> Cylinder207
FEATURE [Part::Box] Box108  label="Cube094"
  AttacherType = Attacher::AttachEngine3D
  Height = 10
  Length = 15
  Placement = pos=(331,34,5) rot=(0,0,1;0rad)
  Width = 12
FEATURE [Part::Cut] Cut123
  Base = -> Cut122
  Placement = pos=(0,0,-1) rot=(0,0,1;0rad)
  Refine = true
  Tool = -> Box108
FEATURE [Part::Cylinder] Cylinder208
  Angle = 360
  AttacherType = Attacher::AttachEngine3D
  FirstAngle = 0
  Height = 18
  Placement = pos=(331,56,10) rot=(0,1,0;1.5708rad)
  Radius = 3.5
  SecondAngle = 0
FEATURE [Part::Cylinder] Cylinder209
  Angle = 360
  AttacherType = Attacher::AttachEngine3D
  FirstAngle = 0
  Height = 18
  Placement = pos=(331,24,10) rot=(0,1,0;1.5708rad)
  Radius = 3.5
  SecondAngle = 0
FEATURE [Part::MultiFuse] Fusion138
  Refine = true
  Shapes = -> [Cylinder205,Cylinder206]
FEATURE [Part::Fillet] Fillet052
  Base = -> Cylinder173
  Edges = 2 edges r=4: [Edge1,Edge3]
FEATURE [Part::Fillet] Fillet053
  Base = -> Cylinder174
  Edges = 2 edges r=4: [Edge1,Edge3]
FEATURE [Part::Cylinder] Cylinder210
  Angle = 360
  AttacherType = Attacher::AttachEngine3D
  FirstAngle = 0
  Height = 1.5
  Placement = pos=(342,55,10) rot=(1,0,0;1.5708rad)
  Radius = 10.5
  SecondAngle = 0
FEATURE [Part::Cylinder] Cylinder211
  Angle = 360
  AttacherType = Attacher::AttachEngine3D
  FirstAngle = 0
  Height = 1.5
  Placement = pos=(342,26.5,10) rot=(1,0,0;1.5708rad)
  Radius = 10.5
  SecondAngle = 0
FEATURE [Part::MultiFuse] Fusion139
  Refine = true
  Shapes = -> [Cylinder208,Cylinder209]
FEATURE [Part::MultiFuse] Fusion140
  Refine = true
  Shapes = -> [Fusion139,Cut123]
FEATURE [Part::MultiFuse] Fusion141
  Placement = pos=(0,0,-1) rot=(0,0,1;0rad)
  Refine = true
  Shapes = -> [Cylinder210,Cylinder211]
FEATURE [Part::Cylinder] Cylinder212
  Angle = 360
  AttacherType = Attacher::AttachEngine3D
  FirstAngle = 0
  Height = 31.5
  Placement = pos=(342,55.5,9) rot=(1,0,0;1.5708rad)
  Radius = 9.5
  SecondAngle = 0
FEATURE [Part::Cut] Cut124
  Base = -> Fusion141
  Refine = true
  Tool = -> Cylinder212
FEATURE [Part::MultiFuse] Fusion142
  Refine = true
  Shapes = -> [Fusion140,Cut124]
FEATURE [Part::Cut] Cut125  label="air-tank-central"
  Base = -> Fusion142
  Refine = true
  Tool = -> Fusion138
FEATURE [Part::Box] Box109  label="Cube095"
  AttacherType = Attacher::AttachEngine3D
  Height = 2
  Length = 17
  Placement = pos=(310.5,-40,-3) rot=(0,0,1;0rad)
  Width = 36
FEATURE [Part::Box] Box110  label="Cube096"
  AttacherType = Attacher::AttachEngine3D
  Height = 11
  Length = 12
  Placement = pos=(315,-38,-1.5) rot=(0,0,1;0rad)
  Width = 34
FEATURE [Part::Box] Box111  label="Cube097"
  AttacherType = Attacher::AttachEngine3D
  Height = 11
  Length = 12
  Placement = pos=(311,-38,-13.5) rot=(0,0,1;0rad)
  Width = 34
FEATURE [Part::Cylinder] Cylinder213
  Angle = 360
  AttacherType = Attacher::AttachEngine3D
  FirstAngle = 0
  Height = 1.5
  Placement = pos=(321,-12,9) rot=(1,0,0;1.5708rad)
  Radius = 10.5
  SecondAngle = 0
FEATURE [Part::Cylinder] Cylinder214
  Angle = 360
  AttacherType = Attacher::AttachEngine3D
  FirstAngle = 0
  Height = 1.5
  Placement = pos=(321,-36.5,9) rot=(1,0,0;1.5708rad)
  Radius = 10.5
  SecondAngle = 0
FEATURE [Part::MultiFuse] Fusion144
  Refine = true
  Shapes = -> [Cylinder214,Cylinder213]
FEATURE [Part::Cylinder] Cylinder215
  Angle = 360
  AttacherType = Attacher::AttachEngine3D
  FirstAngle = 0
  Height = 1.5
  Placement = pos=(321,-36.5,9) rot=(1,0,0;1.5708rad)
  Radius = 10.5
  SecondAngle = 0
FEATURE [Part::Cylinder] Cylinder216
  Angle = 360
  AttacherType = Attacher::AttachEngine3D
  FirstAngle = 0
  Height = 1.5
  Placement = pos=(321,-12,9) rot=(1,0,0;1.5708rad)
  Radius = 10.5
  SecondAngle = 0
FEATURE [Part::MultiFuse] Fusion145
  Placement = pos=(-4,0,-22) rot=(0,0,1;0rad)
  Refine = true
  Shapes = -> [Cylinder215,Cylinder216]
FEATURE [Part::Cylinder] Cylinder217
  Angle = 360
  AttacherType = Attacher::AttachEngine3D
  FirstAngle = 0
  Height = 38
  Placement = pos=(321,-6,9) rot=(1,0,0;1.5708rad)
  Radius = 8
  SecondAngle = 0
FEATURE [Part::Cylinder] Cylinder218
  Angle = 360
  AttacherType = Attacher::AttachEngine3D
  FirstAngle = 0
  Height = 38
  Placement = pos=(317,-6,-13) rot=(1,0,0;1.5708rad)
  Radius = 8
  SecondAngle = 0
FEATURE [Part::Cylinder] Cylinder219
  Angle = 360
  AttacherType = Attacher::AttachEngine3D
  FirstAngle = 0
  Height = 38
  Placement = pos=(317,-4,-13) rot=(1,0,0;1.5708rad)
  Radius = 4
  SecondAngle = 0
FEATURE [Part::Cylinder] Cylinder220
  Angle = 360
  AttacherType = Attacher::AttachEngine3D
  FirstAngle = 0
  Height = 38
  Placement = pos=(321,-4,9) rot=(1,0,0;1.5708rad)
  Radius = 4
  SecondAngle = 0
FEATURE [Part::MultiFuse] Fusion147
  Refine = true
  Shapes = -> [Cylinder217,Cylinder218,Cylinder219,Cylinder220]
FEATURE [Part::Box] Box112  label="Cube098"
  AttacherType = Attacher::AttachEngine3D
  Height = 12
  Length = 25
  Placement = pos=(309.5,-3.5,-9.5) rot=(0,0,1;0rad)
  Width = 12
FEATURE [Part::Box] Box113  label="Cube099"
  AttacherType = Attacher::AttachEngine3D
  Height = 12
  Length = 12
  Placement = pos=(315,-7,-3) rot=(0,0,1;0rad)
  Width = 5
FEATURE [Part::Box] Box115  label="Cube101"
  AttacherType = Attacher::AttachEngine3D
  Height = 9
  Length = 51
  Placement = pos=(259,-4,-9) rot=(0,0,1;0rad)
  Width = 12.5
FEATURE [Part::Cylinder] Cylinder222
  Angle = 360
  AttacherType = Attacher::AttachEngine3D
  FirstAngle = 0
  Height = 15
  Placement = pos=(297,4,-9) rot=(0,0,1;0rad)
  Radius = 1.6
  SecondAngle = 0
FEATURE [Part::Cylinder] Cylinder223
  Angle = 360
  AttacherType = Attacher::AttachEngine3D
  FirstAngle = 0
  Height = 15
  Placement = pos=(262,4,-9) rot=(0,0,1;0rad)
  Radius = 1.6
  SecondAngle = 0
FEATURE [Part::MultiFuse] Fusion149
  Placement = pos=(2,-1.5,0) rot=(0,0,1;0rad)
  Refine = true
  Shapes = -> [Cylinder222,Cylinder223]
FEATURE [Part::Cylinder] Cylinder224
  Angle = 360
  AttacherType = Attacher::AttachEngine3D
  FirstAngle = 0
  Height = 15
  Placement = pos=(310.5,8.5,16) rot=(1,0,0;1.5708rad)
  Radius = 1.1
  SecondAngle = 0
FEATURE [Part::Cylinder] Cylinder225
  Angle = 360
  AttacherType = Attacher::AttachEngine3D
  FirstAngle = 0
  Height = 0.5
  Placement = pos=(321,-46,9) rot=(1,0,0;1.5708rad)
  Radius = 2
  SecondAngle = 0
FEATURE [Part::Cylinder] Cylinder226
  Angle = 360
  AttacherType = Attacher::AttachEngine3D
  FirstAngle = 0
  Height = 0.5
  Placement = pos=(317,-46,-13) rot=(1,0,0;1.5708rad)
  Radius = 2
  SecondAngle = 0
FEATURE [Part::MultiFuse] Fusion150
  Refine = true
  Shapes = -> [Fillet052,Cylinder225]
FEATURE [Part::MultiFuse] Fusion151
  Refine = true
  Shapes = -> [Fillet053,Cylinder226]
FEATURE [Part::MultiFuse] Fusion152
  Refine = true
  Shapes = -> [Fusion150,Box110]
FEATURE [Part::MultiFuse] Fusion153
  Refine = true
  Shapes = -> [Fusion151,Box111]
FEATURE [Part::MultiFuse] Fusion154
  Refine = true
  Shapes = -> [Fusion152,Fusion144]
FEATURE [Part::MultiFuse] Fusion155
  Refine = true
  Shapes = -> [Fusion153,Fusion145]
FEATURE [Part::MultiFuse] Fusion156
  Refine = true
  Shapes = -> [Fusion154,Fusion155,Box109]
FEATURE [Part::Cut] Cut132
  Base = -> Fusion156
  Placement = pos=(0,-2.5,0) rot=(0,0,1;0rad)
  Refine = true
  Tool = -> Fusion147
FEATURE [Part::Box] Box116  label="Cube102"
  AttacherType = Attacher::AttachEngine3D
  Height = 10
  Length = 12
  Placement = pos=(322.5,-6.5,-9.5) rot=(0,0,1;0rad)
  Width = 12
FEATURE [Part::MultiFuse] Fusion157
  Refine = true
  Shapes = -> [Box112,Box116]
FEATURE [Part::Cylinder] Cylinder227
  Angle = 360
  AttacherType = Attacher::AttachEngine3D
  FirstAngle = 0
  Height = 4
  Placement = pos=(330,-6,-5) rot=(1,0,0;1.5708rad)
  Radius = 5
  SecondAngle = 0
FEATURE [Part::MultiFuse] Fusion158
  Refine = true
  Shapes = -> [Fusion157,Cylinder227]
FEATURE [Part::Cylinder] Cylinder228
  Angle = 360
  AttacherType = Attacher::AttachEngine3D
  FirstAngle = 0
  Height = 4
  Placement = pos=(330,-6,-5) rot=(1,0,0;1.5708rad)
  Radius = 5
  SecondAngle = 0
FEATURE [Part::Box] Box117  label="Cube103"
  AttacherType = Attacher::AttachEngine3D
  Height = 12
  Length = 12
  Placement = pos=(311,-7,-13) rot=(0,0,1;0rad)
  Width = 5
FEATURE [Part::Cylinder] Cylinder229
  Angle = 360
  AttacherType = Attacher::AttachEngine3D
  FirstAngle = 0
  Height = 5
  Placement = pos=(321,-2,9) rot=(1,0,0;1.5708rad)
  Radius = 6
  SecondAngle = 0
FEATURE [Part::Cylinder] Cylinder230
  Angle = 360
  AttacherType = Attacher::AttachEngine3D
  FirstAngle = 0
  Height = 5
  Placement = pos=(317,-2,-13) rot=(1,0,0;1.5708rad)
  Radius = 6
  SecondAngle = 0
FEATURE [Part::Cylinder] Cylinder231
  Angle = 360
  AttacherType = Attacher::AttachEngine3D
  FirstAngle = 0
  Height = 10
  Placement = pos=(321,-2,9) rot=(1,0,0;1.5708rad)
  Radius = 4
  SecondAngle = 0
FEATURE [Part::Cylinder] Cylinder232
  Angle = 360
  AttacherType = Attacher::AttachEngine3D
  FirstAngle = 0
  Height = 10
  Placement = pos=(317,-2,-13) rot=(1,0,0;1.5708rad)
  Radius = 4
  SecondAngle = 0
FEATURE [Part::MultiFuse] Fusion159
  Placement = pos=(0,0.5,0) rot=(0,0,1;0rad)
  Refine = true
  Shapes = -> [Cylinder229,Cylinder230,Box117,Box113]
FEATURE [Part::MultiFuse] Fusion160
  Placement = pos=(0,4,0) rot=(0,0,1;0rad)
  Refine = true
  Shapes = -> [Cylinder232,Cylinder231]
FEATURE [Part::Cylinder] Cylinder233
  Angle = 360
  AttacherType = Attacher::AttachEngine3D
  FirstAngle = 0
  Height = 2.5
  Placement = pos=(326,8.5,6) rot=(1,0,0;1.5708rad)
  Radius = 3.1
  SecondAngle = 0
FEATURE [Part::Cylinder] Cylinder234
  Angle = 360
  AttacherType = Attacher::AttachEngine3D
  FirstAngle = 0
  Height = 2.5
  Placement = pos=(326,8.5,14) rot=(1,0,0;1.5708rad)
  Radius = 3.1
  SecondAngle = 0
FEATURE [Part::Cylinder] Cylinder235
  Angle = 360
  AttacherType = Attacher::AttachEngine3D
  FirstAngle = 0
  Height = 2.5
  Placement = pos=(304,8.5,14) rot=(1,0,0;1.5708rad)
  Radius = 3.1
  SecondAngle = 0
FEATURE [Part::Cylinder] Cylinder236
  Angle = 360
  AttacherType = Attacher::AttachEngine3D
  FirstAngle = 0
  Height = 2.5
  Placement = pos=(304,8.5,6) rot=(1,0,0;1.5708rad)
  Radius = 3.1
  SecondAngle = 0
FEATURE [Part::MultiFuse] Fusion161
  Placement = pos=(0,-10,0) rot=(0,0,1;0rad)
  Refine = true
  Shapes = -> [Cylinder236,Cylinder233,Cylinder235,Cylinder234]
FEATURE [Part::Cut] Cut133  label="air-tank-lateral"
  Base = -> Cut132
  Refine = true
  Tool = -> Cylinder228
FEATURE [Part::Box] Box118  label="Cube104"
  AttacherType = Attacher::AttachEngine3D
  Height = 24
  Length = 21
  Placement = pos=(306,-6.5,-9) rot=(0,0,1;0rad)
  Width = 2.5
FEATURE [Part::Box] Box119  label="Cube105"
  AttacherType = Attacher::AttachEngine3D
  Height = 7
  Length = 4
  Placement = pos=(304,-6.5,13) rot=(0,0,1;0rad)
  Width = 5
FEATURE [Part::Box] Box120  label="Cube106"
  AttacherType = Attacher::AttachEngine3D
  Height = 9.1
  Length = 6
  Placement = pos=(298,-6.5,10.9) rot=(0,0,1;0rad)
  Width = 5
FEATURE [Part::Box] Box121  label="Cube107"
  AttacherType = Attacher::AttachEngine3D
  Height = 29
  Length = 34
  Placement = pos=(298,-4,-9) rot=(0,0,1;0rad)
  Width = 2.5
FEATURE [Part::MultiFuse] Fusion163
  Refine = true
  Shapes = -> [Box120,Box119]
FEATURE [Part::Fillet] Fillet054
  Base = -> Box118
  Edges = 1 edges r=6: [Edge6]
FEATURE [Part::MultiFuse] Fusion164
  Refine = true
  Shapes = -> [Fillet054,Box118,Box121,Fusion159,Box115]
FEATURE [Part::Chamfer] Chamfer022
  Base = -> Fusion158
  Edges = 1 edges r=5.5: [Edge25]
FEATURE [Part::MultiFuse] Fusion165
  Refine = true
  Shapes = -> [Fusion161,Chamfer022]
FEATURE [Part::Fillet] Fillet055
  Base = -> Fusion164
  Edges = 1 edges r=6: [Edge48]
FEATURE [Part::Cut] Cut134
  Base = -> Fillet055
  Refine = true
  Tool = -> Fusion163
FEATURE [Part::Fillet] Fillet056
  Base = -> Cut134
  Edges = 3 edges r=2: [Edge19,Edge21,Edge56]
FEATURE [Part::Cut] Cut135
  Base = -> Fillet056
  Refine = true
  Tool = -> Fusion160
FEATURE [Part::Cut] Cut136
  Base = -> Cut135
  Refine = true
  Tool = -> Fusion165
FEATURE [Part::Cut] Cut137
  Base = -> Cut136
  Refine = true
  Tool = -> Fusion149
FEATURE [Part::Cylinder] Cylinder237
  Angle = 360
  AttacherType = Attacher::AttachEngine3D
  FirstAngle = 0
  Height = 2.5
  Placement = pos=(310.5,-4,16) rot=(1,0,0;1.5708rad)
  Radius = 2.5
  SecondAngle = 0
FEATURE [Part::MultiFuse] Fusion166
  Refine = true
  Shapes = -> [Cylinder237,Cylinder224]
FEATURE [Part::Cut] Cut138  label="air-tank-lateral-holder"
  Base = -> Cut137
  Refine = true
  Tool = -> Fusion166
FEATURE [Part::Cylinder] Cylinder238
  Angle = 360
  AttacherType = Attacher::AttachEngine3D
  FirstAngle = 0
  Height = 15
  Placement = pos=(292,-4,-24) rot=(0,0,1;1.5708rad)
  Radius = 5
  SecondAngle = 0
FEATURE [Part::Box] Box122  label="Cube108"
  AttacherType = Attacher::AttachEngine3D
  Height = 3
  Length = 45
  Placement = pos=(259,-4,-12) rot=(0,0,1;0rad)
  Width = 12.5
FEATURE [Part::Cylinder] Cylinder239
  Angle = 360
  AttacherType = Attacher::AttachEngine3D
  FirstAngle = 0
  Height = 15
  Placement = pos=(299,2.5,-24) rot=(0,0,1;0rad)
  Radius = 1.6
  SecondAngle = 0
FEATURE [Part::Cylinder] Cylinder240
  Angle = 360
  AttacherType = Attacher::AttachEngine3D
  FirstAngle = 0
  Height = 15
  Placement = pos=(264,2.5,-24) rot=(0,0,1;0rad)
  Radius = 1.6
  SecondAngle = 0
FEATURE [Part::MultiFuse] Fusion167
  Refine = true
  Shapes = -> [Cylinder239,Cylinder240]
FEATURE [Part::MultiFuse] Fusion168
  Refine = true
  Shapes = -> [Cylinder238,Box122]
FEATURE [Part::Chamfer] Chamfer023
  Base = -> Fusion168
  Edges = 2 edges r=5: [Edge3,Edge7]
FEATURE [Part::Cut] Cut139
  Base = -> Chamfer023
  Refine = true
  Tool = -> Fusion167
FEATURE [Part::Cylinder] Cylinder241
  Angle = 360
  AttacherType = Attacher::AttachEngine3D
  FirstAngle = 0
  Height = 15
  Placement = pos=(292,-4,-24) rot=(0,0,1;1.5708rad)
  Radius = 2.1
  SecondAngle = 0
FEATURE [Part::Box] Box123  label="Cube109"
  AttacherType = Attacher::AttachEngine3D
  Height = 11
  Length = 24
  Placement = pos=(280,-5.5,-20) rot=(0,0,1;0rad)
  Width = 3
FEATURE [Part::Chamfer] Chamfer024
  Base = -> Box123
  Edges = 2 edges r=8: [Edge4,Edge8]
FEATURE [Part::Box] Box124  label="Cube110"
  AttacherType = Attacher::AttachEngine3D
  Height = 11
  Length = 3
  Placement = pos=(290.5,-3,-20) rot=(0,0,1;0rad)
  Width = 10
FEATURE [Part::Chamfer] Chamfer025
  Base = -> Box124
  Edges = 1 edges r=8: [Edge11]
  Placement = pos=(0,1,0) rot=(0,0,1;0rad)
FEATURE [Part::MultiFuse] Fusion169
  Refine = true
  Shapes = -> [Chamfer024,Chamfer025,Cut139]
FEATURE [Part::Cut] Cut140  label="spare_wheel_holder"
  Base = -> Fusion169
  Refine = true
  Tool = -> Cylinder241
FEATURE [Part::Box] Box125  label="Cube111"
  AttacherType = Attacher::AttachEngine3D
  Height = 18
  Length = 20
  Placement = pos=(238,84.5,-18) rot=(0,0,1;0rad)
  Width = 8
FEATURE [Part::Cut] Cut141
  Base = -> Fillet039
  Refine = true
  Tool = -> Box051
FEATURE [Part::Mirroring] Part__Mirroring013  label="Cut063 (Mirror #6)001"
  Base = (0,0,0)
  Normal = (1,0,0)
  Placement = pos=(394,0,0) rot=(0,0,1;0rad)
  Source = -> Cut063
FEATURE [Part::Cut] Cut142
  Base = -> Fusion059
  Refine = true
  Tool = -> Cylinder090
FEATURE [Part::MultiFuse] Fusion170  label="front-right-wing"
  Placement = pos=(0,0,-4) rot=(0,0,1;0rad)
  Refine = true
  Shapes = -> [Cut142,Cut141,Part__Mirroring013]
FEATURE [Part::Fillet] Fillet057
  Base = -> Box125
  Edges = 2 edges r=3: [Edge11,Edge12]
FEATURE [Part::Cut] Cut143  label="front-right-wing_with_battery_hole"
  Base = -> Fusion073
  Refine = true
  Tool = -> Fillet057
FEATURE [Part::Box] Box126  label="Cube112"
  AttacherType = Attacher::AttachEngine3D
  Height = 6
  Length = 60
  Placement = pos=(155,5,20) rot=(0,0,1;0rad)
  Width = 70
FEATURE [Part::Box] Box127  label="Cube113"
  AttacherType = Attacher::AttachEngine3D
  Height = 6
  Length = 62
  Placement = pos=(155,5,26) rot=(0,1,0;0.05236rad)
  Width = 70
FEATURE [Part::Cut] Cut144
  Base = -> Box126
  Refine = true
  Tool = -> Box127
FEATURE [Part::Cylinder] Cylinder242
  Angle = 360
  AttacherType = Attacher::AttachEngine3D
  FirstAngle = 0
  Height = 3
  Placement = pos=(159.5,5,20) rot=(0,0,1;0rad)
  Radius = 3.5
  SecondAngle = 0
FEATURE [Part::Cylinder] Cylinder243
  Angle = 360
  AttacherType = Attacher::AttachEngine3D
  FirstAngle = 0
  Height = 3
  Placement = pos=(159.5,5,23) rot=(0,0,1;0rad)
  Radius = 3.5
  SecondAngle = 0
FEATURE [Part::Cylinder] Cylinder244
  Angle = 360
  AttacherType = Attacher::AttachEngine3D
  FirstAngle = 0
  Height = 6
  Placement = pos=(159.5,5,20) rot=(0,0,1;0rad)
  Radius = 1.6
  SecondAngle = 0
FEATURE [Part::MultiFuse] Fusion171
  Refine = true
  Shapes = -> [Cylinder244,Cylinder243]
FEATURE [Part::Cylinder] Cylinder245
  Angle = 360
  AttacherType = Attacher::AttachEngine3D
  FirstAngle = 0
  Height = 3
  Placement = pos=(159.5,5,23) rot=(0,0,1;0rad)
  Radius = 3.5
  SecondAngle = 0
FEATURE [Part::Cylinder] Cylinder246
  Angle = 360
  AttacherType = Attacher::AttachEngine3D
  FirstAngle = 0
  Height = 6
  Placement = pos=(159.5,5,20) rot=(0,0,1;0rad)
  Radius = 1.6
  SecondAngle = 0
FEATURE [Part::MultiFuse] Fusion172
  Placement = pos=(0,70,0) rot=(0,0,1;0rad)
  Refine = true
  Shapes = -> [Cylinder246,Cylinder245]
FEATURE [Part::Cylinder] Cylinder247
  Angle = 360
  AttacherType = Attacher::AttachEngine3D
  FirstAngle = 0
  Height = 3
  Placement = pos=(159.5,5,23) rot=(0,0,1;0rad)
  Radius = 3.5
  SecondAngle = 0
FEATURE [Part::Cylinder] Cylinder248
  Angle = 360
  AttacherType = Attacher::AttachEngine3D
  FirstAngle = 0
  Height = 6
  Placement = pos=(159.5,5,20) rot=(0,0,1;0rad)
  Radius = 1.6
  SecondAngle = 0
FEATURE [Part::MultiFuse] Fusion173
  Placement = pos=(51,0,0) rot=(0,0,1;0rad)
  Refine = true
  Shapes = -> [Cylinder248,Cylinder247]
FEATURE [Part::Cylinder] Cylinder249
  Angle = 360
  AttacherType = Attacher::AttachEngine3D
  FirstAngle = 0
  Height = 3
  Placement = pos=(159.5,5,23) rot=(0,0,1;0rad)
  Radius = 3.5
  SecondAngle = 0
FEATURE [Part::Cylinder] Cylinder250
  Angle = 360
  AttacherType = Attacher::AttachEngine3D
  FirstAngle = 0
  Height = 6
  Placement = pos=(159.5,5,20) rot=(0,0,1;0rad)
  Radius = 1.6
  SecondAngle = 0
FEATURE [Part::MultiFuse] Fusion174
  Placement = pos=(51,70,0) rot=(0,0,1;0rad)
  Refine = true
  Shapes = -> [Cylinder250,Cylinder249]
FEATURE [Part::Cylinder] Cylinder251
  Angle = 360
  AttacherType = Attacher::AttachEngine3D
  FirstAngle = 0
  Height = 3
  Placement = pos=(159.5,75,20) rot=(0,0,1;0rad)
  Radius = 3.5
  SecondAngle = 0
FEATURE [Part::Cylinder] Cylinder252
  Angle = 360
  AttacherType = Attacher::AttachEngine3D
  FirstAngle = 0
  Height = 3
  Placement = pos=(210.5,5,20) rot=(0,0,1;0rad)
  Radius = 3.5
  SecondAngle = 0
FEATURE [Part::Cylinder] Cylinder253
  Angle = 360
  AttacherType = Attacher::AttachEngine3D
  FirstAngle = 0
  Height = 3
  Placement = pos=(210.5,75,20) rot=(0,0,1;0rad)
  Radius = 3.5
  SecondAngle = 0
FEATURE [Part::MultiFuse] Fusion175
  Refine = true
  Shapes = -> [Cylinder242,Cylinder251,Cylinder252,Cylinder253]
FEATURE [Part::MultiFuse] Fusion176
  Refine = true
  Shapes = -> [Cut144,Fusion175]
FEATURE [Part::MultiFuse] Fusion177
  Refine = true
  Shapes = -> [Fusion171,Fusion173,Fusion172,Fusion174]
FEATURE [Part::Cut] Cut145
  Base = -> Fusion176
  Refine = true
  Tool = -> Fusion177
FEATURE [Part::Box] Box128  label="Cube114"
  AttacherType = Attacher::AttachEngine3D
  Height = 8
  Length = 10
  Placement = pos=(155,30,12) rot=(0,0,1;0rad)
  Width = 20
FEATURE [Part::Box] Box129  label="Cube115"
  AttacherType = Attacher::AttachEngine3D
  Height = 8
  Length = 5
  Placement = pos=(150,30,12) rot=(0,0,1;0rad)
  Width = 20
FEATURE [Part::Box] Box130  label="Cube116"
  AttacherType = Attacher::AttachEngine3D
  Height = 75
  Length = 5
  Placement = pos=(150,36,12) rot=(0,0,1;0rad)
  Width = 8
FEATURE [Part::Box] Box131  label="Cube117"
  AttacherType = Attacher::AttachEngine3D
  Height = 3
  Length = 4
  Placement = pos=(150,20,50) rot=(0,0,1;0rad)
  Width = 40
FEATURE [Part::Box] Box132  label="Cube118"
  AttacherType = Attacher::AttachEngine3D
  Height = 3
  Length = 4
  Placement = pos=(150,28,82) rot=(0,0,1;0rad)
  Width = 24
FEATURE [Part::MultiFuse] Fusion178
  Refine = true
  Shapes = -> [Box129,Box132,Box130,Box131]
FEATURE [Part::Box] Box133  label="Cube119"
  AttacherType = Attacher::AttachEngine3D
  Height = 8
  Length = 5
  Placement = pos=(150,50,20) rot=(1,0,0;1.8326rad)
  Width = 24
FEATURE [Part::Box] Box134  label="Cube120"
  AttacherType = Attacher::AttachEngine3D
  Height = 8
  Length = 5
  Placement = pos=(150,50,20) rot=(1,0,0;1.8326rad)
  Width = 24
FEATURE [Part::Mirroring] Part__Mirroring014  label="Cube120 (Mirror #12)"
  Base = (0,0,0)
  Normal = (0,1,0)
  Placement = pos=(0,80,0) rot=(0,0,1;0rad)
  Source = -> Box134
FEATURE [Part::MultiFuse] Fusion179
  Refine = true
  Shapes = -> [Fusion178,Part__Mirroring014,Box133]
FEATURE [Part::MultiFuse] Fusion180
  Refine = true
  Shapes = -> [Box128,Cut145]
FEATURE [Part::Cylinder] Cylinder254
  Angle = 360
  AttacherType = Attacher::AttachEngine3D
  FirstAngle = 0
  Height = 10
  Placement = pos=(150,46,16) rot=(0,1,0;1.5708rad)
  Radius = 1.6
  SecondAngle = 0
FEATURE [Part::Cylinder] Cylinder255
  Angle = 360
  AttacherType = Attacher::AttachEngine3D
  FirstAngle = 0
  Height = 10
  Placement = pos=(150,34,16) rot=(0,1,0;1.5708rad)
  Radius = 1.6
  SecondAngle = 0
FEATURE [Part::Cylinder] Cylinder256
  Angle = 360
  AttacherType = Attacher::AttachEngine3D
  FirstAngle = 0
  Height = 3
  Placement = pos=(150,46,16) rot=(0,1,0;1.5708rad)
  Radius = 3.2
  SecondAngle = 0
FEATURE [Part::Cylinder] Cylinder257
  Angle = 360
  AttacherType = Attacher::AttachEngine3D
  FirstAngle = 0
  Height = 3
  Placement = pos=(150,34,16) rot=(0,1,0;1.5708rad)
  Radius = 3.2
  SecondAngle = 0
FEATURE [Part::Cylinder] Cylinder258
  Angle = 360
  AttacherType = Attacher::AttachEngine3D
  FirstAngle = 0
  Height = 10
  Placement = pos=(150,40,23) rot=(0,1,0;1.5708rad)
  Radius = 1.6
  SecondAngle = 0
FEATURE [Part::Cylinder] Cylinder259
  Angle = 360
  AttacherType = Attacher::AttachEngine3D
  FirstAngle = 0
  Height = 3
  Placement = pos=(150,40,23) rot=(0,1,0;1.5708rad)
  Radius = 3.2
  SecondAngle = 0
FEATURE [Part::MultiFuse] Fusion181
  Refine = true
  Shapes = -> [Cylinder254,Cylinder258,Cylinder256,Cylinder257,Cylinder255,Cylinder259]
FEATURE [Part::Cut] Cut146
  Base = -> Fusion179
  Refine = true
  Tool = -> Fusion181
FEATURE [Part::Cylinder] Cylinder260
  Angle = 360
  AttacherType = Attacher::AttachEngine3D
  FirstAngle = 0
  Height = 10
  Placement = pos=(150,34,16) rot=(0,1,0;1.5708rad)
  Radius = 1.25
  SecondAngle = 0
FEATURE [Part::Cylinder] Cylinder261
  Angle = 360
  AttacherType = Attacher::AttachEngine3D
  FirstAngle = 0
  Height = 10
  Placement = pos=(150,40,23) rot=(0,1,0;1.5708rad)
  Radius = 1.25
  SecondAngle = 0
FEATURE [Part::Cylinder] Cylinder262
  Angle = 360
  AttacherType = Attacher::AttachEngine3D
  FirstAngle = 0
  Height = 10
  Placement = pos=(150,46,16) rot=(0,1,0;1.5708rad)
  Radius = 1.25
  SecondAngle = 0
FEATURE [Part::MultiFuse] Fusion182
  Placement = pos=(5,0,0) rot=(0,0,1;0rad)
  Refine = true
  Shapes = -> [Cylinder260,Cylinder262,Cylinder261]
FEATURE [Part::Cut] Cut147  label="front-platform"
  Base = -> Fusion180
  Refine = true
  Tool = -> Fusion182
FEATURE [Part::Cylinder] Cylinder263
  Angle = 360
  AttacherType = Attacher::AttachEngine3D
  FirstAngle = 0
  Height = 5
  Placement = pos=(150,40,54) rot=(0,1,0;1.5708rad)
  Radius = 2
  SecondAngle = 0
FEATURE [Part::Cut] Cut148
  Base = -> Cut146
  Refine = true
  Tool = -> Cylinder263
FEATURE [Part::Cylinder] Cylinder264
  Angle = 360
  AttacherType = Attacher::AttachEngine3D
  FirstAngle = 0
  Height = 28
  Placement = pos=(150,40,28) rot=(0,0,1;0rad)
  Radius = 2
  SecondAngle = 0
FEATURE [Part::Cylinder] Cylinder265
  Angle = 360
  AttacherType = Attacher::AttachEngine3D
  FirstAngle = 0
  Height = 5
  Placement = pos=(150,22,51.5) rot=(0,1,0;1.5708rad)
  Radius = 0.8
  SecondAngle = 0
FEATURE [Part::Cylinder] Cylinder266
  Angle = 360
  AttacherType = Attacher::AttachEngine3D
  FirstAngle = 0
  Height = 5
  Placement = pos=(150,58,51.5) rot=(0,1,0;1.5708rad)
  Radius = 0.8
  SecondAngle = 0
FEATURE [Part::Cylinder] Cylinder267
  Angle = 360
  AttacherType = Attacher::AttachEngine3D
  FirstAngle = 0
  Height = 5
  Placement = pos=(150,30,83.5) rot=(0,1,0;1.5708rad)
  Radius = 0.8
  SecondAngle = 0
FEATURE [Part::Cylinder] Cylinder268
  Angle = 360
  AttacherType = Attacher::AttachEngine3D
  FirstAngle = 0
  Height = 5
  Placement = pos=(150,50,83.5) rot=(0,1,0;1.5708rad)
  Radius = 0.8
  SecondAngle = 0
FEATURE [Part::MultiFuse] Fusion183
  Refine = true
  Shapes = -> [Cylinder265,Cylinder267,Cylinder268,Cylinder266]
FEATURE [Part::Cylinder] Cylinder269
  Angle = 360
  AttacherType = Attacher::AttachEngine3D
  FirstAngle = 0
  Height = 5
  Placement = pos=(152,52,48.5) rot=(0,0,1;0rad)
  Radius = 0.8
  SecondAngle = 0
FEATURE [Part::Cylinder] Cylinder270
  Angle = 360
  AttacherType = Attacher::AttachEngine3D
  FirstAngle = 0
  Height = 5
  Placement = pos=(152,28,48.5) rot=(0,0,1;0rad)
  Radius = 0.8
  SecondAngle = 0
FEATURE [Part::MultiFuse] Fusion184
  Refine = true
  Shapes = -> [Cylinder269,Cylinder270]
FEATURE [Part::Box] Box135  label="Cube121"
  AttacherType = Attacher::AttachEngine3D
  Height = 28
  Length = 2
  Placement = pos=(148,38,28) rot=(0,0,1;0rad)
  Width = 4
FEATURE [Part::MultiFuse] Fusion185
  Placement = pos=(2,0,0) rot=(0,0,1;0rad)
  Refine = true
  Shapes = -> [Box135,Cylinder264]
FEATURE [Part::Cut] Cut149
  Base = -> Cut148
  Refine = true
  Tool = -> Fusion185
FEATURE [Part::Feature] Face
  shape: bbox 2e-07 x 22 x 68.2 mm, 1 faces, 0 solids (baked)
FEATURE [Part::Extrusion] Extrude001
  Base = -> Face
  Dir = (1,0,0)
  DirMode = 0
  FaceMakerClass = Part::FaceMakerExtrusion
  LengthFwd = 0
  LengthRev = 0
  Placement = pos=(-1,0,0) rot=(0,0,1;0rad)
  Solid = false
  Symmetric = false
FEATURE [Part::Box] Box137  label="Cube123"
  AttacherType = Attacher::AttachEngine3D
  Height = 8
  Length = 1
  Placement = pos=(149,30,20) rot=(0,0,1;0rad)
  Width = 20
FEATURE [Part::Cut] Cut150
  Base = -> Extrude001
  Refine = true
  Tool = -> Box137
FEATURE [Part::Cylinder] Cylinder271
  Angle = 360
  AttacherType = Attacher::AttachEngine3D
  FirstAngle = 0
  Height = 10
  Placement = pos=(144,44,31) rot=(0,1,0;1.5708rad)
  Radius = 1.2
  SecondAngle = 0
FEATURE [Part::Cylinder] Cylinder272
  Angle = 360
  AttacherType = Attacher::AttachEngine3D
  FirstAngle = 0
  Height = 10
  Placement = pos=(144,36,31) rot=(0,1,0;1.5708rad)
  Radius = 1.2
  SecondAngle = 0
FEATURE [Part::MultiFuse] Fusion186
  Refine = true
  Shapes = -> [Fusion184,Fusion183]
FEATURE [Part::Cut] Cut151
  Base = -> Cut149
  Refine = true
  Tool = -> Fusion186
FEATURE [Part::Cylinder] Cylinder273
  Angle = 360
  AttacherType = Attacher::AttachEngine3D
  FirstAngle = 0
  Height = 10
  Placement = pos=(144,40,60) rot=(0,1,0;1.5708rad)
  Radius = 1.2
  SecondAngle = 0
FEATURE [Part::Box] Box138  label="Cube124"
  AttacherType = Attacher::AttachEngine3D
  Height = 22
  Length = 1
  Placement = pos=(149,30,63) rot=(0,0,1;0rad)
  Width = 20
FEATURE [Part::Cut] Cut152
  Base = -> Cut150
  Refine = true
  Tool = -> Box138
FEATURE [Part::MultiFuse] Fusion187
  Refine = true
  Shapes = -> [Cylinder271,Cylinder272,Cylinder273]
FEATURE [Part::Cylinder] Cylinder274
  Angle = 360
  AttacherType = Attacher::AttachEngine3D
  FirstAngle = 0
  Height = 10
  Placement = pos=(144,44,31) rot=(0,1,0;1.5708rad)
  Radius = 0.85
  SecondAngle = 0
FEATURE [Part::Cylinder] Cylinder275
  Angle = 360
  AttacherType = Attacher::AttachEngine3D
  FirstAngle = 0
  Height = 10
  Placement = pos=(144,40,60) rot=(0,1,0;1.5708rad)
  Radius = 0.85
  SecondAngle = 0
FEATURE [Part::Cylinder] Cylinder276
  Angle = 360
  AttacherType = Attacher::AttachEngine3D
  FirstAngle = 0
  Height = 10
  Placement = pos=(144,36,31) rot=(0,1,0;1.5708rad)
  Radius = 0.85
  SecondAngle = 0
FEATURE [Part::MultiFuse] Fusion188
  Refine = true
  Shapes = -> [Cylinder274,Cylinder276,Cylinder275]
FEATURE [Part::Cut] Cut153
  Base = -> Cut152
  Refine = true
  Tool = -> Fusion187
FEATURE [Part::Cut] Cut154  label="wriring-holder"
  Base = -> Cut151
  Refine = true
  Tool = -> Fusion188
FEATURE [Part::Box] Box139  label="Cube125"
  AttacherType = Attacher::AttachEngine3D
  Height = 5
  Length = 1
  Placement = pos=(149,38,28) rot=(0,0,1;0rad)
  Width = 4
FEATURE [Part::Fillet] Fillet058
  Base = -> Box139
  Edges = 2 edges r=1.99: [Edge10,Edge12]
FEATURE [Part::Cut] Cut155  label="wriring-holder-closure"
  Base = -> Cut153
  Refine = true
  Tool = -> Fillet058
FEATURE [Part::Box] Box140  label="Cube126"
  AttacherType = Attacher::AttachEngine3D
  Height = 4
  Length = 6
  Placement = pos=(234,-30,21) rot=(0,0,1;0rad)
  Width = 60
FEATURE [Part::Cylinder] Cylinder277
  Angle = 360
  AttacherType = Attacher::AttachEngine3D
  FirstAngle = 0
  Height = 4
  Placement = pos=(237,14,21) rot=(0,0,1;0rad)
  Radius = 5
  SecondAngle = 0
FEATURE [Part::Cylinder] Cylinder278
  Angle = 360
  AttacherType = Attacher::AttachEngine3D
  FirstAngle = 0
  Height = 4
  Placement = pos=(237,30,21) rot=(0,0,1;0rad)
  Radius = 4
  SecondAngle = 0
FEATURE [Part::Cylinder] Cylinder279
  Angle = 360
  AttacherType = Attacher::AttachEngine3D
  FirstAngle = 0
  Height = 4
  Placement = pos=(237,14,21) rot=(0,0,1;0rad)
  Radius = 3
  SecondAngle = 0
FEATURE [Part::Cylinder] Cylinder280
  Angle = 360
  AttacherType = Attacher::AttachEngine3D
  FirstAngle = 0
  Height = 4
  Placement = pos=(237,30,21) rot=(0,0,1;0rad)
  Radius = 1.25
  SecondAngle = 0
FEATURE [Part::Cylinder] Cylinder281
  Angle = 360
  AttacherType = Attacher::AttachEngine3D
  FirstAngle = 0
  Height = 37
  Placement = pos=(237,8.5,26) rot=(1,0,0;1.5708rad)
  Radius = 2
  SecondAngle = 0
FEATURE [Part::MultiFuse] Fusion189
  Refine = true
  Shapes = -> [Box140,Cylinder278,Cylinder277]
FEATURE [Part::MultiFuse] Fusion190
  Refine = true
  Shapes = -> [Cylinder279,Cylinder280]
FEATURE [Part::Cut] Cut156
  Base = -> Fusion189
  Refine = true
  Tool = -> Fusion190
FEATURE [Part::Fillet] Fillet059
  Base = -> Cut156
  Edges = 2 edges r=2: [Edge2,Edge4]
FEATURE [Part::Cut] Cut157  label="fifth_wheel_disengage_lever"
  Base = -> Fillet059
  Placement = pos=(-7,-9,1) rot=(0,0,1;0rad)
  Refine = true
  Tool = -> Cylinder281
FEATURE [Part::Cylinder] Cylinder282
  Angle = 360
  AttacherType = Attacher::AttachEngine3D
  FirstAngle = 0
  Height = 15
  Placement = pos=(6,5.5,0) rot=(0,0,1;0rad)
  Radius = 1.6
  SecondAngle = 0
FEATURE [Part::Box] Box141  label="Cube127"
  AttacherType = Attacher::AttachEngine3D
  Height = 15
  Length = 16
  Placement = pos=(0,-0.25,0) rot=(0,0,1;0rad)
  Width = 11.5
FEATURE [Part::Box] Box142  label="Cube128"
  AttacherType = Attacher::AttachEngine3D
  Height = 8
  Length = 16
  Placement = pos=(0,1.75,0) rot=(0,0,1;0rad)
  Width = 7.5
FEATURE [Part::Cut] Cut158
  Base = -> Box141
  Placement = pos=(2,0,0) rot=(0,0,1;0rad)
  Refine = true
  Tool = -> Box142
FEATURE [Part::Cylinder] Cylinder283
  Angle = 360
  AttacherType = Attacher::AttachEngine3D
  FirstAngle = 0
  Height = 11.5
  Placement = pos=(10,11.25,4) rot=(1,0,0;1.5708rad)
  Radius = 2.1
  SecondAngle = 0
FEATURE [Part::Cylinder] Cylinder284
  Angle = 360
  AttacherType = Attacher::AttachEngine3D
  FirstAngle = 0
  Height = 15
  Placement = pos=(14,5.5,0) rot=(0,0,1;0rad)
  Radius = 1.6
  SecondAngle = 0
FEATURE [Part::MultiFuse] Fusion191
  Refine = true
  Shapes = -> [Cylinder283,Cylinder284,Cylinder282]
FEATURE [Part::Cut] Cut159
  Base = -> Cut158
  Refine = true
  Tool = -> Fusion191
FEATURE [Part::Chamfer] Chamfer027
  Base = -> Cut159
  Edges = 4 edges r=5: [Edge3,Edge7,Edge17,Edge29]
FEATURE [Part::Fillet] Fillet060
  Base = -> Chamfer027
  Edges = 8 edges r=3: [Edge2,Edge7,Edge16,Edge35,Edge41,Edge42,Edge43,Edge47]
  Placement = pos=(22.5,-2.75,-15) rot=(0,0,1;0rad)
FEATURE [Part::Cut] Cut160
  Base = -> Cut028
  Refine = true
  Tool = -> Fusion034
FEATURE [Part::Chamfer] Chamfer028
  Base = -> Cut160
  Edges = 4 edges r=5: [Edge3,Edge7,Edge17,Edge29]
FEATURE [Part::Fillet] Fillet061
  Base = -> Chamfer028
  Edges = 8 edges r=3: [Edge2,Edge7,Edge16,Edge35,Edge41,Edge42,Edge43,Edge47]
  Placement = pos=(22.5,71.75,-15) rot=(0,0,1;0rad)
FEATURE [Part::Box] Box143  label="Cube129"
  AttacherType = Attacher::AttachEngine3D
  Height = 2
  Length = 20
  Placement = pos=(24,-3,-2) rot=(0,0,1;0rad)
  Width = 13
FEATURE [Part::Box] Box144  label="Cube130"
  AttacherType = Attacher::AttachEngine3D
  Height = 2
  Length = 20
  Placement = pos=(24,70,-2) rot=(0,0,1;0rad)
  Width = 13
FEATURE [Part::Cut] Cut161
  Base = -> Fillet060
  Refine = true
  Tool = -> Box143
FEATURE [Part::Cut] Cut162
  Base = -> Fillet061
  Refine = true
  Tool = -> Box144
FEATURE [Part::Chamfer] Chamfer029
  Base = -> Cut161
  Edges = 1 edges r=3.5: [Edge41]
  Placement = pos=(0,0,2) rot=(0,0,1;0rad)
FEATURE [Part::Chamfer] Chamfer030
  Base = -> Cut162
  Edges = 1 edges r=3.5: [Edge45]
  Placement = pos=(0,0,2) rot=(0,0,1;0rad)
FEATURE [Part::Cut] Cut163
  Base = -> Chamfer009
  Placement = pos=(241.5,-2.75,-17) rot=(0,0,1;0rad)
  Refine = true
  Tool = -> Fusion040
FEATURE [Part::Chamfer] Chamfer031
  Base = -> Cut163
  Edges = 1 edges r=1.9: [Edge9]
FEATURE [Part::Box] Box145  label="Cube131"
  AttacherType = Attacher::AttachEngine3D
  Height = 15
  Length = 2
  Placement = pos=(433,-31,-14) rot=(0,0,1;0rad)
  Width = 6
FEATURE [Part::Box] Box146  label="Cube132"
  AttacherType = Attacher::AttachEngine3D
  Height = 20
  Length = 10
  Placement = pos=(428,-34,0) rot=(0,0,1;0rad)
  Width = 12
FEATURE [Part::Cylinder] Cylinder285
  Angle = 360
  AttacherType = Attacher::AttachEngine3D
  FirstAngle = 0
  Height = 5
  Placement = pos=(433,-28,9.25) rot=(0,1,0;1.5708rad)
  Radius = 1.6
  SecondAngle = 0
FEATURE [Part::Cylinder] Cylinder286
  Angle = 360
  AttacherType = Attacher::AttachEngine3D
  FirstAngle = 0
  Height = 5
  Placement = pos=(433,-28,15.25) rot=(0,1,0;1.5708rad)
  Radius = 1.6
  SecondAngle = 0
FEATURE [Part::Cylinder] Cylinder287
  Angle = 360
  AttacherType = Attacher::AttachEngine3D
  FirstAngle = 0
  Height = 5
  Placement = pos=(433,-28,4) rot=(0,1,0;1.5708rad)
  Radius = 1.6
  SecondAngle = 0
FEATURE [Part::Box] Box147  label="Cube133"
  AttacherType = Attacher::AttachEngine3D
  Height = 18
  Length = 9
  Placement = pos=(429,-33,1) rot=(0,0,1;0rad)
  Width = 10
FEATURE [Part::Cylinder] Cylinder288
  Angle = 360
  AttacherType = Attacher::AttachEngine3D
  FirstAngle = 0
  Height = 3
  Placement = pos=(433,-28,-14) rot=(0,1,0;1.5708rad)
  Radius = 5
  SecondAngle = 0
FEATURE [Part::Fillet] Fillet062
  Base = -> Box146
  Edges = 4 edges r=3: [Edge9,Edge10,Edge11,Edge12]
FEATURE [Part::Cylinder] Cylinder289
  Angle = 360
  AttacherType = Attacher::AttachEngine3D
  FirstAngle = 0
  Height = 50
  Placement = pos=(424,7,9) rot=(1,0,0;1.5708rad)
  Radius = 1.6
  SecondAngle = 0
FEATURE [Part::Cylinder] Cylinder290
  Angle = 45
  AttacherType = Attacher::AttachEngine3D
  FirstAngle = 0
  Height = 2.5
  Placement = pos=(381,-26.75,-24) rot=(1,0,0;1.5708rad)
  Radius = 53
  SecondAngle = 0
FEATURE [Part::Cylinder] Cylinder291
  Angle = 45
  AttacherType = Attacher::AttachEngine3D
  FirstAngle = 0
  Height = 20
  Placement = pos=(381,-18,-24) rot=(1,0,0;1.5708rad)
  Radius = 52.25
  SecondAngle = 0
FEATURE [Part::Fillet] Fillet063
  Base = -> Cylinder290
  Edges = 2 edges r=1.2: [Edge1,Edge3]
FEATURE [Part::MultiFuse] Fusion192
  Refine = true
  Shapes = -> [Cylinder291,Fillet063]
FEATURE [Part::Box] Box148  label="Cube134"
  AttacherType = Attacher::AttachEngine3D
  Height = 9
  Length = 6
  Placement = pos=(422,-33,3) rot=(0,0,1;0rad)
  Width = 8
FEATURE [Part::Box] Box149  label="Cube135"
  AttacherType = Attacher::AttachEngine3D
  Height = 2.5
  Length = 3
  Placement = pos=(421,-33,7.75) rot=(0,0,1;0rad)
  Width = 8
FEATURE [Part::Cut] Cut164
  Base = -> Box148
  Placement = pos=(0,1,0) rot=(0,0,1;0rad)
  Refine = true
  Tool = -> Box149
FEATURE [Part::Cut] Cut165
  Base = -> Cut164
  Refine = true
  Tool = -> Cylinder289
FEATURE [Part::Fillet] Fillet064
  Base = -> Cut165
  Edges = 2 edges r=1: [Edge14,Edge26]
FEATURE [Part::Fillet] Fillet065
  Base = -> Fillet064
  Edges = 3 edges r=0.75: [Edge14,Edge17,Edge31]
FEATURE [Part::Cut] Cut166
  Base = -> Fillet065
  Refine = true
  Tool = -> Fusion192
FEATURE [Part::Fillet] Fillet066  label="rear-lights-left-holder"
  Base = -> Cut166
  Edges = 4 edges r=0.2: [Edge25,Edge28,Edge34,Edge53]
FEATURE [Part::Fillet] Fillet067
  Base = -> Box147
  Edges = 4 edges r=2: [Edge9,Edge10,Edge11,Edge12]
FEATURE [Part::Cut] Cut167
  Base = -> Fillet062
  Refine = true
  Tool = -> Fillet067
FEATURE [Part::Box] Box150  label="Cube136"
  AttacherType = Attacher::AttachEngine3D
  Height = 17.5
  Length = 4.5
  Placement = pos=(433.5,-32.75,1.25) rot=(0,0,1;0rad)
  Width = 9.5
FEATURE [Part::Fillet] Fillet068
  Base = -> Box150
  Edges = 4 edges r=2: [Edge9,Edge10,Edge11,Edge12]
FEATURE [Part::Feature] Face002
  shape: bbox 2.001e-07 x 8.255 x 3.855 mm, 1 faces, 0 solids (baked)
FEATURE [Part::Feature] Face004
  Placement = pos=(-3,0,0.25) rot=(0,0,1;0rad)
  shape: bbox 2e-07 x 3.804 x 3.929 mm, 1 faces, 0 solids (baked)
FEATURE [Part::Feature] Face005
  Placement = pos=(-3,0,-5.75) rot=(0,0,1;0rad)
  shape: bbox 2e-07 x 3.804 x 3.929 mm, 1 faces, 0 solids (baked)
FEATURE [Part::Feature] Face006
  Placement = pos=(-2,0,-11) rot=(0,0,1;0rad)
  shape: bbox 2e-07 x 3.804 x 3.929 mm, 1 faces, 0 solids (baked)
FEATURE [Part::Fillet] Fillet069
  Base = -> Cylinder288
  Edges = 1 edges r=1: [Edge3]
FEATURE [Part::Fillet] Fillet070
  Base = -> Cut167
  Edges = 8 edges r=2: [Edge1,Edge2,Edge3,Edge4,Edge5,Edge6,Edge7,Edge8]
FEATURE [Part::Box] Box151  label="Cube137"
  AttacherType = Attacher::AttachEngine3D
  Height = 4
  Length = 2.5
  Placement = pos=(433.75,-31.25,-2) rot=(0,0,1;0rad)
  Width = 6.5
FEATURE [Part::Cut] Cut169
  Base = -> Fillet070
  Placement = pos=(0,0,-2) rot=(0,0,1;0rad)
  Refine = true
  Tool = -> Box151
FEATURE [Part::Feature] Face007
  shape: bbox 2.001e-07 x 9.35 x 6.05 mm, 1 faces, 0 solids (baked)
FEATURE [Part::Feature] Face008
  Placement = pos=(0,0,6) rot=(0,0,1;0rad)
  shape: bbox 2.001e-07 x 9.35 x 6.05 mm, 1 faces, 0 solids (baked)
FEATURE [Part::Loft] Loft
  Closed = false
  MaxDegree = 5
  Ruled = false
  Sections = -> [Face006,Face002]
  Solid = true
FEATURE [Part::Loft] Loft001
  Closed = false
  MaxDegree = 5
  Ruled = false
  Sections = -> [Face005,Face007]
  Solid = true
FEATURE [Part::Loft] Loft002
  Closed = false
  MaxDegree = 5
  Ruled = false
  Sections = -> [Face004,Face008]
  Solid = true
FEATURE [Part::MultiFuse] Fusion193
  Placement = pos=(-1,0,0) rot=(0,0,1;0rad)
  Refine = true
  Shapes = -> [Cylinder285,Cylinder286,Cylinder287]
FEATURE [Part::MultiFuse] Fusion194
  Refine = true
  Shapes = -> [Loft001,Fusion193,Loft,Loft002]
FEATURE [Part::Cut] Cut170  label="rear-lights-left-inner"
  Base = -> Fillet068
  Placement = pos=(0,0,-2) rot=(0,0,1;0rad)
  Refine = true
  Tool = -> Fusion194
FEATURE [Part::Box] Box152  label="Cube138"
  AttacherType = Attacher::AttachEngine3D
  Height = 4
  Length = 3
  Placement = pos=(429,-26,5) rot=(0,0,1;0rad)
  Width = 6.5
FEATURE [Part::Fillet] Fillet071
  Base = -> Box152
  Edges = 4 edges r=1: [Edge2,Edge4,Edge6,Edge8]
  Placement = pos=(0,0,-2) rot=(0,0,1;0rad)
FEATURE [Part::MultiFuse] Fusion195  label="rear-lights-left-cata"
  Placement = pos=(1,0,-2) rot=(0,0,1;0rad)
  Refine = true
  Shapes = -> [Box145,Fillet069]
FEATURE [Part::Box] Box153  label="Cube139"
  AttacherType = Attacher::AttachEngine3D
  Height = 18.2
  Length = 4.6
  Placement = pos=(433.4,-33.1,0.9) rot=(0,0,1;0rad)
  Width = 10.2
FEATURE [Part::Fillet] Fillet072
  Base = -> Box153
  Edges = 4 edges r=2: [Edge9,Edge10,Edge11,Edge12]
  Placement = pos=(0,0,-2) rot=(0,0,1;0rad)
FEATURE [Part::Cut] Cut171
  Base = -> Cut169
  Refine = true
  Tool = -> Fillet072
FEATURE [Part::Cut] Cut172  label="rear-lights-left-case"
  Base = -> Cut171
  Refine = true
  Tool = -> Fillet071
FEATURE [Part::Box] Box154  label="Cube140"
  AttacherType = Attacher::AttachEngine3D
  Height = 20
  Length = 10
  Placement = pos=(428,-34,0) rot=(0,0,1;0rad)
  Width = 12
FEATURE [Part::Box] Box155  label="Cube141"
  AttacherType = Attacher::AttachEngine3D
  Height = 18
  Length = 9
  Placement = pos=(429,-33,1) rot=(0,0,1;0rad)
  Width = 10
FEATURE [Part::Fillet] Fillet073
  Base = -> Box154
  Edges = 4 edges r=3: [Edge9,Edge10,Edge11,Edge12]
FEATURE [Part::Fillet] Fillet074
  Base = -> Box155
  Edges = 4 edges r=2: [Edge9,Edge10,Edge11,Edge12]
FEATURE [Part::Cut] Cut173
  Base = -> Fillet073
  Refine = true
  Tool = -> Fillet074
FEATURE [Part::Fillet] Fillet075
  Base = -> Cut173
  Edges = 8 edges r=2: [Edge1,Edge2,Edge3,Edge4,Edge5,Edge6,Edge7,Edge8]
FEATURE [Part::Box] Box156  label="Cube142"
  AttacherType = Attacher::AttachEngine3D
  Height = 4
  Length = 2.5
  Placement = pos=(433.75,-31.25,-2) rot=(0,0,1;0rad)
  Width = 6.5
FEATURE [Part::Cut] Cut174
  Base = -> Fillet075
  Placement = pos=(0,0,-2) rot=(0,0,1;0rad)
  Refine = true
  Tool = -> Box156
FEATURE [Part::Box] Box157  label="Cube143"
  AttacherType = Attacher::AttachEngine3D
  Height = 4
  Length = 3
  Placement = pos=(429,-26,5) rot=(0,0,1;0rad)
  Width = 6.5
FEATURE [Part::Fillet] Fillet076
  Base = -> Box157
  Edges = 4 edges r=1: [Edge2,Edge4,Edge6,Edge8]
  Placement = pos=(0,-9,-2) rot=(0,0,1;0rad)
FEATURE [Part::Box] Box158  label="Cube144"
  AttacherType = Attacher::AttachEngine3D
  Height = 18.2
  Length = 4.6
  Placement = pos=(433.4,-33.1,0.9) rot=(0,0,1;0rad)
  Width = 10.2
FEATURE [Part::Fillet] Fillet077
  Base = -> Box158
  Edges = 4 edges r=2: [Edge9,Edge10,Edge11,Edge12]
  Placement = pos=(0,0,-2) rot=(0,0,1;0rad)
FEATURE [Part::Cut] Cut175
  Base = -> Cut174
  Refine = true
  Tool = -> Fillet077
FEATURE [Part::Cut] Cut176  label="rear-lights-right-case"
  Base = -> Cut175
  Placement = pos=(0,136,0) rot=(0,0,1;0rad)
  Refine = true
  Tool = -> Fillet076
FEATURE [Part::Cylinder] Cylinder292
  Angle = 360
  AttacherType = Attacher::AttachEngine3D
  FirstAngle = 0
  Height = 5
  Placement = pos=(433,-28,9.25) rot=(0,1,0;1.5708rad)
  Radius = 1.6
  SecondAngle = 0
FEATURE [Part::Cylinder] Cylinder293
  Angle = 360
  AttacherType = Attacher::AttachEngine3D
  FirstAngle = 0
  Height = 5
  Placement = pos=(433,-28,15.25) rot=(0,1,0;1.5708rad)
  Radius = 1.6
  SecondAngle = 0
FEATURE [Part::Cylinder] Cylinder294
  Angle = 360
  AttacherType = Attacher::AttachEngine3D
  FirstAngle = 0
  Height = 5
  Placement = pos=(433,-28,4) rot=(0,1,0;1.5708rad)
  Radius = 1.6
  SecondAngle = 0
FEATURE [Part::Box] Box159  label="Cube145"
  AttacherType = Attacher::AttachEngine3D
  Height = 17.5
  Length = 4.5
  Placement = pos=(433.5,-32.75,1.25) rot=(0,0,1;0rad)
  Width = 9.5
FEATURE [Part::Fillet] Fillet078
  Base = -> Box159
  Edges = 4 edges r=2: [Edge9,Edge10,Edge11,Edge12]
FEATURE [Part::Feature] Face009
  shape: bbox 2.001e-07 x 8.255 x 3.855 mm, 1 faces, 0 solids (baked)
FEATURE [Part::Feature] Face010
  Placement = pos=(-3,0,0.25) rot=(0,0,1;0rad)
  shape: bbox 2e-07 x 3.804 x 3.929 mm, 1 faces, 0 solids (baked)
FEATURE [Part::Feature] Face011
  Placement = pos=(-3,0,-5.75) rot=(0,0,1;0rad)
  shape: bbox 2e-07 x 3.804 x 3.929 mm, 1 faces, 0 solids (baked)
FEATURE [Part::Feature] Face012
  Placement = pos=(-2,0,-11) rot=(0,0,1;0rad)
  shape: bbox 2e-07 x 3.804 x 3.929 mm, 1 faces, 0 solids (baked)
FEATURE [Part::Feature] Face013
  shape: bbox 2.001e-07 x 9.35 x 6.05 mm, 1 faces, 0 solids (baked)
FEATURE [Part::Feature] Face014
  Placement = pos=(0,0,6) rot=(0,0,1;0rad)
  shape: bbox 2.001e-07 x 9.35 x 6.05 mm, 1 faces, 0 solids (baked)
FEATURE [Part::Loft] Loft003
  Closed = false
  MaxDegree = 5
  Ruled = false
  Sections = -> [Face012,Face009]
  Solid = true
FEATURE [Part::Loft] Loft004
  Closed = false
  MaxDegree = 5
  Ruled = false
  Sections = -> [Face011,Face013]
  Solid = true
FEATURE [Part::Loft] Loft005
  Closed = false
  MaxDegree = 5
  Ruled = false
  Sections = -> [Face010,Face014]
  Solid = true
FEATURE [Part::MultiFuse] Fusion196
  Placement = pos=(-1,0,0) rot=(0,0,1;0rad)
  Refine = true
  Shapes = -> [Cylinder292,Cylinder293,Cylinder294]
FEATURE [Part::MultiFuse] Fusion197
  Refine = true
  Shapes = -> [Loft004,Fusion196,Loft003,Loft005]
FEATURE [Part::Cut] Cut177  label="rear-lights-right-inner"
  Base = -> Fillet078
  Placement = pos=(0,136,-2) rot=(0,0,1;0rad)
  Refine = true
  Tool = -> Fusion197
FEATURE [Part::Box] Box160  label="Cube146"
  AttacherType = Attacher::AttachEngine3D
  Height = 15
  Length = 2
  Placement = pos=(433,-31,-14) rot=(0,0,1;0rad)
  Width = 6
FEATURE [Part::Cylinder] Cylinder295
  Angle = 360
  AttacherType = Attacher::AttachEngine3D
  FirstAngle = 0
  Height = 3
  Placement = pos=(433,-28,-14) rot=(0,1,0;1.5708rad)
  Radius = 5
  SecondAngle = 0
FEATURE [Part::Fillet] Fillet079
  Base = -> Cylinder295
  Edges = 1 edges r=1: [Edge3]
FEATURE [Part::MultiFuse] Fusion198  label="rear-lights-right-cata"
  Placement = pos=(1,136,-2) rot=(0,0,1;0rad)
  Refine = true
  Shapes = -> [Box160,Fillet079]
FEATURE [Part::Cylinder] Cylinder296
  Angle = 360
  AttacherType = Attacher::AttachEngine3D
  FirstAngle = 0
  Height = 50
  Placement = pos=(424,7,9) rot=(1,0,0;1.5708rad)
  Radius = 1.6
  SecondAngle = 0
FEATURE [Part::Cylinder] Cylinder297
  Angle = 45
  AttacherType = Attacher::AttachEngine3D
  FirstAngle = 0
  Height = 2.5
  Placement = pos=(381,-26.75,-24) rot=(1,0,0;1.5708rad)
  Radius = 53
  SecondAngle = 0
FEATURE [Part::Cylinder] Cylinder298
  Angle = 45
  AttacherType = Attacher::AttachEngine3D
  FirstAngle = 0
  Height = 20
  Placement = pos=(381,-18,-24) rot=(1,0,0;1.5708rad)
  Radius = 52.25
  SecondAngle = 0
FEATURE [Part::Fillet] Fillet080
  Base = -> Cylinder297
  Edges = 2 edges r=1.2: [Edge1,Edge3]
FEATURE [Part::MultiFuse] Fusion199
  Refine = true
  Shapes = -> [Cylinder298,Fillet080]
FEATURE [Part::Box] Box161  label="Cube147"
  AttacherType = Attacher::AttachEngine3D
  Height = 9
  Length = 6
  Placement = pos=(422,-33,3) rot=(0,0,1;0rad)
  Width = 8
FEATURE [Part::Box] Box162  label="Cube148"
  AttacherType = Attacher::AttachEngine3D
  Height = 2.5
  Length = 3
  Placement = pos=(421,-33,7.75) rot=(0,0,1;0rad)
  Width = 8
FEATURE [Part::Cut] Cut178
  Base = -> Box161
  Placement = pos=(0,1,0) rot=(0,0,1;0rad)
  Refine = true
  Tool = -> Box162
FEATURE [Part::Cut] Cut179
  Base = -> Cut178
  Refine = true
  Tool = -> Cylinder296
FEATURE [Part::Fillet] Fillet081
  Base = -> Cut179
  Edges = 2 edges r=1: [Edge14,Edge26]
FEATURE [Part::Fillet] Fillet082
  Base = -> Fillet081
  Edges = 3 edges r=0.75: [Edge14,Edge17,Edge31]
FEATURE [Part::Cut] Cut180
  Base = -> Fillet082
  Refine = true
  Tool = -> Fusion199
FEATURE [Part::Fillet] Fillet083  label="rear-lights-right-holder"
  Base = -> Cut180
  Edges = 4 edges r=0.2: [Edge25,Edge28,Edge34,Edge53]
  Placement = pos=(0,136,0) rot=(0,0,1;0rad)
FEATURE [Part::Box] Box163  label="Cube149"
  AttacherType = Attacher::AttachEngine3D
  Height = 20
  Length = 0.8
  Placement = pos=(428,-34,0) rot=(0,0,1;0rad)
  Width = 12
FEATURE [Part::Fillet] Fillet084
  Base = -> Box163
  Edges = 4 edges r=3: [Edge9,Edge10,Edge11,Edge12]
  Placement = pos=(10,0,-2) rot=(0,0,1;0rad)
FEATURE [Part::Box] Box164  label="Cube150"
  AttacherType = Attacher::AttachEngine3D
  Height = 0.5
  Length = 1.2
  Placement = pos=(438,-33.5,3.8) rot=(0,0,1;0rad)
  Width = 11
FEATURE [Part::Box] Box165  label="Cube151"
  AttacherType = Attacher::AttachEngine3D
  Height = 0.5
  Length = 1.2
  Placement = pos=(438,-33.5,10) rot=(0,0,1;0rad)
  Width = 11
FEATURE [Part::Fillet] Fillet085
  Base = -> Fillet084
  Edges = 4 edges r=0.79: [Edge9,Edge17,Edge19,Edge24]
FEATURE [Part::MultiFuse] Fusion200
  Refine = true
  Shapes = -> [Box164,Box165]
FEATURE [Part::Fillet] Fillet086
  Base = -> Fusion200
  Edges = 4 edges r=1: [Edge5,Edge7,Edge17,Edge19]
FEATURE [Part::Fillet] Fillet087
  Base = -> Fillet086
  Edges = 4 edges r=0.2: [Edge1,Edge4,Edge19,Edge22]
FEATURE [Part::MultiFuse] Fusion201  label="rear-lights-right-transparent-cover"
  Placement = pos=(0,136,0) rot=(0,0,1;0rad)
  Refine = true
  Shapes = -> [Fillet085,Fillet087]
FEATURE [Part::Box] Box166  label="Cube152"
  AttacherType = Attacher::AttachEngine3D
  Height = 20
  Length = 0.8
  Placement = pos=(428,-34,0) rot=(0,0,1;0rad)
  Width = 12
FEATURE [Part::Fillet] Fillet088
  Base = -> Box166
  Edges = 4 edges r=3: [Edge9,Edge10,Edge11,Edge12]
  Placement = pos=(10,0,-2) rot=(0,0,1;0rad)
FEATURE [Part::Box] Box167  label="Cube153"
  AttacherType = Attacher::AttachEngine3D
  Height = 0.5
  Length = 1.2
  Placement = pos=(438,-33.5,3.8) rot=(0,0,1;0rad)
  Width = 11
FEATURE [Part::Box] Box168  label="Cube154"
  AttacherType = Attacher::AttachEngine3D
  Height = 0.5
  Length = 1.2
  Placement = pos=(438,-33.5,10) rot=(0,0,1;0rad)
  Width = 11
FEATURE [Part::Fillet] Fillet089
  Base = -> Fillet088
  Edges = 4 edges r=0.79: [Edge9,Edge17,Edge19,Edge24]
FEATURE [Part::MultiFuse] Fusion202
  Refine = true
  Shapes = -> [Box167,Box168]
FEATURE [Part::Fillet] Fillet090
  Base = -> Fusion202
  Edges = 4 edges r=1: [Edge5,Edge7,Edge17,Edge19]
FEATURE [Part::Fillet] Fillet091
  Base = -> Fillet090
  Edges = 4 edges r=0.2: [Edge1,Edge4,Edge19,Edge22]
FEATURE [Part::MultiFuse] Fusion203  label="rear-lights-left-transparent-cover"
  Refine = true
  Shapes = -> [Fillet089,Fillet091]
FEATURE [Part::Cylinder] Cylinder299
  Angle = 360
  AttacherType = Attacher::AttachEngine3D
  FirstAngle = 0
  Height = 0.8
  Placement = pos=(437,-28,-16) rot=(0,1,0;1.5708rad)
  Radius = 4.5
  SecondAngle = 0
FEATURE [Part::Fillet] Fillet092  label="rear-lights-left-transparent-cata"
  Base = -> Cylinder299
  Edges = 1 edges r=0.5: [Edge1]
FEATURE [Part::Cylinder] Cylinder300
  Angle = 360
  AttacherType = Attacher::AttachEngine3D
  FirstAngle = 0
  Height = 0.8
  Placement = pos=(437,-28,-16) rot=(0,1,0;1.5708rad)
  Radius = 4.5
  SecondAngle = 0
FEATURE [Part::Fillet] Fillet093  label="rear-lights-right-transparent-cata"
  Base = -> Cylinder300
  Edges = 1 edges r=0.5: [Edge1]
  Placement = pos=(0,136,0) rot=(0,0,1;0rad)
FEATURE [Part::Box] Box169  label="Cube155"
  AttacherType = Attacher::AttachEngine3D
  Height = 1
  Length = 5
  Placement = pos=(400,1.5,1.5) rot=(0,0,1;0rad)
  Width = 7
FEATURE [Part::Cylinder] Cylinder301
  Angle = 360
  AttacherType = Attacher::AttachEngine3D
  FirstAngle = 0
  Height = 11
  Placement = pos=(400,5,-0.5) rot=(0,1,0;1.5708rad)
  Radius = 2
  SecondAngle = 0
FEATURE [Part::Box] Box171  label="Cube157"
  AttacherType = Attacher::AttachEngine3D
  Height = 4.5
  Length = 5
  Placement = pos=(400,2,-3) rot=(0,0,1;0rad)
  Width = 6
FEATURE [Part::MultiFuse] Fusion204
  Refine = true
  Shapes = -> [Box169,Box171]
FEATURE [Part::Cut] Cut181
  Base = -> Fusion204
  Refine = true
  Tool = -> Cylinder301
FEATURE [Part::Fillet] Fillet094  label="wiring-holder-001"
  Base = -> Cut181
  Edges = 2 edges r=2: [Edge23,Edge26]
  Placement = pos=(0,0,21) rot=(0,1,0;0.05236rad)
FEATURE [Part::Box] Box172  label="Cube158"
  AttacherType = Attacher::AttachEngine3D
  Height = 1
  Length = 5
  Placement = pos=(400,1.5,1.5) rot=(0,0,1;0rad)
  Width = 7
FEATURE [Part::Cylinder] Cylinder303
  Angle = 360
  AttacherType = Attacher::AttachEngine3D
  FirstAngle = 0
  Height = 11
  Placement = pos=(400,5,-0.5) rot=(0,1,0;1.5708rad)
  Radius = 2
  SecondAngle = 0
FEATURE [Part::Box] Box173  label="Cube159"
  AttacherType = Attacher::AttachEngine3D
  Height = 4.5
  Length = 5
  Placement = pos=(400,2,-3) rot=(0,0,1;0rad)
  Width = 6
FEATURE [Part::MultiFuse] Fusion205
  Refine = true
  Shapes = -> [Box172,Box173]
FEATURE [Part::Cut] Cut182
  Base = -> Fusion205
  Refine = true
  Tool = -> Cylinder303
FEATURE [Part::Fillet] Fillet095  label="wiring-holder-002"
  Base = -> Cut182
  Edges = 2 edges r=2: [Edge23,Edge26]
  Placement = pos=(0,70,21) rot=(0,1,0;0.05236rad)
FEATURE [Part::Box] Box174  label="Cube160"
  AttacherType = Attacher::AttachEngine3D
  Height = 1
  Length = 5
  Placement = pos=(400,1.5,1.5) rot=(0,0,1;0rad)
  Width = 7
FEATURE [Part::Cylinder] Cylinder304
  Angle = 360
  AttacherType = Attacher::AttachEngine3D
  FirstAngle = 0
  Height = 11
  Placement = pos=(400,5,-0.5) rot=(0,1,0;1.5708rad)
  Radius = 2
  SecondAngle = 0
FEATURE [Part::Box] Box175  label="Cube161"
  AttacherType = Attacher::AttachEngine3D
  Height = 5
  Length = 5
  Placement = pos=(400,2,-3.5) rot=(0,0,1;0rad)
  Width = 6
FEATURE [Part::MultiFuse] Fusion206
  Refine = true
  Shapes = -> [Box174,Box175]
FEATURE [Part::Cut] Cut183
  Base = -> Fusion206
  Refine = true
  Tool = -> Cylinder304
FEATURE [Part::Fillet] Fillet096  label="wiring-holder-003_"
  Base = -> Cut183
  Edges = 2 edges r=2: [Edge23,Edge26]
  Placement = pos=(331,-363,-1) rot=(0,0,1;1.5708rad)
FEATURE [Part::Box] Box176  label="Cube162"
  AttacherType = Attacher::AttachEngine3D
  Height = 1
  Length = 5
  Placement = pos=(400,1.5,1.5) rot=(0,0,1;0rad)
  Width = 7
FEATURE [Part::Cylinder] Cylinder305
  Angle = 360
  AttacherType = Attacher::AttachEngine3D
  FirstAngle = 0
  Height = 11
  Placement = pos=(400,5,-0.5) rot=(0,1,0;1.5708rad)
  Radius = 2
  SecondAngle = 0
FEATURE [Part::Box] Box177  label="Cube163"
  AttacherType = Attacher::AttachEngine3D
  Height = 8
  Length = 5
  Placement = pos=(400,2,-6.5) rot=(0,0,1;0rad)
  Width = 6
FEATURE [Part::Cylinder] Cylinder306
  Angle = 360
  AttacherType = Attacher::AttachEngine3D
  FirstAngle = 0
  Height = 11
  Placement = pos=(400,5,-3.5) rot=(0,1,0;1.5708rad)
  Radius = 2
  SecondAngle = 0
FEATURE [Part::MultiFuse] Fusion207
  Refine = true
  Shapes = -> [Box176,Box177]
FEATURE [Part::MultiFuse] Fusion208
  Refine = true
  Shapes = -> [Cylinder306,Cylinder305]
FEATURE [Part::Cut] Cut184
  Base = -> Fusion207
  Refine = true
  Tool = -> Fusion208
FEATURE [Part::Fillet] Fillet097  label="wiring-holder-004_"
  Base = -> Cut184
  Edges = 2 edges r=2: [Edge26,Edge29]
  Placement = pos=(-206,70,-2.5) rot=(0,0,1;0rad)
FEATURE [Part::Box] Box178  label="Cube164"
  AttacherType = Attacher::AttachEngine3D
  Height = 1
  Length = 5
  Placement = pos=(400,1.5,1.5) rot=(0,0,1;0rad)
  Width = 7
FEATURE [Part::Cylinder] Cylinder307
  Angle = 360
  AttacherType = Attacher::AttachEngine3D
  FirstAngle = 0
  Height = 11
  Placement = pos=(400,5,-0.5) rot=(0,1,0;1.5708rad)
  Radius = 2
  SecondAngle = 0
FEATURE [Part::Box] Box179  label="Cube165"
  AttacherType = Attacher::AttachEngine3D
  Height = 7.5
  Length = 5
  Placement = pos=(400,2,-6) rot=(0,0,1;0rad)
  Width = 6
FEATURE [Part::Cylinder] Cylinder308
  Angle = 360
  AttacherType = Attacher::AttachEngine3D
  FirstAngle = 0
  Height = 11
  Placement = pos=(400,5,-3.5) rot=(0,1,0;1.5708rad)
  Radius = 2
  SecondAngle = 0
FEATURE [Part::MultiFuse] Fusion209
  Refine = true
  Shapes = -> [Box178,Box179]
FEATURE [Part::MultiFuse] Fusion210
  Refine = true
  Shapes = -> [Cylinder308,Cylinder307]
FEATURE [Part::Cut] Cut185
  Base = -> Fusion209
  Refine = true
  Tool = -> Fusion210
FEATURE [Part::Fillet] Fillet098  label="wiring-holder-005"
  Base = -> Cut185
  Edges = 2 edges r=2: [Edge26,Edge29]
  Placement = pos=(-115,70,-2.5) rot=(0,0,1;0rad)
FEATURE [Part::Box] Box180  label="Cube166"
  AttacherType = Attacher::AttachEngine3D
  Height = 3
  Length = 5
  Placement = pos=(321,37,-2.5) rot=(0,0,1;0rad)
  Width = 5
FEATURE [Part::Cut] Cut186  label="wiring-holder-003"
  Base = -> Fillet096
  Refine = true
  Tool = -> Box180
FEATURE [Part::Box] Box181  label="Cube167"
  AttacherType = Attacher::AttachEngine3D
  Height = 3
  Length = 5
  Placement = pos=(194,70,-4) rot=(0,0,1;0rad)
  Width = 5
FEATURE [Part::Cut] Cut187  label="wiring-holder-004"
  Base = -> Fillet097
  Refine = true
  Tool = -> Box181
FEATURE [Part::Feature] Cut017001  label="cab-lower"
  Placement = pos=(-13.5,-44,17) rot=(0,0,1;0rad)
  shape: bbox 150.8 x 170 x 64 mm, 404 faces (baked)
FEATURE [Part::Feature] Fusion009001  label="cab-upper"
  Placement = pos=(-13.5,-44,17) rot=(0,0,1;0rad)
  shape: bbox 159.3 x 176.2 x 65.76 mm, 242 faces (baked)
FEATURE [Part::Feature] Cut085001  label="radiator-grid001"
  Placement = pos=(-13.5,-44,17) rot=(0,0,1;0rad)
  shape: bbox 0.5 x 124 x 29 mm, 3587 faces (baked)
FEATURE [Part::Feature] Fusion074001  label="radiator-mask001"
  Placement = pos=(-13.5,-44,17) rot=(0,0,1;0rad)
  shape: bbox 4.5 x 126 x 31 mm, 100 faces (baked)
FEATURE [Part::Feature] Cut103001  label="bumper001"
  Placement = pos=(-13.5,-44,17) rot=(0,0,1;0rad)
  shape: bbox 22.15 x 166.3 x 22 mm, 70 faces (baked)
FEATURE [Part::Feature] Cut113001  label="left-wing001"
  Placement = pos=(-13.5,-43,17) rot=(0,0,1;0rad)
  shape: bbox 132.1 x 40 x 63.52 mm, 38 faces (baked)
FEATURE [Part::Feature] Cut114001  label="right-wing001"
  Placement = pos=(-13.5,-45,17) rot=(0,0,1;0rad)
  shape: bbox 132.1 x 40 x 63.52 mm, 38 faces (baked)
FEATURE [Part::Feature] Cut136001  label="roof_003"
  Placement = pos=(-13.5,-44,17) rot=(0,0,1;0rad)
  shape: bbox 128 x 158 x 11 mm, 45 faces (baked)
FEATURE [Part::Feature] Cut138001  label="front-lights-right-proyector"
  Placement = pos=(-12.5,-43.5,17) rot=(0,0,1;0rad)
  shape: bbox 6.204 x 21.46 x 15.99 mm, 23 faces (baked)
FEATURE [Part::Feature] Fillet133001  label="front-lights-right-glass"
  Placement = pos=(-12.5,-43.5,17) rot=(0,0,1;0rad)
  shape: bbox 0.684 x 20.49 x 14.49 mm, 18 faces (baked)
FEATURE [Part::Feature] Cut140001  label="front-lights-right-proyector-holder"
  Placement = pos=(-13.5,-44,17) rot=(0,0,1;0rad)
  shape: bbox 3 x 23 x 19 mm, 13 faces (baked)
FEATURE [Part::Feature] Part__Mirroring016001  label="front-lights-left-proyector-holder"
  Placement = pos=(-13.5,124,17) rot=(0,0,1;0rad)
  shape: bbox 3 x 23 x 19 mm, 13 faces (baked)
FEATURE [Part::Feature] Compound001  label="rim-front-left"
  Placement = pos=(84,-27,-26) rot=(1,0,0;1.5708rad)
  shape: bbox 47 x 23 x 47 mm, 428 faces, 3 solids (baked)
FEATURE [Part::Feature] Compound002  label="rim-rear-left"
  Placement = pos=(380,-49,-26) rot=(1,0,0;1.5708rad)
  shape: bbox 47 x 44 x 47 mm, 615 faces, 24 solids (baked)
FEATURE [Part::Feature] Chamfer314003  label="wheel-front-left"
  Placement = pos=(9.5,40,9) rot=(0,0,1;0rad)
  shape: bbox 88.76 x 22 x 88.76 mm, 8 faces (baked)
FEATURE [Part::Feature] Chamfer314004  label="wheel-rear-external-left"
  Placement = pos=(305.5,38,9) rot=(0,0,1;0rad)
  shape: bbox 88.76 x 22 x 88.76 mm, 8 faces (baked)
FEATURE [Part::Feature] Chamfer314005  label="wheel-middle-left"
  Placement = pos=(123.5,40,9) rot=(0,0,1;0rad)
  shape: bbox 88.76 x 22 x 88.76 mm, 8 faces (baked)
FEATURE [Part::Feature] Chamfer314006  label="wheel-rear-internal-left"
  Placement = pos=(305.5,62,9) rot=(0,0,1;0rad)
  shape: bbox 88.76 x 22 x 88.76 mm, 8 faces (baked)
FEATURE [Part::Feature] Chamfer314007  label="wheel-front-right"
  Placement = pos=(9.5,194,9) rot=(0,0,1;0rad)
  shape: bbox 88.76 x 22 x 88.76 mm, 8 faces (baked)
FEATURE [Part::Feature] Chamfer314008  label="wheel-rear-external-right"
  Placement = pos=(305.5,196,9) rot=(0,0,1;0rad)
  shape: bbox 88.76 x 22 x 88.76 mm, 8 faces (baked)
FEATURE [Part::Feature] Chamfer314009  label="wheel-middle-right"
  Placement = pos=(123.5,194,9) rot=(0,0,1;0rad)
  shape: bbox 88.76 x 22 x 88.76 mm, 8 faces (baked)
FEATURE [Part::Feature] Chamfer314010  label="wheel-rear-internal-right"
  Placement = pos=(305.5,172,9) rot=(0,0,1;0rad)
  shape: bbox 88.76 x 22 x 88.76 mm, 8 faces (baked)
FEATURE [Part::Feature] Compound003  label="rim-middle-left"
  Placement = pos=(198,-27,-26) rot=(1,0,0;1.5708rad)
  shape: bbox 47 x 23 x 47 mm, 428 faces, 3 solids (baked)
FEATURE [Part::Feature] Part__Mirroring016002001  label="rim-front-right"
  Placement = pos=(0,80,0) rot=(0,0,1;0rad)
  shape: bbox 47 x 23 x 47 mm, 428 faces, 3 solids (baked)
FEATURE [Part::Feature] Part__Mirroring016003001  label="rim-rear-right"
  Placement = pos=(0,80,0) rot=(0,0,1;0rad)
  shape: bbox 47 x 44 x 47 mm, 615 faces, 24 solids (baked)
FEATURE [Part::Feature] Part__Mirroring016004001  label="rim-middle-right"
  Placement = pos=(0,80,0) rot=(0,0,1;0rad)
  shape: bbox 47 x 23 x 47 mm, 428 faces, 3 solids (baked)
FEATURE [Part::Feature] Fusion500001  label="front-axle"
  Placement = pos=(-264,-45,25) rot=(0,0,1;0rad)
  shape: bbox 15 x 143 x 21.5 mm, 74 faces (baked)
FEATURE [Part::Feature] Fusion500002  label="central-axle"
  Placement = pos=(-150,-45,25) rot=(0,0,1;0rad)
  shape: bbox 15 x 143 x 21.5 mm, 74 faces (baked)
FEATURE [Part::Feature] Cut110001  label="leafspring-front-right"
  Placement = pos=(25,81,-28) rot=(1,0,0;1.5708rad)
  shape: bbox 105 x 7 x 15.8 mm, 6 faces (baked)
FEATURE [Part::Feature] Cut140002  label="leafspring-front-left"
  Placement = pos=(25,6,-28) rot=(1,0,0;1.5708rad)
  shape: bbox 105 x 7 x 15.8 mm, 6 faces (baked)
FEATURE [Part::Feature] Cut140003  label="leafspring-front-right"
  Placement = pos=(141,81,-28) rot=(1,0,0;1.5708rad)
  shape: bbox 105 x 7 x 15.8 mm, 6 faces (baked)
FEATURE [Part::Feature] Cut140004  label="leafspring-front-left"
  Placement = pos=(141,6,-28) rot=(1,0,0;1.5708rad)
  shape: bbox 105 x 7 x 15.8 mm, 6 faces (baked)
FEATURE [Part::Feature] Chamfer314011  label="wheel-spare"
  Placement = pos=(217.5,-41,42) rot=(1,0,0;1.5708rad)
  shape: bbox 88.76 x 88.76 x 22 mm, 8 faces (baked)
FEATURE [Part::Feature] Compound004  label="rim-spare"
  Placement = pos=(292,-6,-45) rot=(1,0,0;0rad)
  shape: bbox 47 x 47 x 23 mm, 428 faces, 3 solids (baked)
FEATURE [App::DocumentObjectGroup] Group  label="Wheels"
  Group = -> [Chamfer314003,Chamfer314004,Chamfer314005,Chamfer314006,Chamfer314007,Chamfer314008,Chamfer314009,Chamfer314010,Compound003,Part__Mirroring016002001,Part__Mirroring016003001,Part__Mirroring016004001,Compound001,Compound002,Chamfer314011,Compound004]
FEATURE [Part::Feature] Fusion035002001  label="fuel-tank"
  Placement = pos=(189,0,-2.5) rot=(0,0,1;0rad)
  shape: bbox 77 x 62.7 x 49.7 mm, 153 faces (baked)
FEATURE [App::DocumentObjectGroup] Group004  label="Fifth wheel"
  Group = -> [Cut157,Cut155,Cut154,Cut147,Fillet048]
FEATURE [App::DocumentObjectGroup] Group005  label="Rear lights"
  Group = -> [Fillet066,Cut170,Fusion195,Cut172,Cut176,Cut177,Fusion198,Fillet083,Fusion201,Fusion203,Fillet092,Fillet093]
FEATURE [App::DocumentObjectGroup] Group006  label="Suspensions"
  Group = -> [Fusion120,Fusion121,Chamfer011,Chamfer012,Chamfer015,Chamfer016,Chamfer021,Part__Mirroring005,Cut110001,Cut140002,Cut140003,Cut140004]
FEATURE [App::DocumentObjectGroup] Group007  label="Fenders"
  Group = -> [Cut143,Fusion072,Part__Mirroring010,Cut085]
FEATURE [App::DocumentObjectGroup] Group008  label="Air tank, battery box, fuel tank"
  Group = -> [Cut125,Cut133,Cut138,Cut119,Fillet050,Cut121,Fusion035002001]
FEATURE [App::DocumentObjectGroup] Group009  label="Tools"
  Group = -> [Cut091]
FEATURE [Part::Feature] Fusion046002  label="steering-lever-holder-rear"
  Placement = pos=(169,84,23) rot=(0.57735,-0.57735,-0.57735;4.18879rad)
  shape: bbox 32 x 10 x 9 mm, 26 faces (baked)
FEATURE [Part::Feature] Fillet003001  label="steering-lever-front"
  Placement = pos=(55,84,22.5) rot=(0.57735,-0.57735,-0.57735;4.18879rad)
  shape: bbox 11 x 5 x 49 mm, 31 faces (baked)
FEATURE [Part::Feature] Fillet004001  label="steering-lever-rear"
  Placement = pos=(194,84,22.5) rot=(0.57735,-0.57735,-0.57735;4.18879rad)
  shape: bbox 11 x 5 x 44.5 mm, 23 faces (baked)
FEATURE [Part::Feature] Cut037001  label="steering-arm-rear"
  Placement = pos=(183,107,-26) rot=(0,0,1;3.14159rad)
  shape: bbox 45 x 28.5 x 11 mm, 48 faces (baked)
FEATURE [Part::Feature] Fusion046001  label="steering-lever-holder-front"
  Placement = pos=(55,84,23) rot=(0.57735,-0.57735,-0.57735;4.18879rad)
  shape: bbox 32 x 10 x 9 mm, 26 faces (baked)
FEATURE [Part::Part2DObjectPython] Line014  label="joint-steering-front-right-wheel"  # Draft 2D object (typed FeaturePython)
  Closed = true
  End = (84,107,-47)
  FilletRadius = 0
  MapMode = 5
  Placement = pos=(84,-33,-31) rot=(0,0,1;0rad)
  Points = (2) [(0,140,24),(0,140,-16)]
  Start = (84,107,-7)
FEATURE [Part::Part2DObjectPython] Line015  label="joint-steering-rear-right-wheel"  # Draft 2D object (typed FeaturePython)
  Closed = true
  End = (198,107,-47)
  FilletRadius = 0
  MapMode = 5
  Placement = pos=(198,-33,-31) rot=(0,0,1;0rad)
  Points = (2) [(0,140,24),(0,140,-16)]
  Start = (198,107,-7)
FEATURE [Part::Feature] Cut140005  label="steering-arm-front"
  Placement = pos=(69,107,-26) rot=(0,0,1;3.14159rad)
  shape: bbox 45 x 28.5 x 11 mm, 48 faces (baked)
FEATURE [Part::Cylinder] Cylinder309  label="Cylinder"
  Angle = 360
  AttacherType = Attacher::AttachEngine3D
  FirstAngle = 0
  Height = 11.5
  Placement = pos=(-1,0,45) rot=(0,1,0;1.5708rad)
  Radius = 3
  SecondAngle = 0
FEATURE [Part::Cylinder] Cylinder310  label="Cylinder"
  Angle = 360
  AttacherType = Attacher::AttachEngine3D
  FirstAngle = 0
  Height = 4
  Placement = pos=(-3,0,43) rot=(0,1,0;0rad)
  Radius = 4.5
  SecondAngle = 0
FEATURE [Part::Cylinder] Cylinder311  label="Cylinder"
  Angle = 360
  AttacherType = Attacher::AttachEngine3D
  FirstAngle = 0
  Height = 4
  Placement = pos=(-3,0,43) rot=(0,1,0;0rad)
  Radius = 2
  SecondAngle = 0
FEATURE [Part::Cut] Cut140006
  Base = -> Cylinder310
  Refine = true
  Tool = -> Cylinder311
FEATURE [Part::Chamfer] Chamfer314012
  Base = -> Cylinder309
  Edges = 1 edges r=1: [Edge2]
FEATURE [Part::Fillet] Fillet133002
  Base = -> Cut140006
  Edges = 2 edges r=0.5: [Edge2,Edge3]
FEATURE [Part::MultiFuse] Fusion035002002  label="UNIBALL"
  Refine = true
  Shapes = -> [Chamfer314012,Fillet133002]
FEATURE [App::DocumentObjectGroup] Group010  label="Parts"
  Group = -> [Box043,Chamfer029,Chamfer030,Chamfer031,Fusion170,Fusion035002002]
FEATURE [Part::Feature] Fusion035002002002  label="UNIBALL"
  Placement = pos=(195,87,-56) rot=(0,0,1;3.14159rad)
  shape: bbox 18.37 x 9.742 x 6 mm, 11 faces (baked)
FEATURE [Part::Feature] Fusion035002002004  label="UNIBALL"
  Placement = pos=(172,132,-11) rot=(1,0,0;1.5708rad)
  shape: bbox 18.37 x 6 x 9.742 mm, 11 faces (baked)
FEATURE [Part::Feature] Fusion035002002005  label="UNIBALL"
  Placement = pos=(165.95,136,20.5) rot=(0,0.707107,-0.707107;3.14159rad)
  shape: bbox 18.37 x 6 x 9.742 mm, 11 faces (baked)
FEATURE [Part::Feature] Fusion035002002006  label="UNIBALL"
  Placement = pos=(58,136,20.5) rot=(1,0,0;1.5708rad)
  shape: bbox 18.37 x 6 x 9.742 mm, 11 faces (baked)
FEATURE [Part::Cylinder] Cylinder312  label="Cylinder"
  Angle = 360
  AttacherType = Attacher::AttachEngine3D
  FirstAngle = 0
  Height = 13
  Placement = pos=(176,87,-11) rot=(0,1,0;1.5708rad)
  Radius = 1.5
  SecondAngle = 0
FEATURE [Part::MultiFuse] Fusion035002002007  label="STEERING_TIE_ROD_REAR"
  Placement = pos=(-8.30268,21.1732,-10.7968) rot=(0.023418,-0.446846,-0.894305;0.11707rad)
  Refine = true
  Shapes = -> [Fusion035002002002,Fusion035002002004,Cylinder312]
FEATURE [Part::Cylinder] Cylinder313  label="Cylinder"
  Angle = 360
  AttacherType = Attacher::AttachEngine3D
  FirstAngle = 0
  Height = 94
  Placement = pos=(66,91,20.5) rot=(0,1,0;1.5708rad)
  Radius = 1.5
  SecondAngle = 0
FEATURE [Part::MultiFuse] Fusion035002002007002  label="STEERING_TIE_ROD"
  Placement = pos=(0.807969,1.4e-14,-2.14426) rot=(0,-1,0;0.03927rad)
  Refine = true
  Shapes = -> [Fusion035002002005,Fusion035002002006,Cylinder313]
FEATURE [Part::Feature] Fusion035002002007003  label="STEERING_TIE_ROD_FRONT"
  Placement = pos=(-122.3,21.17,-10.8) rot=(0.02005,-0.451129,-0.892233;0.117112rad)
  shape: bbox 38.71 x 10.54 x 9.743 mm, 23 faces (baked)
FEATURE [App::DocumentObjectGroup] Group011  label="steering"
  Group = -> [Fusion046002,Fillet003001,Fillet004001,Cut037001,Fusion046001,Line014,Line015,Cut140005,Fusion035002002007,Fusion035002002007002,Fusion035002002007003]
FEATURE [Part::Feature] Cut140007001  label="snorkel-cap"
  Placement = pos=(-13,-45,17) rot=(0,0,1;0rad)
  shape: bbox 13 x 24 x 10 mm, 38 faces (baked)
FEATURE [Part::Feature] Cut140010001  label="snorkel-support"
  Placement = pos=(-13,-44,16) rot=(0,0,1;0rad)
  shape: bbox 3.5 x 8 x 6 mm, 7 faces (baked)
FEATURE [Part::Feature] Cut140011001  label="snorkel-pipe"
  Placement = pos=(-13,-44,16) rot=(0,0,1;0rad)
  shape: bbox 9.5 x 20 x 87 mm, 23 faces (baked)
FEATURE [Part::Feature] Cut140012001  label="snorkel-s-pipe"
  Placement = pos=(-13,-44,9) rot=(0,0,1;0rad)
  shape: bbox 9.004 x 23.99 x 18.8 mm, 11 faces (baked)
FEATURE [Part::Feature] Cut140012002  label="front-lights-left-proyector"
  Placement = pos=(-12.5,-156.5,17) rot=(0,0,1;0rad)
  shape: bbox 6.204 x 21.46 x 15.99 mm, 23 faces (baked)
FEATURE [Part::Feature] Fillet133003  label="front-lights-left-glass"
  Placement = pos=(-12.5,-156.5,17) rot=(0,0,1;0rad)
  shape: bbox 0.684 x 20.49 x 14.49 mm, 18 faces (baked)
FEATURE [Part::Feature] Fusion102001  label="cab-fiat-logo"
  Placement = pos=(-13.5,57,60) rot=(0.57735,-0.57735,-0.57735;2.0944rad)
  shape: bbox 1 x 34.06 x 8 mm, 68 faces (baked)
FEATURE [Part::Feature] Fusion115001  label="cab-180-logo"
  Placement = pos=(-11.5,-5,29) rot=(0.57735,-0.57735,-0.57735;2.0944rad)
  shape: bbox 1 x 12.95 x 5 mm, 78 faces (baked)
FEATURE [App::DocumentObjectGroup] Group002  label="Cab"
  Group = -> [Cut017001,Fusion009001,Cut085001,Fusion074001,Cut103001,Cut113001,Cut114001,Cut136001,Cut138001,Fillet133001,Cut140001,Part__Mirroring016001,Cut007,Cut006,Cut140007001,Cut140010001,Cut140011001,Cut140012001,Cut140012002,Fillet133003,Fusion102001,Fusion115001]
FEATURE [Part::Feature] Fusion513001  label="rear-axle"
  Placement = pos=(282.5,-45,25) rot=(0,0,1;0rad)
  shape: bbox 48 x 122 x 40 mm, 15 faces (baked)
FEATURE [App::DocumentObjectGroup] Group001  label="Axles"
  Group = -> [Fusion500001,Fusion500002,Fusion513001]
FEATURE [Part::Feature] Cut048001  label="transfercase-exit-part"
  Placement = pos=(193,25,-22.5) rot=(0,0,1;0rad)
  shape: bbox 7.1 x 80 x 32 mm, 56 faces (baked)
FEATURE [Part::Feature] Fillet038001  label="transfercase-clutch-part"
  Placement = pos=(193,25,-22.5) rot=(0,0,1;0rad)
  shape: bbox 8 x 29.22 x 29.22 mm, 11 faces (baked)
FEATURE [Part::Feature] Cut046001  label="transfercase-front-part"
  Placement = pos=(193,25,-22.5) rot=(0,0,1;0rad)
  shape: bbox 24.5 x 80 x 36 mm, 83 faces (baked)
FEATURE [Part::Feature] Cut042001  label="transfercase-middle-part"
  Placement = pos=(193,25,-22.5) rot=(0,0,1;0rad)
  shape: bbox 12 x 34 x 40 mm, 77 faces (baked)
FEATURE [Part::Feature] Cut018001  label="transfercase-rear-part"
  Placement = pos=(193,25,-22.5) rot=(0,0,1;0rad)
  shape: bbox 22 x 34 x 40 mm, 36 faces (baked)
FEATURE [Part::Cylinder] Cylinder1075  label="Cylinder1551"
  Angle = 360
  AttacherType = Attacher::AttachEngine3D
  FirstAngle = 0
  Height = 11.5
  Placement = pos=(254,40,-3.5) rot=(0,1,0;1.5708rad)
  Radius = 5.5
  SecondAngle = 0
FEATURE [Part::Cylinder] Cylinder1077  label="Cylinder1553"
  Angle = 360
  AttacherType = Attacher::AttachEngine3D
  FirstAngle = 0
  Height = 79
  Placement = pos=(265.5,40,-3.5) rot=(0,1,0;1.85878rad)
  Radius = 5.5
  SecondAngle = 0
FEATURE [Part::Cylinder] Cylinder1076  label="Cylinder1552"
  Angle = 360
  AttacherType = Attacher::AttachEngine3D
  FirstAngle = 0
  Height = 11.5
  Placement = pos=(341,40,-26) rot=(0,1,0;1.5708rad)
  Radius = 5.5
  SecondAngle = 0
FEATURE [Part::MultiFuse] Fusion035002002007004  label="rear-propshaft"
  Refine = true
  Shapes = -> [Cylinder1075,Cylinder1077,Cylinder1076]
FEATURE [Part::Feature] Fusion047001  label="gearbox"
  Placement = pos=(58,40,4.5) rot=(0.57735,0.57735,0.57735;2.0944rad)
  shape: bbox 108 x 46 x 60 mm, 52 faces (baked)
FEATURE [Part::Cylinder] Cylinder1078  label="Cylinder1551"
  Angle = 360
  AttacherType = Attacher::AttachEngine3D
  FirstAngle = 0
  Height = 11.5
  Placement = pos=(143,40,4.5) rot=(0,1,0;1.5708rad)
  Radius = 5.5
  SecondAngle = 0
FEATURE [Part::Cylinder] Cylinder1079  label="Cylinder1551"
  Angle = 360
  AttacherType = Attacher::AttachEngine3D
  FirstAngle = 0
  Height = 11.5
  Placement = pos=(174,40,4.5) rot=(0,1,0;1.5708rad)
  Radius = 5.5
  SecondAngle = 0
FEATURE [Part::Cylinder] Cylinder1080  label="Cylinder1551"
  Angle = 360
  AttacherType = Attacher::AttachEngine3D
  FirstAngle = 0
  Height = 18.5
  Placement = pos=(155,40,4.5) rot=(0,1,0;1.5708rad)
  Radius = 5.5
  SecondAngle = 0
FEATURE [Part::MultiFuse] Fusion035002002007005  label="motor-prppshaft"
  Refine = true
  Shapes = -> [Cylinder1078,Cylinder1079,Cylinder1080]
FEATURE [App::DocumentObjectGroup] Group012  label="Transmission"
  Group = -> [Cut048001,Fillet038001,Cut046001,Cut042001,Cut018001,Fusion035002002007005,Fusion047001,Fusion035002002007004]
FEATURE [Part::Box] Box182  label="Cube207"
  AttacherType = Attacher::AttachEngine3D
  Height = 10
  Length = 65
  Width = 80
FEATURE [Part::Box] Box002  label="Cube002"
  AttacherType = Attacher::AttachEngine3D
  Height = 10
  Length = 10
  Placement = pos=(0,-2,4) rot=(0,0,1;0rad)
  Width = 10
FEATURE [Part::Box] Box003
  AttacherType = Attacher::AttachEngine3D
  Height = 10
  Length = 45
  Placement = pos=(10,10,0) rot=(0,0,1;0rad)
  Width = 9
FEATURE [Part::Box] Box004
  AttacherType = Attacher::AttachEngine3D
  Height = 10
  Length = 45
  Placement = pos=(10,61,0) rot=(0,0,1;0rad)
  Width = 9
FEATURE [Part::Box] Box005
  AttacherType = Attacher::AttachEngine3D
  Height = 12
  Length = 65
  Placement = pos=(0,15,0) rot=(-1,0,0;0.401426rad)
  Width = 10
FEATURE [Part::Box] Box006
  AttacherType = Attacher::AttachEngine3D
  Height = 12
  Length = 65
  Placement = pos=(0,15,0) rot=(-1,0,0;0.401426rad)
  Width = 10
FEATURE [Part::Box] Box009
  AttacherType = Attacher::AttachEngine3D
  Height = 2
  Length = 10
  Placement = pos=(0,61,8) rot=(0,0,1;0rad)
  Width = 11
FEATURE [Part::Box] Box010
  AttacherType = Attacher::AttachEngine3D
  Height = 2
  Length = 10
  Placement = pos=(55,8,8) rot=(0,0,1;0rad)
  Width = 11
FEATURE [Part::Box] Box183
  AttacherType = Attacher::AttachEngine3D
  Height = 10
  Length = 9
  Placement = pos=(20,11,0) rot=(0,0,1;0rad)
  Width = 21
FEATURE [Part::Box] Box184
  AttacherType = Attacher::AttachEngine3D
  Height = 5
  Length = 8
  Placement = pos=(-14,-19,0) rot=(0,0,1;0rad)
  Width = 20
FEATURE [Part::Box] Box185
  AttacherType = Attacher::AttachEngine3D
  Height = 3.4
  Length = 17
  Placement = pos=(-9,11,0) rot=(0,0,1;0rad)
  Width = 15
FEATURE [Part::Box] Box186
  AttacherType = Attacher::AttachEngine3D
  Height = 1.6
  Length = 19
  Placement = pos=(-10,10,3.4) rot=(0,0,1;0rad)
  Width = 10
FEATURE [Part::Box] Box187
  AttacherType = Attacher::AttachEngine3D
  Height = 1
  Length = 4
  Placement = pos=(-2.5,25,0) rot=(0,0,1;0rad)
  Width = 1
FEATURE [Part::Box] Box188
  AttacherType = Attacher::AttachEngine3D
  Height = 5
  Length = 8
  Placement = pos=(34,-19,2) rot=(0,0,1;0rad)
  Width = 25
FEATURE [Part::Box] Box189
  AttacherType = Attacher::AttachEngine3D
  Height = 5
  Length = 8
  Placement = pos=(-14,-19,2) rot=(0,0,1;0rad)
  Width = 25
FEATURE [Part::Box] Box190
  AttacherType = Attacher::AttachEngine3D
  Height = 15
  Length = 53
  Placement = pos=(-13,0,-5) rot=(0,0,1;0rad)
  Width = 10
FEATURE [Part::Box] Box191
  AttacherType = Attacher::AttachEngine3D
  Height = 1
  Length = 19
  Placement = pos=(-9,-5,10) rot=(0,0,1;0rad)
  Width = 5
FEATURE [Part::Box] Box192
  AttacherType = Attacher::AttachEngine3D
  Height = 10
  Length = 43
  Placement = pos=(11,0,10) rot=(0,0,1;0rad)
  Width = 10
FEATURE [Part::Box] Box193
  AttacherType = Attacher::AttachEngine3D
  Height = 33
  Length = 56
  Placement = pos=(11,-15,10) rot=(0,0,1;0rad)
  Width = 10
FEATURE [Part::Box] Box194
  AttacherType = Attacher::AttachEngine3D
  Height = 10
  Length = 13
  Placement = pos=(54,0,10) rot=(0,0,1;0rad)
  Width = 10
FEATURE [Part::Box] Box195  label="Cube004"
  AttacherType = Attacher::AttachEngine3D
  Height = 10
  Length = 56
  Placement = pos=(6,15,2) rot=(1,0,0;0.698132rad)
  Width = 10
FEATURE [Part::Box] Box206  label="Cube208"
  AttacherType = Attacher::AttachEngine3D
  Height = 10
  Length = 65
  Placement = pos=(0,19,0) rot=(0,0,1;0rad)
  Width = 42
FEATURE [Part::Box] Box207  label="Cube003"
  AttacherType = Attacher::AttachEngine3D
  Height = 10
  Length = 10
  Placement = pos=(0,-2,4) rot=(0,0,1;0rad)
  Width = 10
FEATURE [Part::Box] Box208
  AttacherType = Attacher::AttachEngine3D
  Height = 2
  Length = 10
  Placement = pos=(0,8,8) rot=(0,0,1;0rad)
  Width = 11
FEATURE [Part::Box] Box209
  AttacherType = Attacher::AttachEngine3D
  Height = 2
  Length = 10
  Placement = pos=(55,61,8) rot=(0,0,1;0rad)
  Width = 11
FEATURE [Part::Box] Box210
  AttacherType = Attacher::AttachEngine3D
  Height = 5
  Length = 56
  Placement = pos=(-14,1,0) rot=(0,0,1;0rad)
  Width = 10
FEATURE [Part::Box] Box211
  AttacherType = Attacher::AttachEngine3D
  Height = 10
  Length = 17
  Placement = pos=(20,22,0) rot=(0,0,1;0rad)
  Width = 10
FEATURE [Part::Box] Box212
  AttacherType = Attacher::AttachEngine3D
  Height = 3.4
  Length = 21
  Placement = pos=(8,11,0) rot=(0,0,1;0rad)
  Width = 5
FEATURE [Part::Box] Box213
  AttacherType = Attacher::AttachEngine3D
  Height = 5
  Length = 8
  Placement = pos=(34,-19,0) rot=(0,0,1;0rad)
  Width = 20
FEATURE [Part::Chamfer] Chamfer314013
  Base = -> Box207
  Edges = 1 edges r=6: [Edge9]
FEATURE [Part::Chamfer] Chamfer314014
  Base = -> Box002
  Edges = 1 edges r=6: [Edge9]
FEATURE [Part::Cut] Cut140012003
  Base = -> Box182
  Refine = true
  Tool = -> Box206
FEATURE [Part::Cut] Cut140012009
  Placement = pos=(-18,19,0) rot=(0,0,1;0rad)
  Refine = true
FEATURE [Part::Cylinder] Cylinder017
  Angle = 360
  AttacherType = Attacher::AttachEngine3D
  FirstAngle = 0
  Height = 3
  Placement = pos=(5,3,11) rot=(0,0,1;0rad)
  Radius = 3.2
  SecondAngle = 0
FEATURE [Part::Cylinder] Cylinder1081
  Angle = 360
  AttacherType = Attacher::AttachEngine3D
  FirstAngle = 0
  Height = 10
  Placement = pos=(-10,0,0) rot=(0,0,1;0rad)
  Radius = 1.25
  SecondAngle = 0
FEATURE [Part::Cylinder] Cylinder1082
  Angle = 360
  AttacherType = Attacher::AttachEngine3D
  FirstAngle = 0
  Height = 10
  Placement = pos=(-10,-10,0) rot=(0,0,1;0rad)
  Radius = 1.25
  SecondAngle = 0
FEATURE [Part::Cylinder] Cylinder1083
  Angle = 360
  AttacherType = Attacher::AttachEngine3D
  FirstAngle = 0
  Height = 10
  Placement = pos=(5,19,0) rot=(0,0,1;0rad)
  Radius = 1.6
  SecondAngle = 0
FEATURE [Part::Cylinder] Cylinder1084
  Angle = 360
  AttacherType = Attacher::AttachEngine3D
  FirstAngle = 0
  Height = 10
  Placement = pos=(-6,19,0) rot=(0,0,1;0rad)
  Radius = 1.6
  SecondAngle = 0
FEATURE [Part::Cylinder] Cylinder1085
  Angle = 360
  AttacherType = Attacher::AttachEngine3D
  FirstAngle = 0
  Height = 10
  Placement = pos=(15,5,10) rot=(0,0,1;0rad)
  Radius = 1.6
  SecondAngle = 0
FEATURE [Part::Cylinder] Cylinder1086
  Angle = 360
  AttacherType = Attacher::AttachEngine3D
  FirstAngle = 0
  Height = 10
  Placement = pos=(50,5,10) rot=(0,0,1;0rad)
  Radius = 1.6
  SecondAngle = 0
FEATURE [Part::Cylinder] Cylinder028
  Angle = 360
  AttacherType = Attacher::AttachEngine3D
  FirstAngle = 0
  Height = 3
  Placement = pos=(15,5,17) rot=(0,0,1;0rad)
  Radius = 3.2
  SecondAngle = 0
FEATURE [Part::Cylinder] Cylinder1087
  Angle = 360
  AttacherType = Attacher::AttachEngine3D
  FirstAngle = 0
  Height = 3
  Placement = pos=(50,5,17) rot=(0,0,1;0rad)
  Radius = 3.2
  SecondAngle = 0
FEATURE [Part::Cylinder] Cylinder1088
  Angle = 360
  AttacherType = Attacher::AttachEngine3D
  FirstAngle = 0
  Height = 10
  Radius = 1.25
  SecondAngle = 0
FEATURE [Part::Cylinder] Cylinder1089
  Angle = 360
  AttacherType = Attacher::AttachEngine3D
  FirstAngle = 0
  Height = 10
  Placement = pos=(0,54,0) rot=(0,0,1;0rad)
  Radius = 1.25
  SecondAngle = 0
FEATURE [Part::Cylinder] Cylinder1090
  Angle = 360
  AttacherType = Attacher::AttachEngine3D
  FirstAngle = 0
  Height = 10
  Placement = pos=(0,54,0) rot=(0,0,1;0rad)
  Radius = 1.25
  SecondAngle = 0
FEATURE [Part::Cylinder] Cylinder1091
  Angle = 360
  AttacherType = Attacher::AttachEngine3D
  FirstAngle = 0
  Height = 10
  Radius = 1.25
  SecondAngle = 0
FEATURE [Part::Cylinder] Cylinder1092
  Angle = 360
  AttacherType = Attacher::AttachEngine3D
  FirstAngle = 0
  Height = 10
  Placement = pos=(5,0,0) rot=(0,0,1;0rad)
  Radius = 1.6
  SecondAngle = 0
FEATURE [Part::Cylinder] Cylinder1093
  Angle = 360
  AttacherType = Attacher::AttachEngine3D
  FirstAngle = 0
  Height = 10
  Placement = pos=(5,70,0) rot=(0,0,1;0rad)
  Radius = 1.6
  SecondAngle = 0
FEATURE [Part::Cylinder] Cylinder1094
  Angle = 360
  AttacherType = Attacher::AttachEngine3D
  FirstAngle = 0
  Height = 3
  Placement = pos=(5,70,0) rot=(0,0,1;0rad)
  Radius = 3.2
  SecondAngle = 0
FEATURE [Part::Cylinder] Cylinder1095
  Angle = 360
  AttacherType = Attacher::AttachEngine3D
  FirstAngle = 0
  Height = 3
  Placement = pos=(5,0,0) rot=(0,0,1;0rad)
  Radius = 3.2
  SecondAngle = 0
FEATURE [Part::Cylinder] Cylinder1096
  Angle = 360
  AttacherType = Attacher::AttachEngine3D
  FirstAngle = 0
  Height = 10
  Placement = pos=(0,70,0) rot=(0,0,1;0rad)
  Radius = 1.25
  SecondAngle = 0
FEATURE [Part::Cylinder] Cylinder1097
  Angle = 360
  AttacherType = Attacher::AttachEngine3D
  FirstAngle = 0
  Height = 10
  Radius = 1.25
  SecondAngle = 0
FEATURE [Part::Cylinder] Cylinder1098
  Angle = 360
  AttacherType = Attacher::AttachEngine3D
  FirstAngle = 0
  Height = 10
  Radius = 1.25
  SecondAngle = 0
FEATURE [Part::Cylinder] Cylinder1099
  Angle = 360
  AttacherType = Attacher::AttachEngine3D
  FirstAngle = 0
  Height = 10
  Placement = pos=(0,70,0) rot=(0,0,1;0rad)
  Radius = 1.25
  SecondAngle = 0
FEATURE [Part::Cylinder] Cylinder1100
  Angle = 360
  AttacherType = Attacher::AttachEngine3D
  FirstAngle = 0
  Height = 10
  Placement = pos=(5,3,4) rot=(0,0,1;0rad)
  Radius = 1.25
  SecondAngle = 0
FEATURE [Part::Cylinder] Cylinder1101
  Angle = 360
  AttacherType = Attacher::AttachEngine3D
  FirstAngle = 0
  Height = 3
  Placement = pos=(5,3,11) rot=(0,0,1;0rad)
  Radius = 3.2
  SecondAngle = 0
FEATURE [Part::Cylinder] Cylinder083
  Angle = 360
  AttacherType = Attacher::AttachEngine3D
  FirstAngle = 0
  Height = 10
  Placement = pos=(5,3,4) rot=(0,0,1;0rad)
  Radius = 1.25
  SecondAngle = 0
FEATURE [Part::Cylinder] Cylinder1102
  Angle = 360
  AttacherType = Attacher::AttachEngine3D
  FirstAngle = 0
  Height = 10
  Placement = pos=(-10,0,0) rot=(0,0,1;0rad)
  Radius = 1.25
  SecondAngle = 0
FEATURE [Part::Cylinder] Cylinder1103
  Angle = 360
  AttacherType = Attacher::AttachEngine3D
  FirstAngle = 0
  Height = 10
  Placement = pos=(-10,-10,0) rot=(0,0,1;0rad)
  Radius = 1.25
  SecondAngle = 0
FEATURE [Part::Fillet] Fillet007
  Base = -> Box192
  Edges = 1 edges r=3: [Edge4]
  Placement = pos=(0,-1,0) rot=(0,0,1;0rad)
FEATURE [Part::Fillet] Fillet103
  Base = -> Cut140012009
  Edges = 1 edges r=0.6: [Edge14]
  Placement = pos=(29,0,0) rot=(0,0,1;0rad)
FEATURE [Part::Fillet] Fillet108
  Base = -> Box194
  Edges = 1 edges r=3: [Edge8]
  Placement = pos=(-5,-1,0) rot=(0,0,1;0rad)
FEATURE [Part::MultiFuse] Fusion035002002007006
  Placement = pos=(5,13,0) rot=(0,0,1;0rad)
  Refine = true
  Shapes = -> [Cylinder1088,Cylinder1089]
FEATURE [Part::MultiFuse] Fusion008
  Placement = pos=(0,5,0) rot=(0,0,1;0rad)
  Refine = true
  Shapes = -> [Cylinder1093,Cylinder1092]
FEATURE [Part::MultiFuse] Fusion035002002007007
  Refine = true
  Shapes = -> [Cylinder1100,Cylinder017]
FEATURE [Part::MultiFuse] Fusion035002002007008
  Placement = pos=(0,74,0) rot=(0,0,1;0rad)
  Refine = true
  Shapes = -> [Cylinder083,Cylinder1101]
FEATURE [Part::MultiFuse] Fusion035002002007009
  Refine = true
  Shapes = -> [Fusion035002002007007,Fusion035002002007008]
FEATURE [Part::MultiFuse] Fusion035002002007010
  Refine = true
  Shapes = -> [Box208,Box010,Box209,Box009]
FEATURE [Part::MultiFuse] Fusion035002002007011
  Refine = true
  Shapes = -> [Box211,Box183]
FEATURE [Part::Cut] Cut140012004
  Base = -> Fillet103
  Refine = true
  Tool = -> Fusion035002002007011
FEATURE [Part::MultiFuse] Fusion035002002007012
  Refine = true
  Shapes = -> [Box210,Cut140012004,Box212]
FEATURE [Part::MultiFuse] Fusion025
  Refine = true
  Shapes = -> [Cylinder1083,Cylinder1084]
FEATURE [Part::Cut] Cut014
  Base = -> Box185
  Refine = true
  Tool = -> Fusion025
FEATURE [Part::MultiFuse] Fusion026
  Refine = true
  Shapes = -> [Box213,Box184,Cut014,Fusion035002002007012]
FEATURE [Part::MultiFuse] Fusion035002002007013
  Placement = pos=(48,-4,0) rot=(0,0,1;0rad)
  Refine = true
  Shapes = -> [Cylinder1082,Cylinder1081]
FEATURE [Part::MultiFuse] Fusion035002002007015
  Placement = pos=(0,-4,0) rot=(0,0,1;0rad)
  Refine = true
  Shapes = -> [Cylinder1103,Cylinder1102]
FEATURE [Part::MultiFuse] Fusion035002002007014
  Refine = true
  Shapes = -> [Fusion035002002007015,Fusion035002002007013]
FEATURE [Part::MultiFuse] Fusion035002002007016
  Refine = true
  Shapes = -> [Box188,Box189]
FEATURE [Part::Cut] Cut140012012
  Base = -> Fusion035002002007016
  Refine = true
  Tool = -> Fusion035002002007014
FEATURE [Part::Fillet] Fillet006
  Base = -> Cut140012012
  Edges = 2 edges r=2: [Edge6,Edge23]
FEATURE [Part::Chamfer] Chamfer314016
  Base = -> Fillet006
  Edges = 2 edges r=2: [Edge18,Edge31]
FEATURE [Part::MultiFuse] Fusion035002002007019
  Refine = true
  Shapes = -> [Cylinder1085,Cylinder1086,Cylinder028,Cylinder1087]
FEATURE [Part::MultiFuse] Fusion035002002007020
  Placement = pos=(0,1,0) rot=(0,0,1;0rad)
  Refine = true
  Shapes = -> [Fillet108,Fillet007]
FEATURE [Part::MultiFuse] Fusion102
  Placement = pos=(60,13,0) rot=(0,0,1;0rad)
  Refine = true
  Shapes = -> [Cylinder1091,Cylinder1090]
FEATURE [Part::MultiFuse] Fusion002
  Refine = true
  Shapes = -> [Fusion035002002007006,Fusion102]
FEATURE [Part::MultiFuse] Fusion103
  Placement = pos=(0,5,0) rot=(0,0,1;0rad)
  Refine = true
  Shapes = -> [Cylinder1093,Cylinder1092]
FEATURE [Part::MultiFuse] Fusion104
  Placement = pos=(0,5,7) rot=(0,0,1;0rad)
  Refine = true
  Shapes = -> [Cylinder1094,Cylinder1095]
FEATURE [Part::MultiFuse] Fusion005
  Placement = pos=(55,0,0) rot=(0,0,1;0rad)
  Refine = true
  Shapes = -> [Fusion103,Fusion104]
FEATURE [Part::MultiFuse] Fusion035002002007022
  Placement = pos=(0,5,7) rot=(0,0,1;0rad)
  Refine = true
  Shapes = -> [Cylinder1094,Cylinder1095]
FEATURE [Part::MultiFuse] Fusion106
  Placement = pos=(20,0,0) rot=(0,0,1;0rad)
  Refine = true
  Shapes = -> [Fusion008,Fusion035002002007022]
FEATURE [Part::MultiFuse] Fusion009
  Refine = true
  Shapes = -> [Fusion005,Fusion106]
FEATURE [Part::MultiFuse] Fusion035002002007023
  Refine = true
  Shapes = -> [Box003,Box004]
FEATURE [Part::Cut] Cut140012005
  Base = -> Cut140012003
  Refine = true
  Tool = -> Fusion035002002007023
FEATURE [Part::Cut] Cut140012006
  Base = -> Cut140012005
  Refine = true
  Tool = -> Fusion002
FEATURE [Part::MultiFuse] Fusion108
  Placement = pos=(50,5,0) rot=(0,0,1;0rad)
  Refine = true
  Shapes = -> [Cylinder1096,Cylinder1097]
FEATURE [Part::MultiFuse] Fusion035002002007024
  Placement = pos=(15,5,0) rot=(0,0,1;0rad)
  Refine = true
  Shapes = -> [Cylinder1099,Cylinder1098]
FEATURE [Part::MultiFuse] Fusion014
  Refine = true
  Shapes = -> [Fusion009,Fusion108,Fusion035002002007024]
FEATURE [Part::MultiFuse] Fusion035002002007027
  Placement = pos=(0,-4,0) rot=(0,0,1;0rad)
  Refine = true
  Shapes = -> [Cylinder1103,Cylinder1102]
FEATURE [Part::MultiFuse] Fusion113
  Placement = pos=(48,-4,0) rot=(0,0,1;0rad)
  Refine = true
  Shapes = -> [Cylinder1082,Cylinder1081]
FEATURE [Part::MultiFuse] Fusion035002002007028
  Refine = true
  Shapes = -> [Fusion035002002007027,Fusion113]
FEATURE [Part::Cut] Cut015
  Base = -> Fusion026
  Refine = true
  Tool = -> Fusion035002002007028
FEATURE [Part::Fillet] Fillet104
  Base = -> Cut015
  Edges = 6 edges r=2: [Edge51,Edge54,Edge56,Edge58,Edge59,Edge61]
FEATURE [Part::Fillet] Fillet105
  Base = -> Fillet104
  Edges = 1 edges r=1.5: [Edge36]
FEATURE [Part::Fillet] Fillet106
  Base = -> Fillet105
  Edges = 2 edges r=3: [Edge30,Edge33]
FEATURE [Part::Cut] Cut140012010
  Base = -> Fillet106
  Refine = true
  Tool = -> Box186
FEATURE [Part::Fillet] Fillet107
  Base = -> Cut140012010
  Edges = 2 edges r=2: [Edge42,Edge63]
FEATURE [Part::Cut] Cut140012011
  Base = -> Fillet107
  Refine = true
  Tool = -> Box187
FEATURE [Part::Fillet] Fillet005
  Base = -> Cut140012011
  Edges = 1 edges r=0.99: [Edge94]
FEATURE [Part::Chamfer] Chamfer314015
  Base = -> Fillet005
  Edges = 2 edges r=1.5: [Edge34,Edge36]
FEATURE [Part::MultiFuse] Fusion035002002007017
  Placement = pos=(0,0,21) rot=(-1,0,0;1.5708rad)
  Refine = true
  Shapes = -> [Chamfer314015,Chamfer314016]
FEATURE [Part::Cut] Cut140012013
  Base = -> Fusion035002002007017
  Placement = pos=(0,0,0) rot=(0,0,1;3.14159rad)
  Refine = true
  Tool = -> Box190
FEATURE [Part::MultiFuse] Fusion035002002007018
  Placement = pos=(53,0,0) rot=(0,0,1;0rad)
  Refine = true
  Shapes = -> [Cut140012013,Box191]
FEATURE [Part::Cut] Cut140012014
  Base = -> Fusion035002002007018
  Placement = pos=(-5,14,0) rot=(0,0,1;0rad)
  Refine = true
  Tool = -> Box193
FEATURE [Part::MultiFuse] Fusion035002002007021
  Refine = true
  Shapes = -> [Cut140012014,Fusion035002002007020]
FEATURE [Part::Cut] Cut126
  Base = -> Fusion035002002007021
  Refine = true
  Tool = -> Fusion035002002007019
FEATURE [Part::Cut] Cut127  label="steering-servo-holder"
  Base = -> Cut126
  Placement = pos=(133,80,18) rot=(0,0,1;3.14159rad)
  Refine = true
  Tool = -> Box195
FEATURE [Part::Mirroring] Part__Mirroring016004002  label="Box005 (Mirror #1)"
  Base = (0,0,0)
  Normal = (0,1,0)
  Placement = pos=(0,80,0) rot=(0,0,1;0rad)
  Source = -> Box005
FEATURE [Part::MultiFuse] Fusion035002002007025
  Refine = true
  Shapes = -> [Part__Mirroring016004002,Box006]
FEATURE [Part::Cut] Cut008
  Base = -> Cut140012006
  Refine = true
  Tool = -> Fusion035002002007025
FEATURE [Part::Cut] Cut140012007
  Base = -> Cut008
  Refine = true
  Tool = -> Fusion014
FEATURE [Part::Mirroring] Part__Mirroring016004003  label="Chamfer (Mirror #2)"
  Base = (0,0,0)
  Normal = (0,1,0)
  Placement = pos=(0,80,0) rot=(0,0,1;0rad)
  Source = -> Chamfer314013
FEATURE [Part::MultiFuse] Fusion035002002007026
  Refine = true
  Shapes = -> [Chamfer314014,Cut140012007,Part__Mirroring016004003]
FEATURE [Part::Cut] Cut140012008
  Base = -> Fusion035002002007026
  Refine = true
  Tool = -> Fusion035002002007009
FEATURE [Part::Cut] Cut011  label="gearbox-holder"
  Base = -> Cut140012008
  Placement = pos=(133,80,20) rot=(0,0,1;3.14159rad)
  Refine = true
  Tool = -> Fusion035002002007010
FEATURE [App::DocumentObjectGroup] Group003  label="Frame"
  Group = -> [Fillet094,Fillet095,Fillet098,Cut186,Cut187,Cut088,Cut089,Cut090,Cut092,Cut107,Cut051,Cut140,Fusion015,Cut011,Cut127,Group011]
FEATURE [Part::Feature] Fusion135001  label="seat-right"
  Placement = pos=(-18,64,16) rot=(0,0,1;0rad)
  shape: bbox 43.42 x 39.01 x 45.02 mm, 127 faces (baked)
FEATURE [Part::Feature] Fusion137001  label="seat-left"
  Placement = pos=(-18,-44,16) rot=(0,0,1;0rad)
  shape: bbox 43.42 x 47.01 x 61.02 mm, 284 faces (baked)
FEATURE [Part::Feature] Cylinder093001  label="steering-rod-METAL"
  Placement = pos=(4.5,94,16) rot=(0,1,0;0.261799rad)
  shape: bbox 18.36 x 3.2 x 57.82 mm, 3 faces (baked)
FEATURE [Part::Feature] Fusion141001  label="steering-wheel"
  Placement = pos=(-13,-44,16) rot=(0,0,1;0rad)
  shape: bbox 37.64 x 38.97 x 11.46 mm, 57 faces (baked)
FEATURE [Part::Feature] Cut162001  label="seat-support-left"
  Placement = pos=(-13,-44,16) rot=(0,0,1;0rad)
  shape: bbox 26.68 x 34 x 19 mm, 12 faces (baked)
FEATURE [Part::Feature] Cut163001  label="seat-support-right"
  Placement = pos=(-13,-152,16) rot=(0,0,1;0rad)
  shape: bbox 26.68 x 34 x 19 mm, 12 faces (baked)
FEATURE [Part::Feature] Cylinder112001  label="shift-rod-METAL"
  Placement = pos=(29.5,71,23) rot=(0,0,1;0rad)
  shape: bbox 2 x 2 x 45 mm, 3 faces (baked)
FEATURE [Part::Feature] Cut167001  label="gear-lever-splitter"
  Placement = pos=(-13,-44,16) rot=(0,0,1;0rad)
  shape: bbox 6 x 4 x 5.022 mm, 16 faces (baked)
FEATURE [Part::Feature] Cut168001  label="gear-lever-knob"
  Placement = pos=(-13,-44,16) rot=(0,0,1;0rad)
  shape: bbox 4.33 x 4.33 x 2 mm, 7 faces (baked)
FEATURE [Part::Feature] Cut169001  label="steering-hub"
  Placement = pos=(-13,-44,16) rot=(0,0,1;0rad)
  shape: bbox 19.6 x 12.01 x 25.41 mm, 68 faces (baked)
FEATURE [Part::Feature] Fusion156001  label="dashboard-instruments"
  Placement = pos=(-13,-44,16) rot=(0,0,1;0rad)
  shape: bbox 13.5 x 40 x 1.7 mm, 59 faces (baked)
FEATURE [Part::Feature] Fusion157001  label="dashboard"
  Placement = pos=(-13,-44,16) rot=(0,0,1;0rad)
  shape: bbox 20 x 154 x 22 mm, 50 faces (baked)
FEATURE [Part::Feature] Cut175001  label="central-tunnel"
  Placement = pos=(-13,-44,16) rot=(0,0,1;0rad)
  shape: bbox 67 x 56 x 45 mm, 40 faces (baked)
FEATURE [Part::Feature] Cut180001  label="right-panel"
  Placement = pos=(-13,-44,16) rot=(0,0,1;0rad)
  shape: bbox 83.37 x 53 x 34 mm, 31 faces (baked)
FEATURE [Part::Feature] Cut182001  label="left-panel"
  Placement = pos=(-13,-44,16) rot=(0,0,1;0rad)
  shape: bbox 83.37 x 53 x 34 mm, 20 faces (baked)
FEATURE [Part::Feature] Fusion164001  label="seat-support-slider-upper-left"
  Placement = pos=(-13,-152,16) rot=(0,0,1;0rad)
  shape: bbox 24 x 30 x 6 mm, 14 faces (baked)
FEATURE [Part::Feature] Fillet179001  label="seat-support-slider-lower-left"
  Placement = pos=(-13,-152,16) rot=(0,0,1;0rad)
  shape: bbox 24 x 26 x 6 mm, 18 faces (baked)
FEATURE [Part::Feature] Fusion167001  label="seat-support-slider-upper-right"
  Placement = pos=(-13,-44,16) rot=(0,0,1;0rad)
  shape: bbox 24 x 30 x 6 mm, 14 faces (baked)
FEATURE [Part::Feature] Fillet180001  label="seat-support-slider-lower-right"
  Placement = pos=(-13,-44,16) rot=(0,0,1;0rad)
  shape: bbox 24 x 26 x 6 mm, 18 faces (baked)
FEATURE [Part::Feature] Fillet185001  label="fake-bed"
  Placement = pos=(-10,-44,16) rot=(0,0,1;0rad)
  shape: bbox 55 x 148 x 35 mm, 37 faces (baked)
FEATURE [App::DocumentObjectGroup] Group013  label="Cab internals"
  Group = -> [Fusion135001,Fusion137001,Cylinder093001,Fusion141001,Cut162001,Cut163001,Cylinder112001,Cut167001,Cut168001,Cut169001,Fusion156001,Fusion157001,Cut175001,Cut180001,Cut182001,Fusion164001,Fillet179001,Fusion167001,Fillet180001,Fillet185001]
